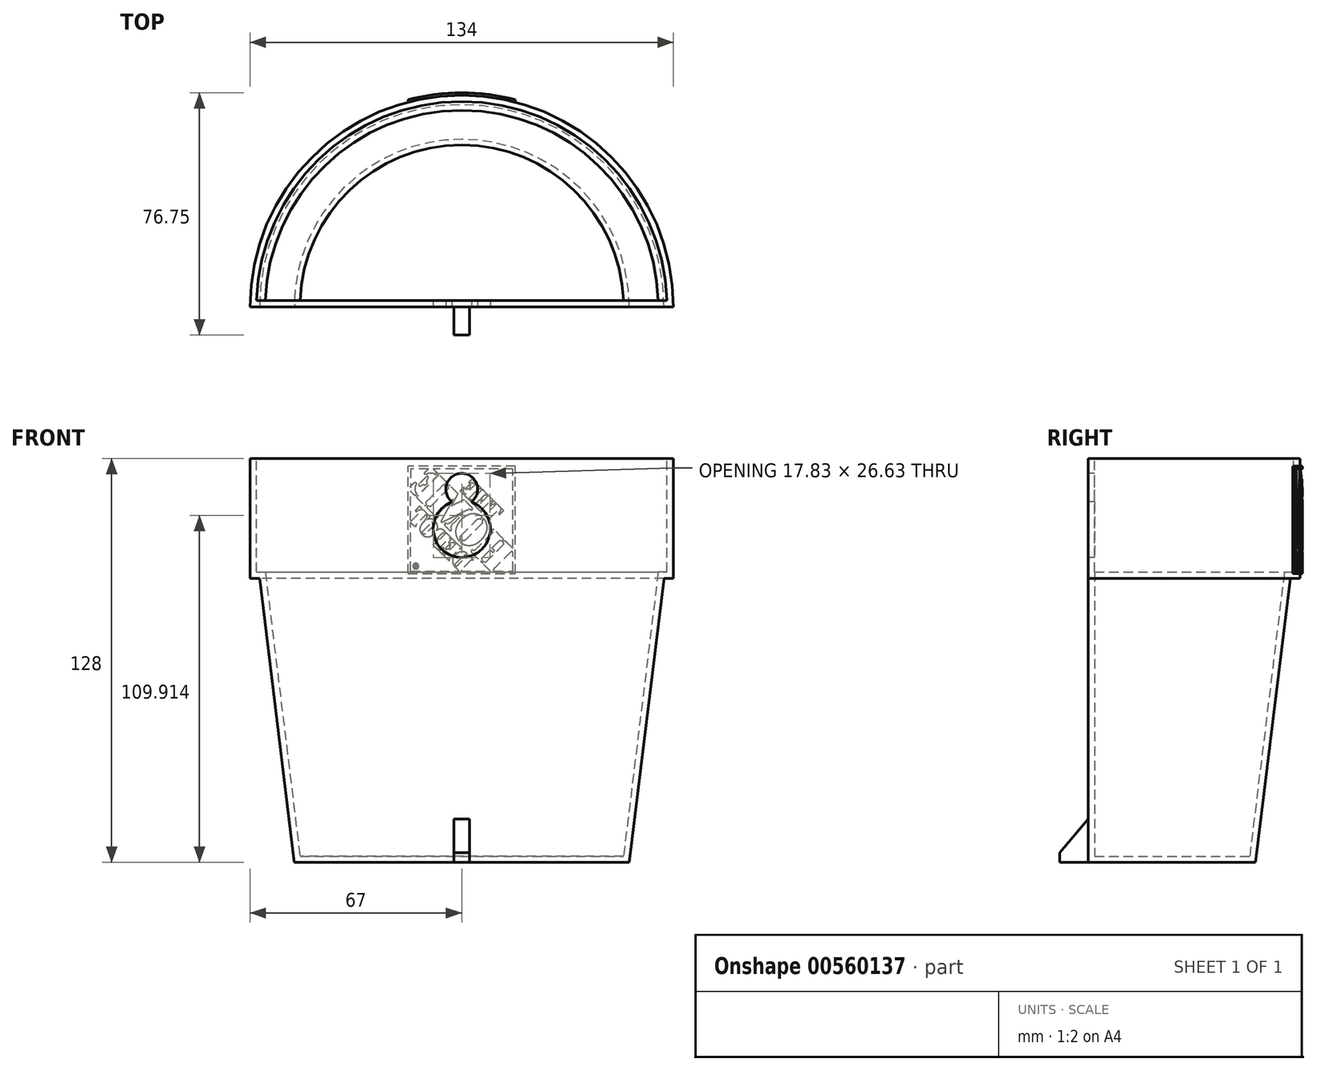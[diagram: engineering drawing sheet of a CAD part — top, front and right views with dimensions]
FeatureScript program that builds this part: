
annotation { "Feature Type Name" : "Feature", "Feature Type Description" : "" }
export const myFeature = defineFeature(function(context is Context, id is Id, definition is map)
    precondition{}
    {
        {
            var Q0;
            Q0=qCreatedBy(makeId("Front.planeOp"),FACE);
            var sketch = newSketch(context, id + "F0", { "sketchPlane" : qUnion([Q0])});
            skLineSegment(sketch, "E0", {"start": v(0, 77.42) * mm, "end": v(-67, 77.42) * mm});
            skLineSegment(sketch, "E1", {"start": v(-67, 77.42) * mm, "end": v(-67, 39.42) * mm});
            skLineSegment(sketch, "E2", {"start": v(0, -50.58) * mm, "end": v(-53, -50.58) * mm});
            skLineSegment(sketch, "E3", {"start": v(-67, 39.42) * mm, "end": v(-64, 39.42) * mm});
            skLineSegment(sketch, "E4", {"start": v(0, 77.42) * mm, "end": v(0, -50.58) * mm});
            skLineSegment(sketch, "E5", {"start": v(-64, 39.42) * mm, "end": v(-53, -50.58) * mm});
            skLineSegment(sketch, "E6.MirrorCS", {"start": v(0, 77.42) * mm, "end": v(67, 77.42) * mm});
            skLineSegment(sketch, "E7.MirrorCS", {"start": v(67, 77.42) * mm, "end": v(67, 39.42) * mm});
            skLineSegment(sketch, "E8.MirrorCS", {"start": v(67, 39.42) * mm, "end": v(64, 39.42) * mm});
            skLineSegment(sketch, "E9.MirrorCS", {"start": v(64, 39.42) * mm, "end": v(53, -50.58) * mm});
            skLineSegment(sketch, "E10.MirrorCS", {"start": v(0, -50.58) * mm, "end": v(53, -50.58) * mm});
            skSolve(sketch);
        }
        {
            var Q0;
            {var subQ0=sQuery(id+"F0.wireOp",EDGE,"E3");Q0=makeQuery(id+"F0.imprint","IMPRINT",FACE,{"disambiguationData":[TD([[makeQuery(id+"F0.imprint","IMPRINT",EDGE,{"derivedFrom":subQ0}),1.0]])]});}
            var Q1;
            {var subQ1=sQuery(id+"F0.wireOp",EDGE,"E0");Q1=makeQuery(id+"F0.imprint","IMPRINT",FACE,{"disambiguationData":[TD([[makeQuery(id+"F0.imprint","IMPRINT",EDGE,{"derivedFrom":subQ1}),1.0]])]});}
            var Q2;
            Q2=makeQuery(id+"F0.imprint","IMPRINT",FACE,{"disambiguationData":[TD([[makeQuery(id+"F0.imprint","IMPRINT",EDGE,{"derivedFrom":sQuery(id+"F0.wireOp",EDGE,"Kfnrekvc-ZjTY-c2iQ-cK4z-hKnBe4uEAVNk")}),1.0]])]});
            var Q3;
            Q3=sQuery(id+"F0.wireOp",EDGE,"E4");
            revolve(context, id + "F1", {"entities" : qUnion([Q0, Q1, Q2]), "axis" : qUnion([Q3]), "revolveType" : RevolveType.ONE_DIRECTION, "angle" : 180 * degree});
        }
        {
            var Q0;
            Q0=makeQuery(id+"FK2OT3XlAi37Aaq_1.splitOp","SPLIT",FACE,{"derivedFrom":makeQuery(id+"F1.opRevolve","SWEPT_FACE",FACE,{"disambiguationData":[OSD([sQuery(id+"F0.wireOp",EDGE,"E0")])]}),"isFromBackBody":true});
            shell(context, id + "F2", {"entities" : qUnion([Q0]), "thickness" : 2 * mm});
        }
        {
            var Q0;
            Q0=qCreatedBy(makeId("Front.planeOp"),FACE);
            var sketch = newSketch(context, id + "F3", { "sketchPlane" : qUnion([Q0])});
            skLineSegment(sketch, "E11.bottom", {"start": v(-2.5, -35.58) * mm, "end": v(2.5, -35.58) * mm});
            skLineSegment(sketch, "E11.top", {"start": v(-2.5, -50.58) * mm, "end": v(2.5, -50.58) * mm});
            skLineSegment(sketch, "E11.left", {"start": v(-2.5, -35.58) * mm, "end": v(-2.5, -50.58) * mm});
            skLineSegment(sketch, "E11.right", {"start": v(2.5, -35.58) * mm, "end": v(2.5, -50.58) * mm});
            skPoint(sketch, "E11.middle", {"position": v(0, -43.08) * mm});
            skSolve(sketch);
        }
        {
            var Q0;
            Q0=qSketchRegion(id+"F3",true);
            extrude(context, id + "F4", {"entities" : qUnion([Q0]), "operationType" : NewBodyOperationType.ADD, "depth" : 9 * mm});
        }
        {
            var Q0;
            Q0=qCreatedBy(makeId("Front.planeOp"),FACE);
            var sketch = newSketch(context, id + "F5", { "sketchPlane" : qUnion([Q0])});
            skCircle(sketch, "E12", {"center": v(0, 67.6) * mm, "radius": 5.05 * mm});
            skCircle(sketch, "E13", {"center": v(0, 55.07) * mm, "radius": 9.05 * mm});
            skSolve(sketch);
        }
        {
            var Q0;
            {var subQ0=sQuery(id+"F5.wireOp",EDGE,"E13");var subQ1=sQuery(id+"F5.wireOp",EDGE,"E12");var subQ2=makeQuery(id+"F5.imprint","INTERSECT",VERTEX,{"disambiguationData":[OD(0.0)],"derivedFrom":[subQ1,subQ0]});Q0=makeQuery(id+"F5.imprint","IMPRINT",FACE,{"disambiguationData":[TD([[makeQuery(id+"F5.imprint","IMPRINT",EDGE,{"disambiguationData":[TD([[subQ2,1.0]])],"derivedFrom":subQ1}),1.0]])]});}
            var Q1;
            {var subQ0=sQuery(id+"F5.wireOp",EDGE,"E13");var subQ1=sQuery(id+"F5.wireOp",EDGE,"E12");var subQ2=makeQuery(id+"F5.imprint","INTERSECT",VERTEX,{"disambiguationData":[OD(0.0)],"derivedFrom":[subQ1,subQ0]});Q1=makeQuery(id+"F5.imprint","IMPRINT",FACE,{"disambiguationData":[TD([[makeQuery(id+"F5.imprint","IMPRINT",EDGE,{"disambiguationData":[TD([[subQ2,-1.0]])],"derivedFrom":subQ1}),-1.0]])]});}
            var Q2;
            {var subQ0=sQuery(id+"F5.wireOp",EDGE,"E13");var subQ1=sQuery(id+"F5.wireOp",EDGE,"E12");var subQ2=makeQuery(id+"F5.imprint","INTERSECT",VERTEX,{"disambiguationData":[OD(0.0)],"derivedFrom":[subQ1,subQ0]});Q2=makeQuery(id+"F5.imprint","IMPRINT",FACE,{"disambiguationData":[TD([[makeQuery(id+"F5.imprint","IMPRINT",EDGE,{"disambiguationData":[TD([[subQ2,-1.0]])],"derivedFrom":subQ1}),1.0]])]});}
            var Q3;
            Q3=sQuery(id+"F5.wireOp",EDGE,"E12");
            var Q4;
            Q4=sQuery(id+"F5.wireOp",EDGE,"E13");
            extrude(context, id + "F6", {"entities" : qUnion([Q0, Q1, Q2]), "operationType" : NewBodyOperationType.REMOVE, "surfaceEntities" : qUnion([Q3, Q4]), "oppositeDirection" : true, "depth" : 10 * mm});
        }
        {
            var Q0;
            Q0=makeQuery(id+"F4.opExtrude","CAP_EDGE",EDGE,{"disambiguationData":[OSD([sQuery(id+"F3.wireOp",EDGE,"E11.bottom")])],"isStart":false});
            chamfer(context, id + "F7", {"entities" : qUnion([Q0]), "chamferType" : ChamferType.OFFSET_ANGLE, "width" : 10 * mm, "oppositeDirection" : false, "angle" : 50 * degree, "tangentPropagation" : true});
        }
        {
            var Q0;
            Q0=makeQuery(id+"F1.opRevolve","SWEPT_BODY",BODY,{"disambiguationData":[OSD([sQuery(id+"F0.wireOp",EDGE,"E0"),sQuery(id+"F0.wireOp",EDGE,"E1"),sQuery(id+"F0.wireOp",EDGE,"E2"),sQuery(id+"F0.wireOp",EDGE,"E3"),sQuery(id+"F0.wireOp",EDGE,"E4"),sQuery(id+"F0.wireOp",EDGE,"E5")])]});
            transform(context, id + "F8", {"entities" : qUnion([Q0]), "transformType" : TransformType.TRANSLATION_3D, "dx" : 0 * mm, "dy" : 0 * mm, "dz" : -7 * mm, "makeCopy" : false});
        }
        {
            var Q0;
            Q0=makeQuery(id+"F2.opShell","OFFSET_FACE",FACE,{"disambiguationData":[OSD([sQuery(id+"F0.wireOp",EDGE,"E0"),sQuery(id+"F0.wireOp",EDGE,"E1"),sQuery(id+"F0.wireOp",EDGE,"E2"),sQuery(id+"F0.wireOp",EDGE,"E3"),sQuery(id+"F0.wireOp",EDGE,"E4"),sQuery(id+"F0.wireOp",EDGE,"E5")])]});
            cPlane(context, id + "F9", {"entities" : qUnion([Q0]), "cplaneType" : CPlaneType.OFFSET, "offset" : 80 * mm, "width" : 150 * mm, "height" : 150 * mm});
        }
        {
            var Q0;
            Q0=qCreatedBy(id+"F9.planeOp",FACE);
            var sketch = newSketch(context, id + "F10", { "sketchPlane" : qUnion([Q0])});
            skLineSegment(sketch, "E14", {"start": v(0.8, 34.74) * mm, "end": v(0.8, 34.75) * mm});
            skLineSegment(sketch, "E15", {"start": v(0.8, 34.75) * mm, "end": v(0.8, 34.74) * mm});
            skLineSegment(sketch, "E16", {"start": v(0.8, 34.74) * mm, "end": v(0.8, 34.74) * mm});
            skLineSegment(sketch, "E17", {"start": v(14.2, 36.81) * mm, "end": v(14.2, 35.76) * mm});
            skLineSegment(sketch, "E18", {"start": v(14.2, 35.76) * mm, "end": v(14.36, 35.76) * mm});
            skLineSegment(sketch, "E19", {"start": v(14.36, 35.76) * mm, "end": v(14.36, 36.22) * mm});
            skLineSegment(sketch, "E20", {"start": v(14.36, 36.22) * mm, "end": v(14.54, 36.22) * mm});
            skLineSegment(sketch, "E21", {"start": v(14.54, 36.22) * mm, "end": v(14.64, 36.06) * mm});
            skLineSegment(sketch, "E22", {"start": v(14.64, 36.06) * mm, "end": v(14.66, 36.02) * mm});
            skLineSegment(sketch, "E23", {"start": v(14.66, 36.02) * mm, "end": v(14.81, 35.77) * mm});
            skLineSegment(sketch, "E24", {"start": v(14.81, 35.77) * mm, "end": v(14.98, 35.76) * mm});
            skLineSegment(sketch, "E25", {"start": v(14.98, 35.76) * mm, "end": v(14.98, 35.77) * mm});
            skLineSegment(sketch, "E26", {"start": v(14.98, 35.77) * mm, "end": v(14.96, 35.8) * mm});
            skLineSegment(sketch, "E27", {"start": v(14.96, 35.8) * mm, "end": v(14.94, 35.84) * mm});
            skLineSegment(sketch, "E28", {"start": v(14.94, 35.84) * mm, "end": v(14.74, 36.15) * mm});
            skLineSegment(sketch, "E29", {"start": v(14.74, 36.15) * mm, "end": v(14.72, 36.18) * mm});
            skLineSegment(sketch, "E30", {"start": v(14.72, 36.18) * mm, "end": v(14.7, 36.22) * mm});
            skLineSegment(sketch, "E31", {"start": v(14.7, 36.22) * mm, "end": v(14.7, 36.22) * mm});
            skLineSegment(sketch, "E32", {"start": v(14.7, 36.22) * mm, "end": v(14.71, 36.23) * mm});
            skLineSegment(sketch, "E33", {"start": v(14.71, 36.23) * mm, "end": v(14.77, 36.24) * mm});
            skLineSegment(sketch, "E34", {"start": v(14.77, 36.24) * mm, "end": v(14.82, 36.26) * mm});
            skLineSegment(sketch, "E35", {"start": v(14.82, 36.26) * mm, "end": v(14.86, 36.28) * mm});
            skLineSegment(sketch, "E36", {"start": v(14.86, 36.28) * mm, "end": v(14.9, 36.31) * mm});
            skLineSegment(sketch, "E37", {"start": v(14.9, 36.31) * mm, "end": v(14.92, 36.35) * mm});
            skLineSegment(sketch, "E38", {"start": v(14.92, 36.35) * mm, "end": v(14.94, 36.4) * mm});
            skLineSegment(sketch, "E39", {"start": v(14.94, 36.4) * mm, "end": v(14.96, 36.45) * mm});
            skLineSegment(sketch, "E40", {"start": v(14.96, 36.45) * mm, "end": v(14.96, 36.52) * mm});
            skLineSegment(sketch, "E41", {"start": v(14.96, 36.52) * mm, "end": v(14.96, 36.58) * mm});
            skLineSegment(sketch, "E42", {"start": v(14.96, 36.58) * mm, "end": v(14.95, 36.62) * mm});
            skLineSegment(sketch, "E43", {"start": v(14.95, 36.62) * mm, "end": v(14.93, 36.66) * mm});
            skLineSegment(sketch, "E44", {"start": v(14.93, 36.66) * mm, "end": v(14.91, 36.7) * mm});
            skLineSegment(sketch, "E45", {"start": v(14.91, 36.7) * mm, "end": v(14.88, 36.73) * mm});
            skLineSegment(sketch, "E46", {"start": v(14.88, 36.73) * mm, "end": v(14.85, 36.75) * mm});
            skLineSegment(sketch, "E47", {"start": v(14.85, 36.75) * mm, "end": v(14.8, 36.77) * mm});
            skLineSegment(sketch, "E48", {"start": v(14.8, 36.77) * mm, "end": v(14.75, 36.8) * mm});
            skLineSegment(sketch, "E49", {"start": v(14.75, 36.8) * mm, "end": v(14.7, 36.8) * mm});
            skLineSegment(sketch, "E50", {"start": v(14.7, 36.8) * mm, "end": v(14.2, 36.81) * mm});
            skLineSegment(sketch, "E51", {"start": v(14.7, 35.54) * mm, "end": v(14.77, 35.56) * mm});
            skLineSegment(sketch, "E52", {"start": v(14.77, 35.56) * mm, "end": v(14.83, 35.58) * mm});
            skLineSegment(sketch, "E53", {"start": v(14.83, 35.58) * mm, "end": v(14.91, 35.62) * mm});
            skLineSegment(sketch, "E54", {"start": v(14.91, 35.62) * mm, "end": v(15, 35.67) * mm});
            skLineSegment(sketch, "E55", {"start": v(15, 35.67) * mm, "end": v(15.02, 35.69) * mm});
            skLineSegment(sketch, "E56", {"start": v(15.02, 35.69) * mm, "end": v(15.02, 35.7) * mm});
            skLineSegment(sketch, "E57", {"start": v(15.02, 35.7) * mm, "end": v(15.07, 35.74) * mm});
            skLineSegment(sketch, "E58", {"start": v(15.07, 35.74) * mm, "end": v(15.14, 35.82) * mm});
            skLineSegment(sketch, "E59", {"start": v(15.14, 35.82) * mm, "end": v(15.16, 35.84) * mm});
            skLineSegment(sketch, "E60", {"start": v(15.16, 35.84) * mm, "end": v(15.16, 35.84) * mm});
            skLineSegment(sketch, "E61", {"start": v(15.16, 35.84) * mm, "end": v(15.16, 35.85) * mm});
            skLineSegment(sketch, "E62", {"start": v(15.16, 35.85) * mm, "end": v(15.23, 36) * mm});
            skLineSegment(sketch, "E63", {"start": v(15.23, 36) * mm, "end": v(15.24, 36) * mm});
            skLineSegment(sketch, "E64", {"start": v(15.24, 36) * mm, "end": v(15.25, 36.04) * mm});
            skLineSegment(sketch, "E65", {"start": v(15.25, 36.04) * mm, "end": v(15.26, 36.1) * mm});
            skLineSegment(sketch, "E66", {"start": v(15.26, 36.1) * mm, "end": v(15.27, 36.15) * mm});
            skLineSegment(sketch, "E67", {"start": v(15.27, 36.15) * mm, "end": v(15.28, 36.26) * mm});
            skLineSegment(sketch, "E68", {"start": v(15.28, 36.26) * mm, "end": v(15.28, 36.38) * mm});
            skLineSegment(sketch, "E69", {"start": v(15.28, 36.38) * mm, "end": v(15.27, 36.44) * mm});
            skLineSegment(sketch, "E70", {"start": v(15.27, 36.44) * mm, "end": v(15.26, 36.5) * mm});
            skLineSegment(sketch, "E71", {"start": v(15.26, 36.5) * mm, "end": v(15.23, 36.58) * mm});
            skLineSegment(sketch, "E72", {"start": v(15.23, 36.58) * mm, "end": v(15.2, 36.67) * mm});
            skLineSegment(sketch, "E73", {"start": v(15.2, 36.67) * mm, "end": v(15.14, 36.74) * mm});
            skLineSegment(sketch, "E74", {"start": v(15.14, 36.74) * mm, "end": v(15.09, 36.81) * mm});
            skLineSegment(sketch, "E75", {"start": v(15.09, 36.81) * mm, "end": v(15.02, 36.87) * mm});
            skLineSegment(sketch, "E76", {"start": v(15.02, 36.87) * mm, "end": v(14.95, 36.93) * mm});
            skLineSegment(sketch, "E77", {"start": v(14.95, 36.93) * mm, "end": v(14.88, 36.97) * mm});
            skLineSegment(sketch, "E78", {"start": v(14.88, 36.97) * mm, "end": v(14.8, 37) * mm});
            skLineSegment(sketch, "E79", {"start": v(14.8, 37) * mm, "end": v(14.72, 37.02) * mm});
            skLineSegment(sketch, "E80", {"start": v(14.72, 37.02) * mm, "end": v(14.65, 37.04) * mm});
            skLineSegment(sketch, "E81", {"start": v(14.65, 37.04) * mm, "end": v(14.58, 37.04) * mm});
            skLineSegment(sketch, "E82", {"start": v(14.58, 37.04) * mm, "end": v(14.5, 37.04) * mm});
            skLineSegment(sketch, "E83", {"start": v(14.5, 37.04) * mm, "end": v(14.44, 37.04) * mm});
            skLineSegment(sketch, "E84", {"start": v(14.44, 37.04) * mm, "end": v(14.37, 37.02) * mm});
            skLineSegment(sketch, "E85", {"start": v(14.37, 37.02) * mm, "end": v(14.3, 37) * mm});
            skLineSegment(sketch, "E86", {"start": v(14.3, 37) * mm, "end": v(14.24, 36.98) * mm});
            skLineSegment(sketch, "E87", {"start": v(14.24, 36.98) * mm, "end": v(14.18, 36.95) * mm});
            skLineSegment(sketch, "E88", {"start": v(14.18, 36.95) * mm, "end": v(14.17, 36.95) * mm});
            skLineSegment(sketch, "E89", {"start": v(14.17, 36.95) * mm, "end": v(14.17, 36.95) * mm});
            skLineSegment(sketch, "E90", {"start": v(14.17, 36.95) * mm, "end": v(14.18, 36.95) * mm});
            skLineSegment(sketch, "E91", {"start": v(14.18, 36.95) * mm, "end": v(14.13, 36.92) * mm});
            skLineSegment(sketch, "E92", {"start": v(14.13, 36.92) * mm, "end": v(14.08, 36.89) * mm});
            skLineSegment(sketch, "E93", {"start": v(14.08, 36.89) * mm, "end": v(14.04, 36.85) * mm});
            skLineSegment(sketch, "E94", {"start": v(14.04, 36.85) * mm, "end": v(14, 36.8) * mm});
            skLineSegment(sketch, "E95", {"start": v(14, 36.8) * mm, "end": v(13.96, 36.76) * mm});
            skLineSegment(sketch, "E96", {"start": v(13.96, 36.76) * mm, "end": v(13.93, 36.71) * mm});
            skLineSegment(sketch, "E97", {"start": v(13.93, 36.71) * mm, "end": v(13.9, 36.66) * mm});
            skLineSegment(sketch, "E98", {"start": v(13.9, 36.66) * mm, "end": v(13.87, 36.61) * mm});
            skLineSegment(sketch, "E99", {"start": v(13.87, 36.61) * mm, "end": v(13.85, 36.56) * mm});
            skLineSegment(sketch, "E100", {"start": v(13.85, 36.56) * mm, "end": v(13.83, 36.5) * mm});
            skLineSegment(sketch, "E101", {"start": v(13.83, 36.5) * mm, "end": v(13.82, 36.44) * mm});
            skLineSegment(sketch, "E102", {"start": v(13.82, 36.44) * mm, "end": v(13.81, 36.39) * mm});
            skLineSegment(sketch, "E103", {"start": v(13.81, 36.39) * mm, "end": v(13.8, 36.33) * mm});
            skLineSegment(sketch, "E104", {"start": v(13.8, 36.33) * mm, "end": v(13.8, 36.27) * mm});
            skLineSegment(sketch, "E105", {"start": v(13.8, 36.27) * mm, "end": v(13.8, 36.2) * mm});
            skLineSegment(sketch, "E106", {"start": v(13.8, 36.2) * mm, "end": v(13.82, 36.14) * mm});
            skLineSegment(sketch, "E107", {"start": v(13.82, 36.14) * mm, "end": v(13.83, 36.08) * mm});
            skLineSegment(sketch, "E108", {"start": v(13.83, 36.08) * mm, "end": v(13.85, 36) * mm});
            skLineSegment(sketch, "E109", {"start": v(13.85, 36) * mm, "end": v(13.88, 35.94) * mm});
            skLineSegment(sketch, "E110", {"start": v(13.88, 35.94) * mm, "end": v(13.92, 35.88) * mm});
            skLineSegment(sketch, "E111", {"start": v(13.92, 35.88) * mm, "end": v(13.96, 35.82) * mm});
            skLineSegment(sketch, "E112", {"start": v(13.96, 35.82) * mm, "end": v(14, 35.76) * mm});
            skLineSegment(sketch, "E113", {"start": v(14, 35.76) * mm, "end": v(14.06, 35.7) * mm});
            skLineSegment(sketch, "E114", {"start": v(14.06, 35.7) * mm, "end": v(14.11, 35.66) * mm});
            skLineSegment(sketch, "E115", {"start": v(14.11, 35.66) * mm, "end": v(14.18, 35.62) * mm});
            skLineSegment(sketch, "E116", {"start": v(14.18, 35.62) * mm, "end": v(14.23, 35.6) * mm});
            skLineSegment(sketch, "E117", {"start": v(14.23, 35.6) * mm, "end": v(14.29, 35.57) * mm});
            skLineSegment(sketch, "E118", {"start": v(14.29, 35.57) * mm, "end": v(14.35, 35.55) * mm});
            skLineSegment(sketch, "E119", {"start": v(14.35, 35.55) * mm, "end": v(14.4, 35.54) * mm});
            skLineSegment(sketch, "E120", {"start": v(14.4, 35.54) * mm, "end": v(14.48, 35.53) * mm});
            skLineSegment(sketch, "E121", {"start": v(14.48, 35.53) * mm, "end": v(14.56, 35.53) * mm});
            skLineSegment(sketch, "E122", {"start": v(14.56, 35.53) * mm, "end": v(14.64, 35.53) * mm});
            skLineSegment(sketch, "E123", {"start": v(14.64, 35.53) * mm, "end": v(14.7, 35.54) * mm});
            skLineSegment(sketch, "E124", {"start": v(14.36, 36.35) * mm, "end": v(14.68, 36.36) * mm});
            skLineSegment(sketch, "E125", {"start": v(14.68, 36.36) * mm, "end": v(14.7, 36.36) * mm});
            skLineSegment(sketch, "E126", {"start": v(14.7, 36.36) * mm, "end": v(14.74, 36.39) * mm});
            skLineSegment(sketch, "E127", {"start": v(14.74, 36.39) * mm, "end": v(14.76, 36.4) * mm});
            skLineSegment(sketch, "E128", {"start": v(14.76, 36.4) * mm, "end": v(14.78, 36.42) * mm});
            skLineSegment(sketch, "E129", {"start": v(14.78, 36.42) * mm, "end": v(14.8, 36.46) * mm});
            skLineSegment(sketch, "E130", {"start": v(14.8, 36.46) * mm, "end": v(14.8, 36.52) * mm});
            skLineSegment(sketch, "E131", {"start": v(14.8, 36.52) * mm, "end": v(14.8, 36.57) * mm});
            skLineSegment(sketch, "E132", {"start": v(14.8, 36.57) * mm, "end": v(14.78, 36.6) * mm});
            skLineSegment(sketch, "E133", {"start": v(14.78, 36.6) * mm, "end": v(14.75, 36.64) * mm});
            skLineSegment(sketch, "E134", {"start": v(14.75, 36.64) * mm, "end": v(14.7, 36.66) * mm});
            skLineSegment(sketch, "E135", {"start": v(14.7, 36.66) * mm, "end": v(14.68, 36.67) * mm});
            skLineSegment(sketch, "E136", {"start": v(14.68, 36.67) * mm, "end": v(14.36, 36.68) * mm});
            skLineSegment(sketch, "E137", {"start": v(14.36, 36.68) * mm, "end": v(14.35, 36.35) * mm});
            skLineSegment(sketch, "E138", {"start": v(14.35, 36.35) * mm, "end": v(14.36, 36.35) * mm});
            skLineSegment(sketch, "E139", {"start": v(1.91, 36.44) * mm, "end": v(2.21, 36.14) * mm});
            skLineSegment(sketch, "E140", {"start": v(2.21, 36.14) * mm, "end": v(2.23, 36.14) * mm});
            skLineSegment(sketch, "E141", {"start": v(2.23, 36.14) * mm, "end": v(2.34, 36.27) * mm});
            skLineSegment(sketch, "E142", {"start": v(2.34, 36.27) * mm, "end": v(2.34, 36.27) * mm});
            skLineSegment(sketch, "E143", {"start": v(2.34, 36.27) * mm, "end": v(2.38, 36.31) * mm});
            skLineSegment(sketch, "E144", {"start": v(2.38, 36.31) * mm, "end": v(2.46, 36.41) * mm});
            skLineSegment(sketch, "E145", {"start": v(2.46, 36.41) * mm, "end": v(2.5, 36.47) * mm});
            skLineSegment(sketch, "E146", {"start": v(2.5, 36.47) * mm, "end": v(2.5, 36.48) * mm});
            skLineSegment(sketch, "E147", {"start": v(2.5, 36.48) * mm, "end": v(2.5, 36.49) * mm});
            skLineSegment(sketch, "E148", {"start": v(2.5, 36.49) * mm, "end": v(2.5, 36.49) * mm});
            skLineSegment(sketch, "E149", {"start": v(2.5, 36.49) * mm, "end": v(2.51, 36.49) * mm});
            skLineSegment(sketch, "E150", {"start": v(2.51, 36.49) * mm, "end": v(2.55, 36.56) * mm});
            skLineSegment(sketch, "E151", {"start": v(2.55, 36.56) * mm, "end": v(2.62, 36.68) * mm});
            skLineSegment(sketch, "E152", {"start": v(2.62, 36.68) * mm, "end": v(2.68, 36.8) * mm});
            skLineSegment(sketch, "E153", {"start": v(2.68, 36.8) * mm, "end": v(2.73, 36.91) * mm});
            skLineSegment(sketch, "E154", {"start": v(2.73, 36.91) * mm, "end": v(2.78, 37.03) * mm});
            skLineSegment(sketch, "E155", {"start": v(2.78, 37.03) * mm, "end": v(2.82, 37.15) * mm});
            skLineSegment(sketch, "E156", {"start": v(2.82, 37.15) * mm, "end": v(2.85, 37.28) * mm});
            skLineSegment(sketch, "E157", {"start": v(2.85, 37.28) * mm, "end": v(2.87, 37.4) * mm});
            skLineSegment(sketch, "E158", {"start": v(2.87, 37.4) * mm, "end": v(2.9, 37.54) * mm});
            skLineSegment(sketch, "E159", {"start": v(2.9, 37.54) * mm, "end": v(2.9, 37.62) * mm});
            skLineSegment(sketch, "E160", {"start": v(2.9, 37.62) * mm, "end": v(2.91, 37.93) * mm});
            skLineSegment(sketch, "E161", {"start": v(2.91, 37.93) * mm, "end": v(2.9, 38.03) * mm});
            skLineSegment(sketch, "E162", {"start": v(2.9, 38.03) * mm, "end": v(2.88, 38.22) * mm});
            skLineSegment(sketch, "E163", {"start": v(2.88, 38.22) * mm, "end": v(2.85, 38.4) * mm});
            skLineSegment(sketch, "E164", {"start": v(2.85, 38.4) * mm, "end": v(2.8, 38.58) * mm});
            skLineSegment(sketch, "E165", {"start": v(2.8, 38.58) * mm, "end": v(2.74, 38.76) * mm});
            skLineSegment(sketch, "E166", {"start": v(2.74, 38.76) * mm, "end": v(2.66, 38.93) * mm});
            skLineSegment(sketch, "E167", {"start": v(2.66, 38.93) * mm, "end": v(2.58, 39.1) * mm});
            skLineSegment(sketch, "E168", {"start": v(2.58, 39.1) * mm, "end": v(2.48, 39.26) * mm});
            skLineSegment(sketch, "E169", {"start": v(2.48, 39.26) * mm, "end": v(2.36, 39.43) * mm});
            skLineSegment(sketch, "E170", {"start": v(2.36, 39.43) * mm, "end": v(2.3, 39.5) * mm});
            skLineSegment(sketch, "E171", {"start": v(2.3, 39.5) * mm, "end": v(2.28, 39.54) * mm});
            skLineSegment(sketch, "E172", {"start": v(2.28, 39.54) * mm, "end": v(2.21, 39.61) * mm});
            skLineSegment(sketch, "E173", {"start": v(2.21, 39.61) * mm, "end": v(2.17, 39.65) * mm});
            skLineSegment(sketch, "E174", {"start": v(2.17, 39.65) * mm, "end": v(2.1, 39.74) * mm});
            skLineSegment(sketch, "E175", {"start": v(2.1, 39.74) * mm, "end": v(1.98, 39.85) * mm});
            skLineSegment(sketch, "E176", {"start": v(1.98, 39.85) * mm, "end": v(1.86, 39.95) * mm});
            skLineSegment(sketch, "E177", {"start": v(1.86, 39.95) * mm, "end": v(1.74, 40.06) * mm});
            skLineSegment(sketch, "E178", {"start": v(1.74, 40.06) * mm, "end": v(1.6, 40.16) * mm});
            skLineSegment(sketch, "E179", {"start": v(1.6, 40.16) * mm, "end": v(1.47, 40.26) * mm});
            skLineSegment(sketch, "E180", {"start": v(1.47, 40.26) * mm, "end": v(1.34, 40.35) * mm});
            skLineSegment(sketch, "E181", {"start": v(1.34, 40.35) * mm, "end": v(1.2, 40.43) * mm});
            skLineSegment(sketch, "E182", {"start": v(1.2, 40.43) * mm, "end": v(1.07, 40.5) * mm});
            skLineSegment(sketch, "E183", {"start": v(1.07, 40.5) * mm, "end": v(1, 40.55) * mm});
            skLineSegment(sketch, "E184", {"start": v(1, 40.55) * mm, "end": v(1, 40.55) * mm});
            skLineSegment(sketch, "E185", {"start": v(1, 40.55) * mm, "end": v(0.94, 40.58) * mm});
            skLineSegment(sketch, "E186", {"start": v(0.94, 40.58) * mm, "end": v(0.82, 40.63) * mm});
            skLineSegment(sketch, "E187", {"start": v(0.82, 40.63) * mm, "end": v(0.7, 40.68) * mm});
            skLineSegment(sketch, "E188", {"start": v(0.7, 40.68) * mm, "end": v(0.6, 40.72) * mm});
            skLineSegment(sketch, "E189", {"start": v(0.6, 40.72) * mm, "end": v(0.48, 40.76) * mm});
            skLineSegment(sketch, "E190", {"start": v(0.48, 40.76) * mm, "end": v(0.36, 40.79) * mm});
            skLineSegment(sketch, "E191", {"start": v(0.36, 40.79) * mm, "end": v(0.24, 40.81) * mm});
            skLineSegment(sketch, "E192", {"start": v(0.24, 40.81) * mm, "end": v(0.13, 40.83) * mm});
            skLineSegment(sketch, "E193", {"start": v(0.13, 40.83) * mm, "end": v(0, 40.85) * mm});
            skLineSegment(sketch, "E194", {"start": v(0, 40.85) * mm, "end": v(-0.08, 40.85) * mm});
            skLineSegment(sketch, "E195", {"start": v(-0.08, 40.85) * mm, "end": v(-0.41, 40.85) * mm});
            skLineSegment(sketch, "E196", {"start": v(-0.41, 40.85) * mm, "end": v(-0.5, 40.83) * mm});
            skLineSegment(sketch, "E197", {"start": v(-0.5, 40.83) * mm, "end": v(-0.63, 40.8) * mm});
            skLineSegment(sketch, "E198", {"start": v(-0.63, 40.8) * mm, "end": v(-0.75, 40.78) * mm});
            skLineSegment(sketch, "E199", {"start": v(-0.75, 40.78) * mm, "end": v(-0.87, 40.74) * mm});
            skLineSegment(sketch, "E200", {"start": v(-0.87, 40.74) * mm, "end": v(-1, 40.7) * mm});
            skLineSegment(sketch, "E201", {"start": v(-1, 40.7) * mm, "end": v(-1.1, 40.65) * mm});
            skLineSegment(sketch, "E202", {"start": v(-1.1, 40.65) * mm, "end": v(-1.22, 40.59) * mm});
            skLineSegment(sketch, "E203", {"start": v(-1.22, 40.59) * mm, "end": v(-1.34, 40.52) * mm});
            skLineSegment(sketch, "E204", {"start": v(-1.34, 40.52) * mm, "end": v(-1.45, 40.45) * mm});
            skLineSegment(sketch, "E205", {"start": v(-1.45, 40.45) * mm, "end": v(-1.5, 40.41) * mm});
            skLineSegment(sketch, "E206", {"start": v(-1.5, 40.41) * mm, "end": v(-1.54, 40.38) * mm});
            skLineSegment(sketch, "E207", {"start": v(-1.54, 40.38) * mm, "end": v(-1.65, 40.29) * mm});
            skLineSegment(sketch, "E208", {"start": v(-1.65, 40.29) * mm, "end": v(-1.76, 40.19) * mm});
            skLineSegment(sketch, "E209", {"start": v(-1.76, 40.19) * mm, "end": v(-1.8, 40.15) * mm});
            skLineSegment(sketch, "E210", {"start": v(-1.8, 40.15) * mm, "end": v(-1.5, 39.84) * mm});
            skLineSegment(sketch, "E211", {"start": v(-1.5, 39.84) * mm, "end": v(-1.45, 39.87) * mm});
            skLineSegment(sketch, "E212", {"start": v(-1.45, 39.87) * mm, "end": v(-1.37, 39.91) * mm});
            skLineSegment(sketch, "E213", {"start": v(-1.37, 39.91) * mm, "end": v(-1.3, 39.94) * mm});
            skLineSegment(sketch, "E214", {"start": v(-1.3, 39.94) * mm, "end": v(-1.23, 39.95) * mm});
            skLineSegment(sketch, "E215", {"start": v(-1.23, 39.95) * mm, "end": v(-1.15, 39.95) * mm});
            skLineSegment(sketch, "E216", {"start": v(-1.15, 39.95) * mm, "end": v(-1.06, 39.94) * mm});
            skLineSegment(sketch, "E217", {"start": v(-1.06, 39.94) * mm, "end": v(-0.97, 39.91) * mm});
            skLineSegment(sketch, "E218", {"start": v(-0.97, 39.91) * mm, "end": v(-0.88, 39.87) * mm});
            skLineSegment(sketch, "E219", {"start": v(-0.88, 39.87) * mm, "end": v(-0.78, 39.8) * mm});
            skLineSegment(sketch, "E220", {"start": v(-0.78, 39.8) * mm, "end": v(-0.72, 39.75) * mm});
            skLineSegment(sketch, "E221", {"start": v(-0.72, 39.75) * mm, "end": v(1.79, 37.25) * mm});
            skLineSegment(sketch, "E222", {"start": v(1.79, 37.25) * mm, "end": v(1.81, 37.22) * mm});
            skLineSegment(sketch, "E223", {"start": v(1.81, 37.22) * mm, "end": v(1.88, 37.13) * mm});
            skLineSegment(sketch, "E224", {"start": v(1.88, 37.13) * mm, "end": v(1.93, 37.07) * mm});
            skLineSegment(sketch, "E225", {"start": v(1.93, 37.07) * mm, "end": v(1.93, 37.07) * mm});
            skLineSegment(sketch, "E226", {"start": v(1.93, 37.07) * mm, "end": v(1.93, 37.06) * mm});
            skLineSegment(sketch, "E227", {"start": v(1.93, 37.06) * mm, "end": v(1.93, 37.06) * mm});
            skLineSegment(sketch, "E228", {"start": v(1.93, 37.06) * mm, "end": v(1.96, 37.02) * mm});
            skLineSegment(sketch, "E229", {"start": v(1.96, 37.02) * mm, "end": v(1.99, 36.95) * mm});
            skLineSegment(sketch, "E230", {"start": v(1.99, 36.95) * mm, "end": v(2.01, 36.88) * mm});
            skLineSegment(sketch, "E231", {"start": v(2.01, 36.88) * mm, "end": v(2.02, 36.81) * mm});
            skLineSegment(sketch, "E232", {"start": v(2.02, 36.81) * mm, "end": v(2.03, 36.74) * mm});
            skLineSegment(sketch, "E233", {"start": v(2.03, 36.74) * mm, "end": v(2.02, 36.67) * mm});
            skLineSegment(sketch, "E234", {"start": v(2.02, 36.67) * mm, "end": v(2, 36.6) * mm});
            skLineSegment(sketch, "E235", {"start": v(2, 36.6) * mm, "end": v(1.97, 36.54) * mm});
            skLineSegment(sketch, "E236", {"start": v(1.97, 36.54) * mm, "end": v(1.93, 36.47) * mm});
            skLineSegment(sketch, "E237", {"start": v(1.93, 36.47) * mm, "end": v(1.91, 36.44) * mm});
            skLineSegment(sketch, "E238", {"start": v(14.38, 35.4) * mm, "end": v(14.46, 35.38) * mm});
            skLineSegment(sketch, "E239", {"start": v(14.46, 35.38) * mm, "end": v(14.57, 35.38) * mm});
            skLineSegment(sketch, "E240", {"start": v(14.57, 35.38) * mm, "end": v(14.69, 35.39) * mm});
            skLineSegment(sketch, "E241", {"start": v(14.69, 35.39) * mm, "end": v(14.74, 35.4) * mm});
            skLineSegment(sketch, "E242", {"start": v(14.74, 35.4) * mm, "end": v(14.8, 35.41) * mm});
            skLineSegment(sketch, "E243", {"start": v(14.8, 35.41) * mm, "end": v(14.87, 35.44) * mm});
            skLineSegment(sketch, "E244", {"start": v(14.87, 35.44) * mm, "end": v(14.94, 35.46) * mm});
            skLineSegment(sketch, "E245", {"start": v(14.94, 35.46) * mm, "end": v(15, 35.5) * mm});
            skLineSegment(sketch, "E246", {"start": v(15, 35.5) * mm, "end": v(15.06, 35.53) * mm});
            skLineSegment(sketch, "E247", {"start": v(15.06, 35.53) * mm, "end": v(15.11, 35.57) * mm});
            skLineSegment(sketch, "E248", {"start": v(15.11, 35.57) * mm, "end": v(15.16, 35.61) * mm});
            skLineSegment(sketch, "E249", {"start": v(15.16, 35.61) * mm, "end": v(15.21, 35.66) * mm});
            skLineSegment(sketch, "E250", {"start": v(15.21, 35.66) * mm, "end": v(15.26, 35.7) * mm});
            skLineSegment(sketch, "E251", {"start": v(15.26, 35.7) * mm, "end": v(15.3, 35.76) * mm});
            skLineSegment(sketch, "E252", {"start": v(15.3, 35.76) * mm, "end": v(15.33, 35.81) * mm});
            skLineSegment(sketch, "E253", {"start": v(15.33, 35.81) * mm, "end": v(15.37, 35.87) * mm});
            skLineSegment(sketch, "E254", {"start": v(15.37, 35.87) * mm, "end": v(15.4, 35.93) * mm});
            skLineSegment(sketch, "E255", {"start": v(15.4, 35.93) * mm, "end": v(15.42, 36) * mm});
            skLineSegment(sketch, "E256", {"start": v(15.42, 36) * mm, "end": v(15.44, 36.06) * mm});
            skLineSegment(sketch, "E257", {"start": v(15.44, 36.06) * mm, "end": v(15.45, 36.13) * mm});
            skLineSegment(sketch, "E258", {"start": v(15.45, 36.13) * mm, "end": v(15.46, 36.2) * mm});
            skLineSegment(sketch, "E259", {"start": v(15.46, 36.2) * mm, "end": v(15.46, 36.29) * mm});
            skLineSegment(sketch, "E260", {"start": v(15.46, 36.29) * mm, "end": v(15.46, 36.37) * mm});
            skLineSegment(sketch, "E261", {"start": v(15.46, 36.37) * mm, "end": v(15.45, 36.45) * mm});
            skLineSegment(sketch, "E262", {"start": v(15.45, 36.45) * mm, "end": v(15.44, 36.52) * mm});
            skLineSegment(sketch, "E263", {"start": v(15.44, 36.52) * mm, "end": v(15.42, 36.59) * mm});
            skLineSegment(sketch, "E264", {"start": v(15.42, 36.59) * mm, "end": v(15.39, 36.65) * mm});
            skLineSegment(sketch, "E265", {"start": v(15.39, 36.65) * mm, "end": v(15.36, 36.72) * mm});
            skLineSegment(sketch, "E266", {"start": v(15.36, 36.72) * mm, "end": v(15.32, 36.78) * mm});
            skLineSegment(sketch, "E267", {"start": v(15.32, 36.78) * mm, "end": v(15.28, 36.83) * mm});
            skLineSegment(sketch, "E268", {"start": v(15.28, 36.83) * mm, "end": v(15.24, 36.89) * mm});
            skLineSegment(sketch, "E269", {"start": v(15.24, 36.89) * mm, "end": v(15.18, 36.94) * mm});
            skLineSegment(sketch, "E270", {"start": v(15.18, 36.94) * mm, "end": v(15.14, 36.98) * mm});
            skLineSegment(sketch, "E271", {"start": v(15.14, 36.98) * mm, "end": v(15.08, 37.02) * mm});
            skLineSegment(sketch, "E272", {"start": v(15.08, 37.02) * mm, "end": v(15.03, 37.06) * mm});
            skLineSegment(sketch, "E273", {"start": v(15.03, 37.06) * mm, "end": v(14.98, 37.09) * mm});
            skLineSegment(sketch, "E274", {"start": v(14.98, 37.09) * mm, "end": v(14.92, 37.12) * mm});
            skLineSegment(sketch, "E275", {"start": v(14.92, 37.12) * mm, "end": v(14.86, 37.14) * mm});
            skLineSegment(sketch, "E276", {"start": v(14.86, 37.14) * mm, "end": v(14.8, 37.16) * mm});
            skLineSegment(sketch, "E277", {"start": v(14.8, 37.16) * mm, "end": v(14.73, 37.17) * mm});
            skLineSegment(sketch, "E278", {"start": v(14.73, 37.17) * mm, "end": v(14.66, 37.19) * mm});
            skLineSegment(sketch, "E279", {"start": v(14.66, 37.19) * mm, "end": v(14.58, 37.2) * mm});
            skLineSegment(sketch, "E280", {"start": v(14.58, 37.2) * mm, "end": v(14.5, 37.2) * mm});
            skLineSegment(sketch, "E281", {"start": v(14.5, 37.2) * mm, "end": v(14.42, 37.19) * mm});
            skLineSegment(sketch, "E282", {"start": v(14.42, 37.19) * mm, "end": v(14.35, 37.17) * mm});
            skLineSegment(sketch, "E283", {"start": v(14.35, 37.17) * mm, "end": v(14.27, 37.15) * mm});
            skLineSegment(sketch, "E284", {"start": v(14.27, 37.15) * mm, "end": v(14.2, 37.13) * mm});
            skLineSegment(sketch, "E285", {"start": v(14.2, 37.13) * mm, "end": v(14.12, 37.1) * mm});
            skLineSegment(sketch, "E286", {"start": v(14.12, 37.1) * mm, "end": v(14.03, 37.04) * mm});
            skLineSegment(sketch, "E287", {"start": v(14.03, 37.04) * mm, "end": v(13.95, 36.98) * mm});
            skLineSegment(sketch, "E288", {"start": v(13.95, 36.98) * mm, "end": v(13.88, 36.91) * mm});
            skLineSegment(sketch, "E289", {"start": v(13.88, 36.91) * mm, "end": v(13.81, 36.84) * mm});
            skLineSegment(sketch, "E290", {"start": v(13.81, 36.84) * mm, "end": v(13.75, 36.76) * mm});
            skLineSegment(sketch, "E291", {"start": v(13.75, 36.76) * mm, "end": v(13.7, 36.67) * mm});
            skLineSegment(sketch, "E292", {"start": v(13.7, 36.67) * mm, "end": v(13.67, 36.57) * mm});
            skLineSegment(sketch, "E293", {"start": v(13.67, 36.57) * mm, "end": v(13.64, 36.47) * mm});
            skLineSegment(sketch, "E294", {"start": v(13.64, 36.47) * mm, "end": v(13.63, 36.42) * mm});
            skLineSegment(sketch, "E295", {"start": v(13.63, 36.42) * mm, "end": v(13.63, 36.16) * mm});
            skLineSegment(sketch, "E296", {"start": v(13.63, 36.16) * mm, "end": v(13.64, 36.1) * mm});
            skLineSegment(sketch, "E297", {"start": v(13.64, 36.1) * mm, "end": v(13.66, 36.04) * mm});
            skLineSegment(sketch, "E298", {"start": v(13.66, 36.04) * mm, "end": v(13.68, 35.97) * mm});
            skLineSegment(sketch, "E299", {"start": v(13.68, 35.97) * mm, "end": v(13.7, 35.91) * mm});
            skLineSegment(sketch, "E300", {"start": v(13.7, 35.91) * mm, "end": v(13.73, 35.86) * mm});
            skLineSegment(sketch, "E301", {"start": v(13.73, 35.86) * mm, "end": v(13.76, 35.8) * mm});
            skLineSegment(sketch, "E302", {"start": v(13.76, 35.8) * mm, "end": v(13.8, 35.75) * mm});
            skLineSegment(sketch, "E303", {"start": v(13.8, 35.75) * mm, "end": v(13.84, 35.7) * mm});
            skLineSegment(sketch, "E304", {"start": v(13.84, 35.7) * mm, "end": v(13.89, 35.65) * mm});
            skLineSegment(sketch, "E305", {"start": v(13.89, 35.65) * mm, "end": v(13.94, 35.6) * mm});
            skLineSegment(sketch, "E306", {"start": v(13.94, 35.6) * mm, "end": v(14, 35.56) * mm});
            skLineSegment(sketch, "E307", {"start": v(14, 35.56) * mm, "end": v(14.05, 35.52) * mm});
            skLineSegment(sketch, "E308", {"start": v(14.05, 35.52) * mm, "end": v(14.11, 35.48) * mm});
            skLineSegment(sketch, "E309", {"start": v(14.11, 35.48) * mm, "end": v(14.17, 35.45) * mm});
            skLineSegment(sketch, "E310", {"start": v(14.17, 35.45) * mm, "end": v(14.24, 35.43) * mm});
            skLineSegment(sketch, "E311", {"start": v(14.24, 35.43) * mm, "end": v(14.3, 35.4) * mm});
            skLineSegment(sketch, "E312", {"start": v(14.3, 35.4) * mm, "end": v(14.38, 35.4) * mm});
            skLineSegment(sketch, "E313", {"start": v(5.58, 40.1) * mm, "end": v(5.88, 39.8) * mm});
            skLineSegment(sketch, "E314", {"start": v(5.88, 39.8) * mm, "end": v(5.88, 39.8) * mm});
            skLineSegment(sketch, "E315", {"start": v(5.88, 39.8) * mm, "end": v(7.12, 41.03) * mm});
            skLineSegment(sketch, "E316", {"start": v(7.12, 41.03) * mm, "end": v(5.98, 42.17) * mm});
            skLineSegment(sketch, "E317", {"start": v(5.98, 42.17) * mm, "end": v(5.94, 42.18) * mm});
            skLineSegment(sketch, "E318", {"start": v(5.94, 42.18) * mm, "end": v(5.9, 42.2) * mm});
            skLineSegment(sketch, "E319", {"start": v(5.9, 42.2) * mm, "end": v(5.84, 42.2) * mm});
            skLineSegment(sketch, "E320", {"start": v(5.84, 42.2) * mm, "end": v(5.78, 42.18) * mm});
            skLineSegment(sketch, "E321", {"start": v(5.78, 42.18) * mm, "end": v(5.73, 42.15) * mm});
            skLineSegment(sketch, "E322", {"start": v(5.73, 42.15) * mm, "end": v(5.7, 42.13) * mm});
            skLineSegment(sketch, "E323", {"start": v(5.7, 42.13) * mm, "end": v(5.68, 42.1) * mm});
            skLineSegment(sketch, "E324", {"start": v(5.68, 42.1) * mm, "end": v(5.67, 42.07) * mm});
            skLineSegment(sketch, "E325", {"start": v(5.67, 42.07) * mm, "end": v(5.66, 42.04) * mm});
            skLineSegment(sketch, "E326", {"start": v(5.66, 42.04) * mm, "end": v(5.65, 42) * mm});
            skLineSegment(sketch, "E327", {"start": v(5.65, 42) * mm, "end": v(5.66, 41.97) * mm});
            skLineSegment(sketch, "E328", {"start": v(5.66, 41.97) * mm, "end": v(5.66, 41.93) * mm});
            skLineSegment(sketch, "E329", {"start": v(5.66, 41.93) * mm, "end": v(5.67, 41.9) * mm});
            skLineSegment(sketch, "E330", {"start": v(5.67, 41.9) * mm, "end": v(5.73, 41.75) * mm});
            skLineSegment(sketch, "E331", {"start": v(5.73, 41.75) * mm, "end": v(5.78, 41.62) * mm});
            skLineSegment(sketch, "E332", {"start": v(5.78, 41.62) * mm, "end": v(5.82, 41.5) * mm});
            skLineSegment(sketch, "E333", {"start": v(5.82, 41.5) * mm, "end": v(5.85, 41.38) * mm});
            skLineSegment(sketch, "E334", {"start": v(5.85, 41.38) * mm, "end": v(5.88, 41.26) * mm});
            skLineSegment(sketch, "E335", {"start": v(5.88, 41.26) * mm, "end": v(5.9, 41.18) * mm});
            skLineSegment(sketch, "E336", {"start": v(5.9, 41.18) * mm, "end": v(5.9, 40.88) * mm});
            skLineSegment(sketch, "E337", {"start": v(5.9, 40.88) * mm, "end": v(5.88, 40.8) * mm});
            skLineSegment(sketch, "E338", {"start": v(5.88, 40.8) * mm, "end": v(5.85, 40.67) * mm});
            skLineSegment(sketch, "E339", {"start": v(5.85, 40.67) * mm, "end": v(5.81, 40.54) * mm});
            skLineSegment(sketch, "E340", {"start": v(5.81, 40.54) * mm, "end": v(5.76, 40.42) * mm});
            skLineSegment(sketch, "E341", {"start": v(5.76, 40.42) * mm, "end": v(5.7, 40.3) * mm});
            skLineSegment(sketch, "E342", {"start": v(5.7, 40.3) * mm, "end": v(5.68, 40.26) * mm});
            skLineSegment(sketch, "E343", {"start": v(5.68, 40.26) * mm, "end": v(5.68, 40.26) * mm});
            skLineSegment(sketch, "E344", {"start": v(5.68, 40.26) * mm, "end": v(5.68, 40.25) * mm});
            skLineSegment(sketch, "E345", {"start": v(5.68, 40.25) * mm, "end": v(5.67, 40.24) * mm});
            skLineSegment(sketch, "E346", {"start": v(5.67, 40.24) * mm, "end": v(5.58, 40.1) * mm});
            skLineSegment(sketch, "E347", {"start": v(5.58, 40.1) * mm, "end": v(5.58, 40.1) * mm});
            skLineSegment(sketch, "E348", {"start": v(-1.49, 39.87) * mm, "end": v(-1.5, 39.87) * mm});
            skLineSegment(sketch, "E349", {"start": v(-1.5, 39.87) * mm, "end": v(-1.5, 39.87) * mm});
            skLineSegment(sketch, "E350", {"start": v(-1.5, 39.87) * mm, "end": v(-1.49, 39.87) * mm});
            skLineSegment(sketch, "E351", {"start": v(-4.08, 41.2) * mm, "end": v(-4.08, 41.2) * mm});
            skLineSegment(sketch, "E352", {"start": v(-4.08, 41.2) * mm, "end": v(-4.09, 41.2) * mm});
            skLineSegment(sketch, "E353", {"start": v(-4.09, 41.2) * mm, "end": v(-4.08, 41.2) * mm});
            skLineSegment(sketch, "E354", {"start": v(3.94, 38.05) * mm, "end": v(3.97, 38.04) * mm});
            skLineSegment(sketch, "E355", {"start": v(3.97, 38.04) * mm, "end": v(4, 38.04) * mm});
            skLineSegment(sketch, "E356", {"start": v(4, 38.04) * mm, "end": v(4.05, 38.04) * mm});
            skLineSegment(sketch, "E357", {"start": v(4.05, 38.04) * mm, "end": v(4.08, 38.05) * mm});
            skLineSegment(sketch, "E358", {"start": v(4.08, 38.05) * mm, "end": v(4.12, 38.07) * mm});
            skLineSegment(sketch, "E359", {"start": v(4.12, 38.07) * mm, "end": v(4.16, 38.09) * mm});
            skLineSegment(sketch, "E360", {"start": v(4.16, 38.09) * mm, "end": v(4.2, 38.11) * mm});
            skLineSegment(sketch, "E361", {"start": v(4.2, 38.11) * mm, "end": v(5.64, 39.55) * mm});
            skLineSegment(sketch, "E362", {"start": v(5.64, 39.55) * mm, "end": v(1.62, 43.57) * mm});
            skLineSegment(sketch, "E363", {"start": v(1.62, 43.57) * mm, "end": v(0.17, 42.12) * mm});
            skLineSegment(sketch, "E364", {"start": v(0.17, 42.12) * mm, "end": v(0.18, 42.1) * mm});
            skLineSegment(sketch, "E365", {"start": v(0.18, 42.1) * mm, "end": v(0.18, 42.1) * mm});
            skLineSegment(sketch, "E366", {"start": v(0.18, 42.1) * mm, "end": v(0.17, 42.1) * mm});
            skLineSegment(sketch, "E367", {"start": v(0.17, 42.1) * mm, "end": v(0.16, 42.1) * mm});
            skLineSegment(sketch, "E368", {"start": v(0.16, 42.1) * mm, "end": v(0.15, 42.09) * mm});
            skLineSegment(sketch, "E369", {"start": v(0.15, 42.09) * mm, "end": v(0.13, 42.04) * mm});
            skLineSegment(sketch, "E370", {"start": v(0.13, 42.04) * mm, "end": v(0.11, 41.99) * mm});
            skLineSegment(sketch, "E371", {"start": v(0.11, 41.99) * mm, "end": v(0.1, 41.94) * mm});
            skLineSegment(sketch, "E372", {"start": v(0.1, 41.94) * mm, "end": v(0.12, 41.88) * mm});
            skLineSegment(sketch, "E373", {"start": v(0.12, 41.88) * mm, "end": v(0.12, 41.86) * mm});
            skLineSegment(sketch, "E374", {"start": v(0.12, 41.86) * mm, "end": v(0.13, 41.85) * mm});
            skLineSegment(sketch, "E375", {"start": v(0.13, 41.85) * mm, "end": v(0.14, 41.85) * mm});
            skLineSegment(sketch, "E376", {"start": v(0.14, 41.85) * mm, "end": v(0.13, 41.84) * mm});
            skLineSegment(sketch, "E377", {"start": v(0.13, 41.84) * mm, "end": v(0.14, 41.82) * mm});
            skLineSegment(sketch, "E378", {"start": v(0.14, 41.82) * mm, "end": v(0.17, 41.79) * mm});
            skLineSegment(sketch, "E379", {"start": v(0.17, 41.79) * mm, "end": v(0.2, 41.76) * mm});
            skLineSegment(sketch, "E380", {"start": v(0.2, 41.76) * mm, "end": v(0.25, 41.74) * mm});
            skLineSegment(sketch, "E381", {"start": v(0.25, 41.74) * mm, "end": v(0.3, 41.73) * mm});
            skLineSegment(sketch, "E382", {"start": v(0.3, 41.73) * mm, "end": v(0.34, 41.73) * mm});
            skLineSegment(sketch, "E383", {"start": v(0.34, 41.73) * mm, "end": v(0.4, 41.75) * mm});
            skLineSegment(sketch, "E384", {"start": v(0.4, 41.75) * mm, "end": v(0.46, 41.78) * mm});
            skLineSegment(sketch, "E385", {"start": v(0.46, 41.78) * mm, "end": v(0.55, 41.82) * mm});
            skLineSegment(sketch, "E386", {"start": v(0.55, 41.82) * mm, "end": v(0.58, 41.83) * mm});
            skLineSegment(sketch, "E387", {"start": v(0.58, 41.83) * mm, "end": v(0.63, 41.84) * mm});
            skLineSegment(sketch, "E388", {"start": v(0.63, 41.84) * mm, "end": v(0.67, 41.84) * mm});
            skLineSegment(sketch, "E389", {"start": v(0.67, 41.84) * mm, "end": v(0.7, 41.82) * mm});
            skLineSegment(sketch, "E390", {"start": v(0.7, 41.82) * mm, "end": v(0.75, 41.8) * mm});
            skLineSegment(sketch, "E391", {"start": v(0.75, 41.8) * mm, "end": v(0.78, 41.78) * mm});
            skLineSegment(sketch, "E392", {"start": v(0.78, 41.78) * mm, "end": v(3.87, 38.69) * mm});
            skLineSegment(sketch, "E393", {"start": v(3.87, 38.69) * mm, "end": v(3.89, 38.65) * mm});
            skLineSegment(sketch, "E394", {"start": v(3.89, 38.65) * mm, "end": v(3.9, 38.63) * mm});
            skLineSegment(sketch, "E395", {"start": v(3.9, 38.63) * mm, "end": v(3.9, 38.6) * mm});
            skLineSegment(sketch, "E396", {"start": v(3.9, 38.6) * mm, "end": v(3.9, 38.57) * mm});
            skLineSegment(sketch, "E397", {"start": v(3.9, 38.57) * mm, "end": v(3.9, 38.54) * mm});
            skLineSegment(sketch, "E398", {"start": v(3.9, 38.54) * mm, "end": v(3.88, 38.47) * mm});
            skLineSegment(sketch, "E399", {"start": v(3.88, 38.47) * mm, "end": v(3.84, 38.37) * mm});
            skLineSegment(sketch, "E400", {"start": v(3.84, 38.37) * mm, "end": v(3.82, 38.32) * mm});
            skLineSegment(sketch, "E401", {"start": v(3.82, 38.32) * mm, "end": v(3.8, 38.28) * mm});
            skLineSegment(sketch, "E402", {"start": v(3.8, 38.28) * mm, "end": v(3.8, 38.24) * mm});
            skLineSegment(sketch, "E403", {"start": v(3.8, 38.24) * mm, "end": v(3.8, 38.2) * mm});
            skLineSegment(sketch, "E404", {"start": v(3.8, 38.2) * mm, "end": v(3.81, 38.17) * mm});
            skLineSegment(sketch, "E405", {"start": v(3.81, 38.17) * mm, "end": v(3.83, 38.14) * mm});
            skLineSegment(sketch, "E406", {"start": v(3.83, 38.14) * mm, "end": v(3.85, 38.11) * mm});
            skLineSegment(sketch, "E407", {"start": v(3.85, 38.11) * mm, "end": v(3.87, 38.09) * mm});
            skLineSegment(sketch, "E408", {"start": v(3.87, 38.09) * mm, "end": v(3.9, 38.06) * mm});
            skLineSegment(sketch, "E409", {"start": v(3.9, 38.06) * mm, "end": v(3.94, 38.05) * mm});
            skLineSegment(sketch, "E410", {"start": v(-6.27, 37.75) * mm, "end": v(-6.2, 37.75) * mm});
            skLineSegment(sketch, "E411", {"start": v(-6.2, 37.75) * mm, "end": v(-6.11, 37.76) * mm});
            skLineSegment(sketch, "E412", {"start": v(-6.11, 37.76) * mm, "end": v(-6.06, 37.78) * mm});
            skLineSegment(sketch, "E413", {"start": v(-6.06, 37.78) * mm, "end": v(-6, 37.8) * mm});
            skLineSegment(sketch, "E414", {"start": v(-6, 37.8) * mm, "end": v(-5.95, 37.83) * mm});
            skLineSegment(sketch, "E415", {"start": v(-5.95, 37.83) * mm, "end": v(-5.9, 37.86) * mm});
            skLineSegment(sketch, "E416", {"start": v(-5.9, 37.86) * mm, "end": v(-5.86, 37.9) * mm});
            skLineSegment(sketch, "E417", {"start": v(-5.86, 37.9) * mm, "end": v(-3.12, 40.63) * mm});
            skLineSegment(sketch, "E418", {"start": v(-3.12, 40.63) * mm, "end": v(-3.08, 40.68) * mm});
            skLineSegment(sketch, "E419", {"start": v(-3.08, 40.68) * mm, "end": v(-3.03, 40.77) * mm});
            skLineSegment(sketch, "E420", {"start": v(-3.03, 40.77) * mm, "end": v(-3, 40.82) * mm});
            skLineSegment(sketch, "E421", {"start": v(-3, 40.82) * mm, "end": v(-2.98, 40.87) * mm});
            skLineSegment(sketch, "E422", {"start": v(-2.98, 40.87) * mm, "end": v(-2.97, 40.93) * mm});
            skLineSegment(sketch, "E423", {"start": v(-2.97, 40.93) * mm, "end": v(-2.96, 41) * mm});
            skLineSegment(sketch, "E424", {"start": v(-2.96, 41) * mm, "end": v(-2.97, 41.06) * mm});
            skLineSegment(sketch, "E425", {"start": v(-2.97, 41.06) * mm, "end": v(-2.98, 41.11) * mm});
            skLineSegment(sketch, "E426", {"start": v(-2.98, 41.11) * mm, "end": v(-3, 41.17) * mm});
            skLineSegment(sketch, "E427", {"start": v(-3, 41.17) * mm, "end": v(-3.05, 41.23) * mm});
            skLineSegment(sketch, "E428", {"start": v(-3.05, 41.23) * mm, "end": v(-3.1, 41.28) * mm});
            skLineSegment(sketch, "E429", {"start": v(-3.1, 41.28) * mm, "end": v(-3.15, 41.32) * mm});
            skLineSegment(sketch, "E430", {"start": v(-3.15, 41.32) * mm, "end": v(-3.18, 41.34) * mm});
            skLineSegment(sketch, "E431", {"start": v(-3.18, 41.34) * mm, "end": v(-3.21, 41.35) * mm});
            skLineSegment(sketch, "E432", {"start": v(-3.21, 41.35) * mm, "end": v(-3.29, 41.37) * mm});
            skLineSegment(sketch, "E433", {"start": v(-3.29, 41.37) * mm, "end": v(-3.37, 41.37) * mm});
            skLineSegment(sketch, "E434", {"start": v(-3.37, 41.37) * mm, "end": v(-3.4, 41.36) * mm});
            skLineSegment(sketch, "E435", {"start": v(-3.4, 41.36) * mm, "end": v(-3.44, 41.35) * mm});
            skLineSegment(sketch, "E436", {"start": v(-3.44, 41.35) * mm, "end": v(-3.5, 41.34) * mm});
            skLineSegment(sketch, "E437", {"start": v(-3.5, 41.34) * mm, "end": v(-3.59, 41.3) * mm});
            skLineSegment(sketch, "E438", {"start": v(-3.59, 41.3) * mm, "end": v(-3.68, 41.24) * mm});
            skLineSegment(sketch, "E439", {"start": v(-3.68, 41.24) * mm, "end": v(-3.77, 41.21) * mm});
            skLineSegment(sketch, "E440", {"start": v(-3.77, 41.21) * mm, "end": v(-3.84, 41.19) * mm});
            skLineSegment(sketch, "E441", {"start": v(-3.84, 41.19) * mm, "end": v(-3.9, 41.18) * mm});
            skLineSegment(sketch, "E442", {"start": v(-3.9, 41.18) * mm, "end": v(-3.96, 41.18) * mm});
            skLineSegment(sketch, "E443", {"start": v(-3.96, 41.18) * mm, "end": v(-4.01, 41.2) * mm});
            skLineSegment(sketch, "E444", {"start": v(-4.01, 41.2) * mm, "end": v(-4.06, 41.22) * mm});
            skLineSegment(sketch, "E445", {"start": v(-4.06, 41.22) * mm, "end": v(-4.12, 41.25) * mm});
            skLineSegment(sketch, "E446", {"start": v(-4.12, 41.25) * mm, "end": v(-4.18, 41.3) * mm});
            skLineSegment(sketch, "E447", {"start": v(-4.18, 41.3) * mm, "end": v(-9.58, 46.7) * mm});
            skLineSegment(sketch, "E448", {"start": v(-9.58, 46.7) * mm, "end": v(-9.62, 46.75) * mm});
            skLineSegment(sketch, "E449", {"start": v(-9.62, 46.75) * mm, "end": v(-9.66, 46.8) * mm});
            skLineSegment(sketch, "E450", {"start": v(-9.66, 46.8) * mm, "end": v(-9.7, 46.86) * mm});
            skLineSegment(sketch, "E451", {"start": v(-9.7, 46.86) * mm, "end": v(-9.7, 46.89) * mm});
            skLineSegment(sketch, "E452", {"start": v(-9.7, 46.89) * mm, "end": v(-9.71, 46.91) * mm});
            skLineSegment(sketch, "E453", {"start": v(-9.71, 46.91) * mm, "end": v(-9.72, 46.98) * mm});
            skLineSegment(sketch, "E454", {"start": v(-9.72, 46.98) * mm, "end": v(-9.71, 47.06) * mm});
            skLineSegment(sketch, "E455", {"start": v(-9.71, 47.06) * mm, "end": v(-9.7, 47.12) * mm});
            skLineSegment(sketch, "E456", {"start": v(-9.7, 47.12) * mm, "end": v(-9.67, 47.2) * mm});
            skLineSegment(sketch, "E457", {"start": v(-9.67, 47.2) * mm, "end": v(-9.56, 47.42) * mm});
            skLineSegment(sketch, "E458", {"start": v(-9.56, 47.42) * mm, "end": v(-9.54, 47.47) * mm});
            skLineSegment(sketch, "E459", {"start": v(-9.54, 47.47) * mm, "end": v(-9.53, 47.54) * mm});
            skLineSegment(sketch, "E460", {"start": v(-9.53, 47.54) * mm, "end": v(-9.53, 47.61) * mm});
            skLineSegment(sketch, "E461", {"start": v(-9.53, 47.61) * mm, "end": v(-9.55, 47.68) * mm});
            skLineSegment(sketch, "E462", {"start": v(-9.55, 47.68) * mm, "end": v(-9.57, 47.74) * mm});
            skLineSegment(sketch, "E463", {"start": v(-9.57, 47.74) * mm, "end": v(-9.6, 47.78) * mm});
            skLineSegment(sketch, "E464", {"start": v(-9.6, 47.78) * mm, "end": v(-9.64, 47.82) * mm});
            skLineSegment(sketch, "E465", {"start": v(-9.64, 47.82) * mm, "end": v(-9.67, 47.86) * mm});
            skLineSegment(sketch, "E466", {"start": v(-9.67, 47.86) * mm, "end": v(-9.72, 47.88) * mm});
            skLineSegment(sketch, "E467", {"start": v(-9.72, 47.88) * mm, "end": v(-9.76, 47.9) * mm});
            skLineSegment(sketch, "E468", {"start": v(-9.76, 47.9) * mm, "end": v(-9.8, 47.92) * mm});
            skLineSegment(sketch, "E469", {"start": v(-9.8, 47.92) * mm, "end": v(-9.85, 47.93) * mm});
            skLineSegment(sketch, "E470", {"start": v(-9.85, 47.93) * mm, "end": v(-9.9, 47.94) * mm});
            skLineSegment(sketch, "E471", {"start": v(-9.9, 47.94) * mm, "end": v(-9.97, 47.93) * mm});
            skLineSegment(sketch, "E472", {"start": v(-9.97, 47.93) * mm, "end": v(-10.04, 47.91) * mm});
            skLineSegment(sketch, "E473", {"start": v(-10.04, 47.91) * mm, "end": v(-10.12, 47.88) * mm});
            skLineSegment(sketch, "E474", {"start": v(-10.12, 47.88) * mm, "end": v(-10.2, 47.84) * mm});
            skLineSegment(sketch, "E475", {"start": v(-10.2, 47.84) * mm, "end": v(-10.24, 47.8) * mm});
            skLineSegment(sketch, "E476", {"start": v(-10.24, 47.8) * mm, "end": v(-13, 45.05) * mm});
            skLineSegment(sketch, "E477", {"start": v(-13, 45.05) * mm, "end": v(-13.03, 45) * mm});
            skLineSegment(sketch, "E478", {"start": v(-13.03, 45) * mm, "end": v(-13.07, 44.95) * mm});
            skLineSegment(sketch, "E479", {"start": v(-13.07, 44.95) * mm, "end": v(-13.1, 44.9) * mm});
            skLineSegment(sketch, "E480", {"start": v(-13.1, 44.9) * mm, "end": v(-13.12, 44.85) * mm});
            skLineSegment(sketch, "E481", {"start": v(-13.12, 44.85) * mm, "end": v(-13.14, 44.8) * mm});
            skLineSegment(sketch, "E482", {"start": v(-13.14, 44.8) * mm, "end": v(-13.15, 44.74) * mm});
            skLineSegment(sketch, "E483", {"start": v(-13.15, 44.74) * mm, "end": v(-13.15, 44.7) * mm});
            skLineSegment(sketch, "E484", {"start": v(-13.15, 44.7) * mm, "end": v(-13.15, 44.64) * mm});
            skLineSegment(sketch, "E485", {"start": v(-13.15, 44.64) * mm, "end": v(-13.14, 44.6) * mm});
            skLineSegment(sketch, "E486", {"start": v(-13.14, 44.6) * mm, "end": v(-13.12, 44.52) * mm});
            skLineSegment(sketch, "E487", {"start": v(-13.12, 44.52) * mm, "end": v(-13.1, 44.5) * mm});
            skLineSegment(sketch, "E488", {"start": v(-13.1, 44.5) * mm, "end": v(-13.1, 44.5) * mm});
            skLineSegment(sketch, "E489", {"start": v(-13.1, 44.5) * mm, "end": v(-13.09, 44.5) * mm});
            skLineSegment(sketch, "E490", {"start": v(-13.09, 44.5) * mm, "end": v(-13.1, 44.49) * mm});
            skLineSegment(sketch, "E491", {"start": v(-13.1, 44.49) * mm, "end": v(-13.1, 44.48) * mm});
            skLineSegment(sketch, "E492", {"start": v(-13.1, 44.48) * mm, "end": v(-13.05, 44.43) * mm});
            skLineSegment(sketch, "E493", {"start": v(-13.05, 44.43) * mm, "end": v(-13.01, 44.4) * mm});
            skLineSegment(sketch, "E494", {"start": v(-13.01, 44.4) * mm, "end": v(-12.97, 44.37) * mm});
            skLineSegment(sketch, "E495", {"start": v(-12.97, 44.37) * mm, "end": v(-12.94, 44.35) * mm});
            skLineSegment(sketch, "E496", {"start": v(-12.94, 44.35) * mm, "end": v(-12.9, 44.33) * mm});
            skLineSegment(sketch, "E497", {"start": v(-12.9, 44.33) * mm, "end": v(-12.85, 44.32) * mm});
            skLineSegment(sketch, "E498", {"start": v(-12.85, 44.32) * mm, "end": v(-12.8, 44.31) * mm});
            skLineSegment(sketch, "E499", {"start": v(-12.8, 44.31) * mm, "end": v(-12.75, 44.32) * mm});
            skLineSegment(sketch, "E500", {"start": v(-12.75, 44.32) * mm, "end": v(-12.7, 44.32) * mm});
            skLineSegment(sketch, "E501", {"start": v(-12.7, 44.32) * mm, "end": v(-12.65, 44.33) * mm});
            skLineSegment(sketch, "E502", {"start": v(-12.65, 44.33) * mm, "end": v(-12.39, 44.46) * mm});
            skLineSegment(sketch, "E503", {"start": v(-12.39, 44.46) * mm, "end": v(-12.33, 44.48) * mm});
            skLineSegment(sketch, "E504", {"start": v(-12.33, 44.48) * mm, "end": v(-12.27, 44.5) * mm});
            skLineSegment(sketch, "E505", {"start": v(-12.27, 44.5) * mm, "end": v(-12.22, 44.5) * mm});
            skLineSegment(sketch, "E506", {"start": v(-12.22, 44.5) * mm, "end": v(-12.16, 44.5) * mm});
            skLineSegment(sketch, "E507", {"start": v(-12.16, 44.5) * mm, "end": v(-12.12, 44.5) * mm});
            skLineSegment(sketch, "E508", {"start": v(-12.12, 44.5) * mm, "end": v(-12.07, 44.47) * mm});
            skLineSegment(sketch, "E509", {"start": v(-12.07, 44.47) * mm, "end": v(-12.02, 44.44) * mm});
            skLineSegment(sketch, "E510", {"start": v(-12.02, 44.44) * mm, "end": v(-11.96, 44.4) * mm});
            skLineSegment(sketch, "E511", {"start": v(-11.96, 44.4) * mm, "end": v(-11.9, 44.34) * mm});
            skLineSegment(sketch, "E512", {"start": v(-11.9, 44.34) * mm, "end": v(-11.81, 44.26) * mm});
            skLineSegment(sketch, "E513", {"start": v(-11.81, 44.26) * mm, "end": v(-9.56, 42.01) * mm});
            skLineSegment(sketch, "E514", {"start": v(-9.56, 42.01) * mm, "end": v(-9.57, 42) * mm});
            skLineSegment(sketch, "E515", {"start": v(-9.57, 42) * mm, "end": v(-10.4, 41.17) * mm});
            skLineSegment(sketch, "E516", {"start": v(-10.4, 41.17) * mm, "end": v(-9.94, 40.7) * mm});
            skLineSegment(sketch, "E517", {"start": v(-9.94, 40.7) * mm, "end": v(-9.85, 40.61) * mm});
            skLineSegment(sketch, "E518", {"start": v(-9.85, 40.61) * mm, "end": v(-9.01, 41.45) * mm});
            skLineSegment(sketch, "E519", {"start": v(-9.01, 41.45) * mm, "end": v(-9, 41.45) * mm});
            skLineSegment(sketch, "E520", {"start": v(-9, 41.45) * mm, "end": v(-6.54, 38.99) * mm});
            skLineSegment(sketch, "E521", {"start": v(-6.54, 38.99) * mm, "end": v(-6.5, 38.94) * mm});
            skLineSegment(sketch, "E522", {"start": v(-6.5, 38.94) * mm, "end": v(-6.43, 38.85) * mm});
            skLineSegment(sketch, "E523", {"start": v(-6.43, 38.85) * mm, "end": v(-6.4, 38.8) * mm});
            skLineSegment(sketch, "E524", {"start": v(-6.4, 38.8) * mm, "end": v(-6.4, 38.8) * mm});
            skLineSegment(sketch, "E525", {"start": v(-6.4, 38.8) * mm, "end": v(-6.4, 38.75) * mm});
            skLineSegment(sketch, "E526", {"start": v(-6.4, 38.75) * mm, "end": v(-6.4, 38.71) * mm});
            skLineSegment(sketch, "E527", {"start": v(-6.4, 38.71) * mm, "end": v(-6.4, 38.68) * mm});
            skLineSegment(sketch, "E528", {"start": v(-6.4, 38.68) * mm, "end": v(-6.41, 38.6) * mm});
            skLineSegment(sketch, "E529", {"start": v(-6.41, 38.6) * mm, "end": v(-6.45, 38.5) * mm});
            skLineSegment(sketch, "E530", {"start": v(-6.45, 38.5) * mm, "end": v(-6.5, 38.37) * mm});
            skLineSegment(sketch, "E531", {"start": v(-6.5, 38.37) * mm, "end": v(-6.55, 38.28) * mm});
            skLineSegment(sketch, "E532", {"start": v(-6.55, 38.28) * mm, "end": v(-6.57, 38.23) * mm});
            skLineSegment(sketch, "E533", {"start": v(-6.57, 38.23) * mm, "end": v(-6.58, 38.18) * mm});
            skLineSegment(sketch, "E534", {"start": v(-6.58, 38.18) * mm, "end": v(-6.59, 38.13) * mm});
            skLineSegment(sketch, "E535", {"start": v(-6.59, 38.13) * mm, "end": v(-6.59, 38.08) * mm});
            skLineSegment(sketch, "E536", {"start": v(-6.59, 38.08) * mm, "end": v(-6.58, 38.04) * mm});
            skLineSegment(sketch, "E537", {"start": v(-6.58, 38.04) * mm, "end": v(-6.57, 38) * mm});
            skLineSegment(sketch, "E538", {"start": v(-6.57, 38) * mm, "end": v(-6.55, 37.95) * mm});
            skLineSegment(sketch, "E539", {"start": v(-6.55, 37.95) * mm, "end": v(-6.53, 37.92) * mm});
            skLineSegment(sketch, "E540", {"start": v(-6.53, 37.92) * mm, "end": v(-6.52, 37.92) * mm});
            skLineSegment(sketch, "E541", {"start": v(-6.52, 37.92) * mm, "end": v(-6.52, 37.91) * mm});
            skLineSegment(sketch, "E542", {"start": v(-6.52, 37.91) * mm, "end": v(-6.52, 37.92) * mm});
            skLineSegment(sketch, "E543", {"start": v(-6.52, 37.91) * mm, "end": v(-6.52, 37.9) * mm});
            skLineSegment(sketch, "E544", {"start": v(-6.52, 37.9) * mm, "end": v(-6.51, 37.9) * mm});
            skLineSegment(sketch, "E545", {"start": v(-6.51, 37.9) * mm, "end": v(-6.5, 37.9) * mm});
            skLineSegment(sketch, "E546", {"start": v(-6.5, 37.9) * mm, "end": v(-6.5, 37.89) * mm});
            skLineSegment(sketch, "E547", {"start": v(-6.5, 37.89) * mm, "end": v(-6.5, 37.88) * mm});
            skLineSegment(sketch, "E548", {"start": v(-6.5, 37.88) * mm, "end": v(-6.47, 37.85) * mm});
            skLineSegment(sketch, "E549", {"start": v(-6.47, 37.85) * mm, "end": v(-6.42, 37.8) * mm});
            skLineSegment(sketch, "E550", {"start": v(-6.42, 37.8) * mm, "end": v(-6.37, 37.78) * mm});
            skLineSegment(sketch, "E551", {"start": v(-6.37, 37.78) * mm, "end": v(-6.32, 37.76) * mm});
            skLineSegment(sketch, "E552", {"start": v(-6.32, 37.76) * mm, "end": v(-6.27, 37.75) * mm});
            skLineSegment(sketch, "E553", {"start": v(7.27, 41.35) * mm, "end": v(7.3, 41.34) * mm});
            skLineSegment(sketch, "E554", {"start": v(7.3, 41.34) * mm, "end": v(7.35, 41.34) * mm});
            skLineSegment(sketch, "E555", {"start": v(7.35, 41.34) * mm, "end": v(7.4, 41.35) * mm});
            skLineSegment(sketch, "E556", {"start": v(7.4, 41.35) * mm, "end": v(7.43, 41.36) * mm});
            skLineSegment(sketch, "E557", {"start": v(7.43, 41.36) * mm, "end": v(7.46, 41.38) * mm});
            skLineSegment(sketch, "E558", {"start": v(7.46, 41.38) * mm, "end": v(9.04, 42.96) * mm});
            skLineSegment(sketch, "E559", {"start": v(9.04, 42.96) * mm, "end": v(9.07, 43) * mm});
            skLineSegment(sketch, "E560", {"start": v(9.07, 43) * mm, "end": v(9.09, 43.04) * mm});
            skLineSegment(sketch, "E561", {"start": v(9.09, 43.04) * mm, "end": v(9.1, 43.08) * mm});
            skLineSegment(sketch, "E562", {"start": v(9.1, 43.08) * mm, "end": v(9.1, 43.11) * mm});
            skLineSegment(sketch, "E563", {"start": v(9.1, 43.11) * mm, "end": v(9.11, 43.15) * mm});
            skLineSegment(sketch, "E564", {"start": v(9.11, 43.15) * mm, "end": v(9.1, 43.19) * mm});
            skLineSegment(sketch, "E565", {"start": v(9.1, 43.19) * mm, "end": v(9.1, 43.22) * mm});
            skLineSegment(sketch, "E566", {"start": v(9.1, 43.22) * mm, "end": v(9.08, 43.25) * mm});
            skLineSegment(sketch, "E567", {"start": v(9.08, 43.25) * mm, "end": v(9.05, 43.28) * mm});
            skLineSegment(sketch, "E568", {"start": v(9.05, 43.28) * mm, "end": v(9, 43.32) * mm});
            skLineSegment(sketch, "E569", {"start": v(9, 43.32) * mm, "end": v(8.96, 43.34) * mm});
            skLineSegment(sketch, "E570", {"start": v(8.96, 43.34) * mm, "end": v(8.91, 43.35) * mm});
            skLineSegment(sketch, "E571", {"start": v(8.91, 43.35) * mm, "end": v(8.86, 43.34) * mm});
            skLineSegment(sketch, "E572", {"start": v(8.86, 43.34) * mm, "end": v(8.83, 43.33) * mm});
            skLineSegment(sketch, "E573", {"start": v(8.83, 43.33) * mm, "end": v(8.75, 43.3) * mm});
            skLineSegment(sketch, "E574", {"start": v(8.75, 43.3) * mm, "end": v(8.68, 43.26) * mm});
            skLineSegment(sketch, "E575", {"start": v(8.68, 43.26) * mm, "end": v(8.62, 43.25) * mm});
            skLineSegment(sketch, "E576", {"start": v(8.62, 43.25) * mm, "end": v(8.57, 43.24) * mm});
            skLineSegment(sketch, "E577", {"start": v(8.57, 43.24) * mm, "end": v(8.52, 43.25) * mm});
            skLineSegment(sketch, "E578", {"start": v(8.52, 43.25) * mm, "end": v(8.5, 43.25) * mm});
            skLineSegment(sketch, "E579", {"start": v(8.5, 43.25) * mm, "end": v(8.46, 43.28) * mm});
            skLineSegment(sketch, "E580", {"start": v(8.46, 43.28) * mm, "end": v(8.43, 43.3) * mm});
            skLineSegment(sketch, "E581", {"start": v(8.43, 43.3) * mm, "end": v(4.9, 46.84) * mm});
            skLineSegment(sketch, "E582", {"start": v(4.9, 46.84) * mm, "end": v(3.9, 45.84) * mm});
            skLineSegment(sketch, "E583", {"start": v(3.9, 45.84) * mm, "end": v(3.46, 45.4) * mm});
            skLineSegment(sketch, "E584", {"start": v(3.46, 45.4) * mm, "end": v(3.43, 45.37) * mm});
            skLineSegment(sketch, "E585", {"start": v(3.43, 45.37) * mm, "end": v(3.4, 45.33) * mm});
            skLineSegment(sketch, "E586", {"start": v(3.4, 45.33) * mm, "end": v(3.4, 45.29) * mm});
            skLineSegment(sketch, "E587", {"start": v(3.4, 45.29) * mm, "end": v(3.38, 45.25) * mm});
            skLineSegment(sketch, "E588", {"start": v(3.38, 45.25) * mm, "end": v(3.38, 45.2) * mm});
            skLineSegment(sketch, "E589", {"start": v(3.38, 45.2) * mm, "end": v(3.38, 45.16) * mm});
            skLineSegment(sketch, "E590", {"start": v(3.38, 45.16) * mm, "end": v(3.4, 45.12) * mm});
            skLineSegment(sketch, "E591", {"start": v(3.4, 45.12) * mm, "end": v(3.42, 45.09) * mm});
            skLineSegment(sketch, "E592", {"start": v(3.42, 45.09) * mm, "end": v(3.45, 45.06) * mm});
            skLineSegment(sketch, "E593", {"start": v(3.45, 45.06) * mm, "end": v(3.48, 45.03) * mm});
            skLineSegment(sketch, "E594", {"start": v(3.48, 45.03) * mm, "end": v(3.51, 45.01) * mm});
            skLineSegment(sketch, "E595", {"start": v(3.51, 45.01) * mm, "end": v(3.54, 45) * mm});
            skLineSegment(sketch, "E596", {"start": v(3.54, 45) * mm, "end": v(3.59, 45) * mm});
            skLineSegment(sketch, "E597", {"start": v(3.59, 45) * mm, "end": v(3.62, 45) * mm});
            skLineSegment(sketch, "E598", {"start": v(3.62, 45) * mm, "end": v(3.65, 45.01) * mm});
            skLineSegment(sketch, "E599", {"start": v(3.65, 45.01) * mm, "end": v(3.73, 45.05) * mm});
            skLineSegment(sketch, "E600", {"start": v(3.73, 45.05) * mm, "end": v(3.82, 45.09) * mm});
            skLineSegment(sketch, "E601", {"start": v(3.82, 45.09) * mm, "end": v(3.86, 45.1) * mm});
            skLineSegment(sketch, "E602", {"start": v(3.86, 45.1) * mm, "end": v(3.9, 45.1) * mm});
            skLineSegment(sketch, "E603", {"start": v(3.9, 45.1) * mm, "end": v(3.93, 45.1) * mm});
            skLineSegment(sketch, "E604", {"start": v(3.93, 45.1) * mm, "end": v(3.97, 45.1) * mm});
            skLineSegment(sketch, "E605", {"start": v(3.97, 45.1) * mm, "end": v(4, 45.09) * mm});
            skLineSegment(sketch, "E606", {"start": v(4, 45.09) * mm, "end": v(4.02, 45.08) * mm});
            skLineSegment(sketch, "E607", {"start": v(4.02, 45.08) * mm, "end": v(4.03, 45.07) * mm});
            skLineSegment(sketch, "E608", {"start": v(4.03, 45.07) * mm, "end": v(4.04, 45.07) * mm});
            skLineSegment(sketch, "E609", {"start": v(4.04, 45.07) * mm, "end": v(4.04, 45.07) * mm});
            skLineSegment(sketch, "E610", {"start": v(4.04, 45.07) * mm, "end": v(4.04, 45.05) * mm});
            skLineSegment(sketch, "E611", {"start": v(4.04, 45.05) * mm, "end": v(4.06, 45.04) * mm});
            skLineSegment(sketch, "E612", {"start": v(4.06, 45.04) * mm, "end": v(4.06, 45.04) * mm});
            skLineSegment(sketch, "E613", {"start": v(4.06, 45.04) * mm, "end": v(7.15, 41.96) * mm});
            skLineSegment(sketch, "E614", {"start": v(7.15, 41.96) * mm, "end": v(7.17, 41.93) * mm});
            skLineSegment(sketch, "E615", {"start": v(7.17, 41.93) * mm, "end": v(7.19, 41.9) * mm});
            skLineSegment(sketch, "E616", {"start": v(7.19, 41.9) * mm, "end": v(7.2, 41.88) * mm});
            skLineSegment(sketch, "E617", {"start": v(7.2, 41.88) * mm, "end": v(7.2, 41.85) * mm});
            skLineSegment(sketch, "E618", {"start": v(7.2, 41.85) * mm, "end": v(7.2, 41.82) * mm});
            skLineSegment(sketch, "E619", {"start": v(7.2, 41.82) * mm, "end": v(7.19, 41.78) * mm});
            skLineSegment(sketch, "E620", {"start": v(7.19, 41.78) * mm, "end": v(7.12, 41.62) * mm});
            skLineSegment(sketch, "E621", {"start": v(7.12, 41.62) * mm, "end": v(7.1, 41.6) * mm});
            skLineSegment(sketch, "E622", {"start": v(7.1, 41.6) * mm, "end": v(7.1, 41.56) * mm});
            skLineSegment(sketch, "E623", {"start": v(7.1, 41.56) * mm, "end": v(7.11, 41.52) * mm});
            skLineSegment(sketch, "E624", {"start": v(7.11, 41.52) * mm, "end": v(7.12, 41.48) * mm});
            skLineSegment(sketch, "E625", {"start": v(7.12, 41.48) * mm, "end": v(7.14, 41.45) * mm});
            skLineSegment(sketch, "E626", {"start": v(7.14, 41.45) * mm, "end": v(7.17, 41.42) * mm});
            skLineSegment(sketch, "E627", {"start": v(7.17, 41.42) * mm, "end": v(7.2, 41.4) * mm});
            skLineSegment(sketch, "E628", {"start": v(7.2, 41.4) * mm, "end": v(7.23, 41.37) * mm});
            skLineSegment(sketch, "E629", {"start": v(7.23, 41.37) * mm, "end": v(7.27, 41.35) * mm});
            skLineSegment(sketch, "E630", {"start": v(4.95, 41.54) * mm, "end": v(5, 41.52) * mm});
            skLineSegment(sketch, "E631", {"start": v(5, 41.52) * mm, "end": v(5.04, 41.52) * mm});
            skLineSegment(sketch, "E632", {"start": v(5.04, 41.52) * mm, "end": v(5.08, 41.52) * mm});
            skLineSegment(sketch, "E633", {"start": v(5.08, 41.52) * mm, "end": v(5.12, 41.54) * mm});
            skLineSegment(sketch, "E634", {"start": v(5.12, 41.54) * mm, "end": v(5.16, 41.56) * mm});
            skLineSegment(sketch, "E635", {"start": v(5.16, 41.56) * mm, "end": v(5.2, 41.6) * mm});
            skLineSegment(sketch, "E636", {"start": v(5.2, 41.6) * mm, "end": v(5.22, 41.63) * mm});
            skLineSegment(sketch, "E637", {"start": v(5.22, 41.63) * mm, "end": v(5.24, 41.66) * mm});
            skLineSegment(sketch, "E638", {"start": v(5.24, 41.66) * mm, "end": v(5.25, 41.7) * mm});
            skLineSegment(sketch, "E639", {"start": v(5.25, 41.7) * mm, "end": v(5.24, 41.73) * mm});
            skLineSegment(sketch, "E640", {"start": v(5.24, 41.73) * mm, "end": v(5.24, 41.77) * mm});
            skLineSegment(sketch, "E641", {"start": v(5.24, 41.77) * mm, "end": v(5.22, 41.8) * mm});
            skLineSegment(sketch, "E642", {"start": v(5.22, 41.8) * mm, "end": v(5.2, 41.84) * mm});
            skLineSegment(sketch, "E643", {"start": v(5.2, 41.84) * mm, "end": v(3.84, 43.2) * mm});
            skLineSegment(sketch, "E644", {"start": v(3.84, 43.2) * mm, "end": v(3.82, 43.22) * mm});
            skLineSegment(sketch, "E645", {"start": v(3.82, 43.22) * mm, "end": v(3.77, 43.25) * mm});
            skLineSegment(sketch, "E646", {"start": v(3.77, 43.25) * mm, "end": v(3.72, 43.27) * mm});
            skLineSegment(sketch, "E647", {"start": v(3.72, 43.27) * mm, "end": v(3.67, 43.27) * mm});
            skLineSegment(sketch, "E648", {"start": v(3.67, 43.27) * mm, "end": v(3.63, 43.26) * mm});
            skLineSegment(sketch, "E649", {"start": v(3.63, 43.26) * mm, "end": v(3.58, 43.23) * mm});
            skLineSegment(sketch, "E650", {"start": v(3.58, 43.23) * mm, "end": v(3.54, 43.19) * mm});
            skLineSegment(sketch, "E651", {"start": v(3.54, 43.19) * mm, "end": v(3.5, 43.14) * mm});
            skLineSegment(sketch, "E652", {"start": v(3.5, 43.14) * mm, "end": v(3.5, 43.08) * mm});
            skLineSegment(sketch, "E653", {"start": v(3.5, 43.08) * mm, "end": v(3.5, 43.04) * mm});
            skLineSegment(sketch, "E654", {"start": v(3.5, 43.04) * mm, "end": v(3.5, 42.99) * mm});
            skLineSegment(sketch, "E655", {"start": v(3.5, 42.99) * mm, "end": v(3.53, 42.93) * mm});
            skLineSegment(sketch, "E656", {"start": v(3.53, 42.93) * mm, "end": v(3.56, 42.87) * mm});
            skLineSegment(sketch, "E657", {"start": v(3.56, 42.87) * mm, "end": v(3.64, 42.72) * mm});
            skLineSegment(sketch, "E658", {"start": v(3.64, 42.72) * mm, "end": v(3.68, 42.64) * mm});
            skLineSegment(sketch, "E659", {"start": v(3.68, 42.64) * mm, "end": v(3.69, 42.62) * mm});
            skLineSegment(sketch, "E660", {"start": v(3.69, 42.62) * mm, "end": v(3.7, 42.57) * mm});
            skLineSegment(sketch, "E661", {"start": v(3.7, 42.57) * mm, "end": v(3.72, 42.5) * mm});
            skLineSegment(sketch, "E662", {"start": v(3.72, 42.5) * mm, "end": v(3.73, 42.44) * mm});
            skLineSegment(sketch, "E663", {"start": v(3.73, 42.44) * mm, "end": v(3.74, 42.37) * mm});
            skLineSegment(sketch, "E664", {"start": v(3.74, 42.37) * mm, "end": v(3.74, 42.3) * mm});
            skLineSegment(sketch, "E665", {"start": v(3.74, 42.3) * mm, "end": v(3.73, 42.24) * mm});
            skLineSegment(sketch, "E666", {"start": v(3.73, 42.24) * mm, "end": v(3.72, 42.18) * mm});
            skLineSegment(sketch, "E667", {"start": v(3.72, 42.18) * mm, "end": v(3.7, 42.12) * mm});
            skLineSegment(sketch, "E668", {"start": v(3.7, 42.12) * mm, "end": v(3.68, 42.07) * mm});
            skLineSegment(sketch, "E669", {"start": v(3.68, 42.07) * mm, "end": v(3.66, 42.02) * mm});
            skLineSegment(sketch, "E670", {"start": v(3.66, 42.02) * mm, "end": v(3.99, 41.69) * mm});
            skLineSegment(sketch, "E671", {"start": v(3.99, 41.69) * mm, "end": v(4, 41.7) * mm});
            skLineSegment(sketch, "E672", {"start": v(4, 41.7) * mm, "end": v(4, 41.7) * mm});
            skLineSegment(sketch, "E673", {"start": v(4, 41.7) * mm, "end": v(4.01, 41.7) * mm});
            skLineSegment(sketch, "E674", {"start": v(4.01, 41.7) * mm, "end": v(4.03, 41.7) * mm});
            skLineSegment(sketch, "E675", {"start": v(4.03, 41.7) * mm, "end": v(4.05, 41.72) * mm});
            skLineSegment(sketch, "E676", {"start": v(4.05, 41.72) * mm, "end": v(4.11, 41.74) * mm});
            skLineSegment(sketch, "E677", {"start": v(4.11, 41.74) * mm, "end": v(4.17, 41.76) * mm});
            skLineSegment(sketch, "E678", {"start": v(4.17, 41.76) * mm, "end": v(4.23, 41.76) * mm});
            skLineSegment(sketch, "E679", {"start": v(4.23, 41.76) * mm, "end": v(4.3, 41.77) * mm});
            skLineSegment(sketch, "E680", {"start": v(4.3, 41.77) * mm, "end": v(4.36, 41.76) * mm});
            skLineSegment(sketch, "E681", {"start": v(4.36, 41.76) * mm, "end": v(4.42, 41.76) * mm});
            skLineSegment(sketch, "E682", {"start": v(4.42, 41.76) * mm, "end": v(4.48, 41.75) * mm});
            skLineSegment(sketch, "E683", {"start": v(4.48, 41.75) * mm, "end": v(4.54, 41.73) * mm});
            skLineSegment(sketch, "E684", {"start": v(4.54, 41.73) * mm, "end": v(4.6, 41.7) * mm});
            skLineSegment(sketch, "E685", {"start": v(4.6, 41.7) * mm, "end": v(4.67, 41.68) * mm});
            skLineSegment(sketch, "E686", {"start": v(4.67, 41.68) * mm, "end": v(4.83, 41.6) * mm});
            skLineSegment(sketch, "E687", {"start": v(4.83, 41.6) * mm, "end": v(4.9, 41.56) * mm});
            skLineSegment(sketch, "E688", {"start": v(4.9, 41.56) * mm, "end": v(4.95, 41.54) * mm});
            skLineSegment(sketch, "E689", {"start": v(1.87, 43.81) * mm, "end": v(2.17, 43.5) * mm});
            skLineSegment(sketch, "E690", {"start": v(2.17, 43.5) * mm, "end": v(2.18, 43.5) * mm});
            skLineSegment(sketch, "E691", {"start": v(2.18, 43.5) * mm, "end": v(2.26, 43.56) * mm});
            skLineSegment(sketch, "E692", {"start": v(2.26, 43.56) * mm, "end": v(2.34, 43.61) * mm});
            skLineSegment(sketch, "E693", {"start": v(2.34, 43.61) * mm, "end": v(2.42, 43.66) * mm});
            skLineSegment(sketch, "E694", {"start": v(2.42, 43.66) * mm, "end": v(2.5, 43.7) * mm});
            skLineSegment(sketch, "E695", {"start": v(2.5, 43.7) * mm, "end": v(2.59, 43.73) * mm});
            skLineSegment(sketch, "E696", {"start": v(2.59, 43.73) * mm, "end": v(2.67, 43.76) * mm});
            skLineSegment(sketch, "E697", {"start": v(2.67, 43.76) * mm, "end": v(2.75, 43.78) * mm});
            skLineSegment(sketch, "E698", {"start": v(2.75, 43.78) * mm, "end": v(2.83, 43.8) * mm});
            skLineSegment(sketch, "E699", {"start": v(2.83, 43.8) * mm, "end": v(2.92, 43.81) * mm});
            skLineSegment(sketch, "E700", {"start": v(2.92, 43.81) * mm, "end": v(3, 43.82) * mm});
            skLineSegment(sketch, "E701", {"start": v(3, 43.82) * mm, "end": v(3.09, 43.82) * mm});
            skLineSegment(sketch, "E702", {"start": v(3.09, 43.82) * mm, "end": v(3.18, 43.82) * mm});
            skLineSegment(sketch, "E703", {"start": v(3.18, 43.82) * mm, "end": v(3.26, 43.8) * mm});
            skLineSegment(sketch, "E704", {"start": v(3.26, 43.8) * mm, "end": v(3.35, 43.8) * mm});
            skLineSegment(sketch, "E705", {"start": v(3.35, 43.8) * mm, "end": v(3.44, 43.77) * mm});
            skLineSegment(sketch, "E706", {"start": v(3.44, 43.77) * mm, "end": v(3.53, 43.74) * mm});
            skLineSegment(sketch, "E707", {"start": v(3.53, 43.74) * mm, "end": v(3.62, 43.71) * mm});
            skLineSegment(sketch, "E708", {"start": v(3.62, 43.71) * mm, "end": v(3.69, 43.69) * mm});
            skLineSegment(sketch, "E709", {"start": v(3.69, 43.69) * mm, "end": v(3.7, 43.68) * mm});
            skLineSegment(sketch, "E710", {"start": v(3.7, 43.68) * mm, "end": v(3.73, 43.67) * mm});
            skLineSegment(sketch, "E711", {"start": v(3.73, 43.67) * mm, "end": v(3.73, 43.67) * mm});
            skLineSegment(sketch, "E712", {"start": v(3.73, 43.67) * mm, "end": v(3.92, 43.58) * mm});
            skLineSegment(sketch, "E713", {"start": v(3.92, 43.58) * mm, "end": v(3.96, 43.57) * mm});
            skLineSegment(sketch, "E714", {"start": v(3.96, 43.57) * mm, "end": v(4, 43.57) * mm});
            skLineSegment(sketch, "E715", {"start": v(4, 43.57) * mm, "end": v(4.03, 43.57) * mm});
            skLineSegment(sketch, "E716", {"start": v(4.03, 43.57) * mm, "end": v(4.06, 43.59) * mm});
            skLineSegment(sketch, "E717", {"start": v(4.06, 43.59) * mm, "end": v(4.1, 43.61) * mm});
            skLineSegment(sketch, "E718", {"start": v(4.1, 43.61) * mm, "end": v(4.13, 43.64) * mm});
            skLineSegment(sketch, "E719", {"start": v(4.13, 43.64) * mm, "end": v(4.15, 43.67) * mm});
            skLineSegment(sketch, "E720", {"start": v(4.15, 43.67) * mm, "end": v(4.18, 43.7) * mm});
            skLineSegment(sketch, "E721", {"start": v(4.18, 43.7) * mm, "end": v(4.2, 43.74) * mm});
            skLineSegment(sketch, "E722", {"start": v(4.2, 43.74) * mm, "end": v(4.2, 43.77) * mm});
            skLineSegment(sketch, "E723", {"start": v(4.2, 43.77) * mm, "end": v(4.2, 43.8) * mm});
            skLineSegment(sketch, "E724", {"start": v(4.2, 43.8) * mm, "end": v(4.2, 43.84) * mm});
            skLineSegment(sketch, "E725", {"start": v(4.2, 43.84) * mm, "end": v(4.19, 43.87) * mm});
            skLineSegment(sketch, "E726", {"start": v(4.19, 43.87) * mm, "end": v(4.17, 43.9) * mm});
            skLineSegment(sketch, "E727", {"start": v(4.17, 43.9) * mm, "end": v(3.06, 45) * mm});
            skLineSegment(sketch, "E728", {"start": v(3.06, 45) * mm, "end": v(1.87, 43.81) * mm});
            skLineSegment(sketch, "E729", {"start": v(7.3, 44.91) * mm, "end": v(7.62, 44.6) * mm});
            skLineSegment(sketch, "E730", {"start": v(7.62, 44.6) * mm, "end": v(7.68, 44.67) * mm});
            skLineSegment(sketch, "E731", {"start": v(7.68, 44.67) * mm, "end": v(7.86, 44.86) * mm});
            skLineSegment(sketch, "E732", {"start": v(7.86, 44.86) * mm, "end": v(7.99, 45) * mm});
            skLineSegment(sketch, "E733", {"start": v(7.99, 45) * mm, "end": v(8.07, 45.1) * mm});
            skLineSegment(sketch, "E734", {"start": v(8.07, 45.1) * mm, "end": v(8.1, 45.13) * mm});
            skLineSegment(sketch, "E735", {"start": v(8.1, 45.13) * mm, "end": v(8.21, 45.3) * mm});
            skLineSegment(sketch, "E736", {"start": v(8.21, 45.3) * mm, "end": v(8.25, 45.35) * mm});
            skLineSegment(sketch, "E737", {"start": v(8.25, 45.35) * mm, "end": v(8.24, 45.35) * mm});
            skLineSegment(sketch, "E738", {"start": v(8.24, 45.35) * mm, "end": v(8.24, 45.36) * mm});
            skLineSegment(sketch, "E739", {"start": v(8.24, 45.36) * mm, "end": v(8.25, 45.36) * mm});
            skLineSegment(sketch, "E740", {"start": v(8.25, 45.36) * mm, "end": v(8.25, 45.35) * mm});
            skLineSegment(sketch, "E741", {"start": v(8.25, 45.35) * mm, "end": v(8.3, 45.42) * mm});
            skLineSegment(sketch, "E742", {"start": v(8.3, 45.42) * mm, "end": v(8.38, 45.59) * mm});
            skLineSegment(sketch, "E743", {"start": v(8.38, 45.59) * mm, "end": v(8.41, 45.67) * mm});
            skLineSegment(sketch, "E744", {"start": v(8.41, 45.67) * mm, "end": v(8.44, 45.75) * mm});
            skLineSegment(sketch, "E745", {"start": v(8.44, 45.75) * mm, "end": v(8.47, 45.83) * mm});
            skLineSegment(sketch, "E746", {"start": v(8.47, 45.83) * mm, "end": v(8.5, 45.91) * mm});
            skLineSegment(sketch, "E747", {"start": v(8.5, 45.91) * mm, "end": v(8.53, 46.1) * mm});
            skLineSegment(sketch, "E748", {"start": v(8.53, 46.1) * mm, "end": v(8.53, 46.15) * mm});
            skLineSegment(sketch, "E749", {"start": v(8.53, 46.15) * mm, "end": v(8.54, 46.42) * mm});
            skLineSegment(sketch, "E750", {"start": v(8.54, 46.42) * mm, "end": v(8.53, 46.48) * mm});
            skLineSegment(sketch, "E751", {"start": v(8.53, 46.48) * mm, "end": v(8.5, 46.61) * mm});
            skLineSegment(sketch, "E752", {"start": v(8.5, 46.61) * mm, "end": v(8.47, 46.73) * mm});
            skLineSegment(sketch, "E753", {"start": v(8.47, 46.73) * mm, "end": v(8.45, 46.78) * mm});
            skLineSegment(sketch, "E754", {"start": v(8.45, 46.78) * mm, "end": v(8.46, 46.8) * mm});
            skLineSegment(sketch, "E755", {"start": v(8.46, 46.8) * mm, "end": v(8.54, 46.7) * mm});
            skLineSegment(sketch, "E756", {"start": v(8.54, 46.7) * mm, "end": v(8.55, 46.7) * mm});
            skLineSegment(sketch, "E757", {"start": v(8.55, 46.7) * mm, "end": v(8.55, 46.7) * mm});
            skLineSegment(sketch, "E758", {"start": v(8.55, 46.7) * mm, "end": v(8.54, 46.69) * mm});
            skLineSegment(sketch, "E759", {"start": v(8.54, 46.69) * mm, "end": v(8.79, 46.45) * mm});
            skLineSegment(sketch, "E760", {"start": v(8.79, 46.45) * mm, "end": v(8.91, 46.34) * mm});
            skLineSegment(sketch, "E761", {"start": v(8.91, 46.34) * mm, "end": v(8.92, 46.34) * mm});
            skLineSegment(sketch, "E762", {"start": v(8.92, 46.34) * mm, "end": v(8.92, 46.34) * mm});
            skLineSegment(sketch, "E763", {"start": v(8.92, 46.34) * mm, "end": v(8.92, 46.33) * mm});
            skLineSegment(sketch, "E764", {"start": v(8.92, 46.33) * mm, "end": v(8.98, 46.29) * mm});
            skLineSegment(sketch, "E765", {"start": v(8.98, 46.29) * mm, "end": v(9.12, 46.18) * mm});
            skLineSegment(sketch, "E766", {"start": v(9.12, 46.18) * mm, "end": v(9.2, 46.12) * mm});
            skLineSegment(sketch, "E767", {"start": v(9.2, 46.12) * mm, "end": v(9.23, 46.1) * mm});
            skLineSegment(sketch, "E768", {"start": v(9.23, 46.1) * mm, "end": v(9.27, 46.07) * mm});
            skLineSegment(sketch, "E769", {"start": v(9.27, 46.07) * mm, "end": v(9.28, 46.07) * mm});
            skLineSegment(sketch, "E770", {"start": v(9.28, 46.07) * mm, "end": v(9.3, 46.05) * mm});
            skLineSegment(sketch, "E771", {"start": v(9.3, 46.05) * mm, "end": v(9.33, 46.03) * mm});
            skLineSegment(sketch, "E772", {"start": v(9.33, 46.03) * mm, "end": v(9.43, 45.97) * mm});
            skLineSegment(sketch, "E773", {"start": v(9.43, 45.97) * mm, "end": v(9.56, 45.9) * mm});
            skLineSegment(sketch, "E774", {"start": v(9.56, 45.9) * mm, "end": v(9.7, 45.82) * mm});
            skLineSegment(sketch, "E775", {"start": v(9.7, 45.82) * mm, "end": v(9.84, 45.76) * mm});
            skLineSegment(sketch, "E776", {"start": v(9.84, 45.76) * mm, "end": v(9.98, 45.7) * mm});
            skLineSegment(sketch, "E777", {"start": v(9.98, 45.7) * mm, "end": v(10.12, 45.66) * mm});
            skLineSegment(sketch, "E778", {"start": v(10.12, 45.66) * mm, "end": v(10.26, 45.62) * mm});
            skLineSegment(sketch, "E779", {"start": v(10.26, 45.62) * mm, "end": v(10.4, 45.6) * mm});
            skLineSegment(sketch, "E780", {"start": v(10.4, 45.6) * mm, "end": v(10.56, 45.57) * mm});
            skLineSegment(sketch, "E781", {"start": v(10.56, 45.57) * mm, "end": v(10.62, 45.56) * mm});
            skLineSegment(sketch, "E782", {"start": v(10.62, 45.56) * mm, "end": v(11.04, 45.56) * mm});
            skLineSegment(sketch, "E783", {"start": v(11.04, 45.56) * mm, "end": v(11.12, 45.57) * mm});
            skLineSegment(sketch, "E784", {"start": v(11.12, 45.57) * mm, "end": v(11.28, 45.6) * mm});
            skLineSegment(sketch, "E785", {"start": v(11.28, 45.6) * mm, "end": v(11.43, 45.63) * mm});
            skLineSegment(sketch, "E786", {"start": v(11.43, 45.63) * mm, "end": v(11.58, 45.68) * mm});
            skLineSegment(sketch, "E787", {"start": v(11.58, 45.68) * mm, "end": v(11.74, 45.74) * mm});
            skLineSegment(sketch, "E788", {"start": v(11.74, 45.74) * mm, "end": v(11.78, 45.76) * mm});
            skLineSegment(sketch, "E789", {"start": v(11.78, 45.76) * mm, "end": v(11.87, 45.8) * mm});
            skLineSegment(sketch, "E790", {"start": v(11.87, 45.8) * mm, "end": v(12.04, 45.9) * mm});
            skLineSegment(sketch, "E791", {"start": v(12.04, 45.9) * mm, "end": v(12.13, 45.95) * mm});
            skLineSegment(sketch, "E792", {"start": v(12.13, 45.95) * mm, "end": v(12.15, 45.96) * mm});
            skLineSegment(sketch, "E793", {"start": v(12.15, 45.96) * mm, "end": v(12.2, 46) * mm});
            skLineSegment(sketch, "E794", {"start": v(12.2, 46) * mm, "end": v(12.21, 46.01) * mm});
            skLineSegment(sketch, "E795", {"start": v(12.21, 46.01) * mm, "end": v(12.22, 46.02) * mm});
            skLineSegment(sketch, "E796", {"start": v(12.22, 46.02) * mm, "end": v(12.25, 46.04) * mm});
            skLineSegment(sketch, "E797", {"start": v(12.25, 46.04) * mm, "end": v(12.28, 46.06) * mm});
            skLineSegment(sketch, "E798", {"start": v(12.28, 46.06) * mm, "end": v(12.41, 46.16) * mm});
            skLineSegment(sketch, "E799", {"start": v(12.41, 46.16) * mm, "end": v(12.1, 46.47) * mm});
            skLineSegment(sketch, "E800", {"start": v(12.1, 46.47) * mm, "end": v(12.08, 46.46) * mm});
            skLineSegment(sketch, "E801", {"start": v(12.08, 46.46) * mm, "end": v(11.97, 46.42) * mm});
            skLineSegment(sketch, "E802", {"start": v(11.97, 46.42) * mm, "end": v(11.88, 46.4) * mm});
            skLineSegment(sketch, "E803", {"start": v(11.88, 46.4) * mm, "end": v(11.8, 46.4) * mm});
            skLineSegment(sketch, "E804", {"start": v(11.8, 46.4) * mm, "end": v(11.7, 46.41) * mm});
            skLineSegment(sketch, "E805", {"start": v(11.7, 46.41) * mm, "end": v(11.66, 46.43) * mm});
            skLineSegment(sketch, "E806", {"start": v(11.66, 46.43) * mm, "end": v(11.62, 46.44) * mm});
            skLineSegment(sketch, "E807", {"start": v(11.62, 46.44) * mm, "end": v(11.58, 46.47) * mm});
            skLineSegment(sketch, "E808", {"start": v(11.58, 46.47) * mm, "end": v(11.54, 46.5) * mm});
            skLineSegment(sketch, "E809", {"start": v(11.54, 46.5) * mm, "end": v(11.5, 46.53) * mm});
            skLineSegment(sketch, "E810", {"start": v(11.5, 46.53) * mm, "end": v(8.6, 49.42) * mm});
            skLineSegment(sketch, "E811", {"start": v(8.6, 49.42) * mm, "end": v(8.57, 49.46) * mm});
            skLineSegment(sketch, "E812", {"start": v(8.57, 49.46) * mm, "end": v(8.52, 49.53) * mm});
            skLineSegment(sketch, "E813", {"start": v(8.52, 49.53) * mm, "end": v(8.5, 49.6) * mm});
            skLineSegment(sketch, "E814", {"start": v(8.5, 49.6) * mm, "end": v(8.48, 49.67) * mm});
            skLineSegment(sketch, "E815", {"start": v(8.48, 49.67) * mm, "end": v(8.47, 49.75) * mm});
            skLineSegment(sketch, "E816", {"start": v(8.47, 49.75) * mm, "end": v(8.47, 49.8) * mm});
            skLineSegment(sketch, "E817", {"start": v(8.47, 49.8) * mm, "end": v(8.48, 49.86) * mm});
            skLineSegment(sketch, "E818", {"start": v(8.48, 49.86) * mm, "end": v(8.5, 49.92) * mm});
            skLineSegment(sketch, "E819", {"start": v(8.5, 49.92) * mm, "end": v(8.52, 49.98) * mm});
            skLineSegment(sketch, "E820", {"start": v(8.52, 49.98) * mm, "end": v(8.54, 50.03) * mm});
            skLineSegment(sketch, "E821", {"start": v(8.54, 50.03) * mm, "end": v(8.23, 50.34) * mm});
            skLineSegment(sketch, "E822", {"start": v(8.23, 50.34) * mm, "end": v(8.21, 50.32) * mm});
            skLineSegment(sketch, "E823", {"start": v(8.21, 50.32) * mm, "end": v(8.2, 50.3) * mm});
            skLineSegment(sketch, "E824", {"start": v(8.2, 50.3) * mm, "end": v(8.2, 50.3) * mm});
            skLineSegment(sketch, "E825", {"start": v(8.2, 50.3) * mm, "end": v(8.2, 50.29) * mm});
            skLineSegment(sketch, "E826", {"start": v(8.2, 50.29) * mm, "end": v(8.2, 50.29) * mm});
            skLineSegment(sketch, "E827", {"start": v(8.2, 50.29) * mm, "end": v(8.19, 50.29) * mm});
            skLineSegment(sketch, "E828", {"start": v(8.19, 50.29) * mm, "end": v(8.13, 50.21) * mm});
            skLineSegment(sketch, "E829", {"start": v(8.13, 50.21) * mm, "end": v(8.03, 50.07) * mm});
            skLineSegment(sketch, "E830", {"start": v(8.03, 50.07) * mm, "end": v(7.94, 49.92) * mm});
            skLineSegment(sketch, "E831", {"start": v(7.94, 49.92) * mm, "end": v(7.86, 49.78) * mm});
            skLineSegment(sketch, "E832", {"start": v(7.86, 49.78) * mm, "end": v(7.8, 49.63) * mm});
            skLineSegment(sketch, "E833", {"start": v(7.8, 49.63) * mm, "end": v(7.74, 49.47) * mm});
            skLineSegment(sketch, "E834", {"start": v(7.74, 49.47) * mm, "end": v(7.7, 49.31) * mm});
            skLineSegment(sketch, "E835", {"start": v(7.7, 49.31) * mm, "end": v(7.66, 49.15) * mm});
            skLineSegment(sketch, "E836", {"start": v(7.66, 49.15) * mm, "end": v(7.63, 48.98) * mm});
            skLineSegment(sketch, "E837", {"start": v(7.63, 48.98) * mm, "end": v(7.63, 48.91) * mm});
            skLineSegment(sketch, "E838", {"start": v(7.63, 48.91) * mm, "end": v(7.63, 48.6) * mm});
            skLineSegment(sketch, "E839", {"start": v(7.63, 48.6) * mm, "end": v(7.63, 48.53) * mm});
            skLineSegment(sketch, "E840", {"start": v(7.63, 48.53) * mm, "end": v(7.65, 48.4) * mm});
            skLineSegment(sketch, "E841", {"start": v(7.65, 48.4) * mm, "end": v(7.67, 48.29) * mm});
            skLineSegment(sketch, "E842", {"start": v(7.67, 48.29) * mm, "end": v(7.7, 48.17) * mm});
            skLineSegment(sketch, "E843", {"start": v(7.7, 48.17) * mm, "end": v(7.73, 48.05) * mm});
            skLineSegment(sketch, "E844", {"start": v(7.73, 48.05) * mm, "end": v(7.77, 47.93) * mm});
            skLineSegment(sketch, "E845", {"start": v(7.77, 47.93) * mm, "end": v(7.81, 47.82) * mm});
            skLineSegment(sketch, "E846", {"start": v(7.81, 47.82) * mm, "end": v(7.86, 47.7) * mm});
            skLineSegment(sketch, "E847", {"start": v(7.86, 47.7) * mm, "end": v(7.91, 47.6) * mm});
            skLineSegment(sketch, "E848", {"start": v(7.91, 47.6) * mm, "end": v(7.95, 47.51) * mm});
            skLineSegment(sketch, "E849", {"start": v(7.95, 47.51) * mm, "end": v(7.94, 47.51) * mm});
            skLineSegment(sketch, "E850", {"start": v(7.94, 47.51) * mm, "end": v(7.9, 47.56) * mm});
            skLineSegment(sketch, "E851", {"start": v(7.9, 47.56) * mm, "end": v(7.81, 47.63) * mm});
            skLineSegment(sketch, "E852", {"start": v(7.81, 47.63) * mm, "end": v(7.78, 47.64) * mm});
            skLineSegment(sketch, "E853", {"start": v(7.78, 47.64) * mm, "end": v(7.78, 47.64) * mm});
            skLineSegment(sketch, "E854", {"start": v(7.78, 47.64) * mm, "end": v(7.78, 47.65) * mm});
            skLineSegment(sketch, "E855", {"start": v(7.78, 47.65) * mm, "end": v(7.78, 47.65) * mm});
            skLineSegment(sketch, "E856", {"start": v(7.78, 47.65) * mm, "end": v(7.72, 47.7) * mm});
            skLineSegment(sketch, "E857", {"start": v(7.72, 47.7) * mm, "end": v(7.63, 47.76) * mm});
            skLineSegment(sketch, "E858", {"start": v(7.63, 47.76) * mm, "end": v(7.54, 47.81) * mm});
            skLineSegment(sketch, "E859", {"start": v(7.54, 47.81) * mm, "end": v(7.46, 47.85) * mm});
            skLineSegment(sketch, "E860", {"start": v(7.46, 47.85) * mm, "end": v(7.38, 47.9) * mm});
            skLineSegment(sketch, "E861", {"start": v(7.38, 47.9) * mm, "end": v(7.3, 47.92) * mm});
            skLineSegment(sketch, "E862", {"start": v(7.3, 47.92) * mm, "end": v(7.23, 47.95) * mm});
            skLineSegment(sketch, "E863", {"start": v(7.23, 47.95) * mm, "end": v(7.15, 47.97) * mm});
            skLineSegment(sketch, "E864", {"start": v(7.15, 47.97) * mm, "end": v(7.07, 47.98) * mm});
            skLineSegment(sketch, "E865", {"start": v(7.07, 47.98) * mm, "end": v(7, 48) * mm});
            skLineSegment(sketch, "E866", {"start": v(7, 48) * mm, "end": v(6.91, 48) * mm});
            skLineSegment(sketch, "E867", {"start": v(6.91, 48) * mm, "end": v(6.83, 48) * mm});
            skLineSegment(sketch, "E868", {"start": v(6.83, 48) * mm, "end": v(6.75, 48) * mm});
            skLineSegment(sketch, "E869", {"start": v(6.75, 48) * mm, "end": v(6.59, 47.99) * mm});
            skLineSegment(sketch, "E870", {"start": v(6.59, 47.99) * mm, "end": v(6.42, 47.95) * mm});
            skLineSegment(sketch, "E871", {"start": v(6.42, 47.95) * mm, "end": v(6.26, 47.9) * mm});
            skLineSegment(sketch, "E872", {"start": v(6.26, 47.9) * mm, "end": v(6.1, 47.84) * mm});
            skLineSegment(sketch, "E873", {"start": v(6.1, 47.84) * mm, "end": v(5.98, 47.77) * mm});
            skLineSegment(sketch, "E874", {"start": v(5.98, 47.77) * mm, "end": v(5.84, 47.69) * mm});
            skLineSegment(sketch, "E875", {"start": v(5.84, 47.69) * mm, "end": v(5.7, 47.6) * mm});
            skLineSegment(sketch, "E876", {"start": v(5.7, 47.6) * mm, "end": v(5.58, 47.5) * mm});
            skLineSegment(sketch, "E877", {"start": v(5.58, 47.5) * mm, "end": v(5.52, 47.44) * mm});
            skLineSegment(sketch, "E878", {"start": v(5.52, 47.44) * mm, "end": v(5.38, 47.32) * mm});
            skLineSegment(sketch, "E879", {"start": v(5.38, 47.32) * mm, "end": v(5.34, 47.28) * mm});
            skLineSegment(sketch, "E880", {"start": v(5.34, 47.28) * mm, "end": v(5.14, 47.08) * mm});
            skLineSegment(sketch, "E881", {"start": v(5.14, 47.08) * mm, "end": v(5.45, 46.78) * mm});
            skLineSegment(sketch, "E882", {"start": v(5.45, 46.78) * mm, "end": v(5.49, 46.8) * mm});
            skLineSegment(sketch, "E883", {"start": v(5.49, 46.8) * mm, "end": v(5.56, 46.85) * mm});
            skLineSegment(sketch, "E884", {"start": v(5.56, 46.85) * mm, "end": v(5.64, 46.87) * mm});
            skLineSegment(sketch, "E885", {"start": v(5.64, 46.87) * mm, "end": v(5.71, 46.89) * mm});
            skLineSegment(sketch, "E886", {"start": v(5.71, 46.89) * mm, "end": v(5.8, 46.89) * mm});
            skLineSegment(sketch, "E887", {"start": v(5.8, 46.89) * mm, "end": v(5.87, 46.88) * mm});
            skLineSegment(sketch, "E888", {"start": v(5.87, 46.88) * mm, "end": v(5.95, 46.85) * mm});
            skLineSegment(sketch, "E889", {"start": v(5.95, 46.85) * mm, "end": v(6.03, 46.8) * mm});
            skLineSegment(sketch, "E890", {"start": v(6.03, 46.8) * mm, "end": v(6.11, 46.76) * mm});
            skLineSegment(sketch, "E891", {"start": v(6.11, 46.76) * mm, "end": v(6.18, 46.7) * mm});
            skLineSegment(sketch, "E892", {"start": v(6.18, 46.7) * mm, "end": v(7.18, 45.71) * mm});
            skLineSegment(sketch, "E893", {"start": v(7.18, 45.71) * mm, "end": v(7.24, 45.65) * mm});
            skLineSegment(sketch, "E894", {"start": v(7.24, 45.65) * mm, "end": v(7.32, 45.54) * mm});
            skLineSegment(sketch, "E895", {"start": v(7.32, 45.54) * mm, "end": v(7.35, 45.5) * mm});
            skLineSegment(sketch, "E896", {"start": v(7.35, 45.5) * mm, "end": v(7.38, 45.45) * mm});
            skLineSegment(sketch, "E897", {"start": v(7.38, 45.45) * mm, "end": v(7.4, 45.4) * mm});
            skLineSegment(sketch, "E898", {"start": v(7.4, 45.4) * mm, "end": v(7.41, 45.36) * mm});
            skLineSegment(sketch, "E899", {"start": v(7.41, 45.36) * mm, "end": v(7.42, 45.31) * mm});
            skLineSegment(sketch, "E900", {"start": v(7.42, 45.31) * mm, "end": v(7.42, 45.26) * mm});
            skLineSegment(sketch, "E901", {"start": v(7.42, 45.26) * mm, "end": v(7.42, 45.2) * mm});
            skLineSegment(sketch, "E902", {"start": v(7.42, 45.2) * mm, "end": v(7.41, 45.13) * mm});
            skLineSegment(sketch, "E903", {"start": v(7.41, 45.13) * mm, "end": v(7.38, 45.04) * mm});
            skLineSegment(sketch, "E904", {"start": v(7.38, 45.04) * mm, "end": v(7.34, 44.96) * mm});
            skLineSegment(sketch, "E905", {"start": v(7.34, 44.96) * mm, "end": v(7.31, 44.92) * mm});
            skLineSegment(sketch, "E906", {"start": v(7.31, 44.92) * mm, "end": v(7.3, 44.91) * mm});
            skLineSegment(sketch, "E907", {"start": v(-6.26, 44.72) * mm, "end": v(-6.27, 44.73) * mm});
            skLineSegment(sketch, "E908", {"start": v(-6.27, 44.73) * mm, "end": v(-6.27, 44.72) * mm});
            skLineSegment(sketch, "E909", {"start": v(-6.27, 44.72) * mm, "end": v(-6.27, 44.72) * mm});
            skLineSegment(sketch, "E910", {"start": v(-6.27, 44.72) * mm, "end": v(-6.26, 44.72) * mm});
            skLineSegment(sketch, "E911", {"start": v(-2.6, 42.84) * mm, "end": v(-2.5, 42.83) * mm});
            skLineSegment(sketch, "E912", {"start": v(-2.5, 42.83) * mm, "end": v(-2.11, 42.84) * mm});
            skLineSegment(sketch, "E913", {"start": v(-2.11, 42.84) * mm, "end": v(-2.03, 42.84) * mm});
            skLineSegment(sketch, "E914", {"start": v(-2.03, 42.84) * mm, "end": v(-1.8, 42.87) * mm});
            skLineSegment(sketch, "E915", {"start": v(-1.8, 42.87) * mm, "end": v(-1.59, 42.9) * mm});
            skLineSegment(sketch, "E916", {"start": v(-1.59, 42.9) * mm, "end": v(-1.37, 42.95) * mm});
            skLineSegment(sketch, "E917", {"start": v(-1.37, 42.95) * mm, "end": v(-1.16, 43.01) * mm});
            skLineSegment(sketch, "E918", {"start": v(-1.16, 43.01) * mm, "end": v(-0.95, 43.09) * mm});
            skLineSegment(sketch, "E919", {"start": v(-0.95, 43.09) * mm, "end": v(-0.74, 43.17) * mm});
            skLineSegment(sketch, "E920", {"start": v(-0.74, 43.17) * mm, "end": v(-0.53, 43.27) * mm});
            skLineSegment(sketch, "E921", {"start": v(-0.53, 43.27) * mm, "end": v(-0.33, 43.37) * mm});
            skLineSegment(sketch, "E922", {"start": v(-0.33, 43.37) * mm, "end": v(-0.24, 43.43) * mm});
            skLineSegment(sketch, "E923", {"start": v(-0.24, 43.43) * mm, "end": v(-0.14, 43.48) * mm});
            skLineSegment(sketch, "E924", {"start": v(-0.14, 43.48) * mm, "end": v(-0.15, 43.48) * mm});
            skLineSegment(sketch, "E925", {"start": v(-0.15, 43.48) * mm, "end": v(-0.14, 43.49) * mm});
            skLineSegment(sketch, "E926", {"start": v(-0.14, 43.49) * mm, "end": v(-0.13, 43.49) * mm});
            skLineSegment(sketch, "E927", {"start": v(-0.13, 43.49) * mm, "end": v(0, 43.57) * mm});
            skLineSegment(sketch, "E928", {"start": v(0, 43.57) * mm, "end": v(0.22, 43.73) * mm});
            skLineSegment(sketch, "E929", {"start": v(0.22, 43.73) * mm, "end": v(0.32, 43.8) * mm});
            skLineSegment(sketch, "E930", {"start": v(0.32, 43.8) * mm, "end": v(0.44, 43.9) * mm});
            skLineSegment(sketch, "E931", {"start": v(0.44, 43.9) * mm, "end": v(-0.11, 44.46) * mm});
            skLineSegment(sketch, "E932", {"start": v(-0.11, 44.46) * mm, "end": v(-0.19, 44.43) * mm});
            skLineSegment(sketch, "E933", {"start": v(-0.19, 44.43) * mm, "end": v(-0.3, 44.38) * mm});
            skLineSegment(sketch, "E934", {"start": v(-0.3, 44.38) * mm, "end": v(-0.41, 44.35) * mm});
            skLineSegment(sketch, "E935", {"start": v(-0.41, 44.35) * mm, "end": v(-0.49, 44.34) * mm});
            skLineSegment(sketch, "E936", {"start": v(-0.49, 44.34) * mm, "end": v(-0.58, 44.34) * mm});
            skLineSegment(sketch, "E937", {"start": v(-0.58, 44.34) * mm, "end": v(-0.66, 44.34) * mm});
            skLineSegment(sketch, "E938", {"start": v(-0.66, 44.34) * mm, "end": v(-0.73, 44.34) * mm});
            skLineSegment(sketch, "E939", {"start": v(-0.73, 44.34) * mm, "end": v(-0.82, 44.36) * mm});
            skLineSegment(sketch, "E940", {"start": v(-0.82, 44.36) * mm, "end": v(-0.92, 44.4) * mm});
            skLineSegment(sketch, "E941", {"start": v(-0.92, 44.4) * mm, "end": v(-1, 44.44) * mm});
            skLineSegment(sketch, "E942", {"start": v(-1, 44.44) * mm, "end": v(-1.09, 44.5) * mm});
            skLineSegment(sketch, "E943", {"start": v(-1.09, 44.5) * mm, "end": v(-1.15, 44.53) * mm});
            skLineSegment(sketch, "E944", {"start": v(-1.15, 44.53) * mm, "end": v(-1.15, 44.53) * mm});
            skLineSegment(sketch, "E945", {"start": v(-1.15, 44.53) * mm, "end": v(-1.15, 44.54) * mm});
            skLineSegment(sketch, "E946", {"start": v(-1.15, 44.54) * mm, "end": v(-1.18, 44.56) * mm});
            skLineSegment(sketch, "E947", {"start": v(-1.18, 44.56) * mm, "end": v(-1.21, 44.59) * mm});
            skLineSegment(sketch, "E948", {"start": v(-1.21, 44.59) * mm, "end": v(-6.32, 49.7) * mm});
            skLineSegment(sketch, "E949", {"start": v(-6.32, 49.7) * mm, "end": v(-6.35, 49.74) * mm});
            skLineSegment(sketch, "E950", {"start": v(-6.35, 49.74) * mm, "end": v(-6.43, 49.84) * mm});
            skLineSegment(sketch, "E951", {"start": v(-6.43, 49.84) * mm, "end": v(-6.46, 49.9) * mm});
            skLineSegment(sketch, "E952", {"start": v(-6.46, 49.9) * mm, "end": v(-6.5, 49.95) * mm});
            skLineSegment(sketch, "E953", {"start": v(-6.5, 49.95) * mm, "end": v(-6.52, 50) * mm});
            skLineSegment(sketch, "E954", {"start": v(-6.52, 50) * mm, "end": v(-6.54, 50.07) * mm});
            skLineSegment(sketch, "E955", {"start": v(-6.54, 50.07) * mm, "end": v(-6.55, 50.12) * mm});
            skLineSegment(sketch, "E956", {"start": v(-6.55, 50.12) * mm, "end": v(-6.56, 50.18) * mm});
            skLineSegment(sketch, "E957", {"start": v(-6.56, 50.18) * mm, "end": v(-6.57, 50.24) * mm});
            skLineSegment(sketch, "E958", {"start": v(-6.57, 50.24) * mm, "end": v(-6.57, 50.3) * mm});
            skLineSegment(sketch, "E959", {"start": v(-6.57, 50.3) * mm, "end": v(-6.56, 50.37) * mm});
            skLineSegment(sketch, "E960", {"start": v(-6.56, 50.37) * mm, "end": v(-6.56, 50.43) * mm});
            skLineSegment(sketch, "E961", {"start": v(-6.56, 50.43) * mm, "end": v(-6.53, 50.56) * mm});
            skLineSegment(sketch, "E962", {"start": v(-6.53, 50.56) * mm, "end": v(-6.48, 50.7) * mm});
            skLineSegment(sketch, "E963", {"start": v(-6.48, 50.7) * mm, "end": v(-6.44, 50.79) * mm});
            skLineSegment(sketch, "E964", {"start": v(-6.44, 50.79) * mm, "end": v(-7, 51.34) * mm});
            skLineSegment(sketch, "E965", {"start": v(-7, 51.34) * mm, "end": v(-7, 51.33) * mm});
            skLineSegment(sketch, "E966", {"start": v(-7, 51.33) * mm, "end": v(-7.04, 51.29) * mm});
            skLineSegment(sketch, "E967", {"start": v(-7.04, 51.29) * mm, "end": v(-7.06, 51.26) * mm});
            skLineSegment(sketch, "E968", {"start": v(-7.06, 51.26) * mm, "end": v(-7.1, 51.2) * mm});
            skLineSegment(sketch, "E969", {"start": v(-7.1, 51.2) * mm, "end": v(-7.2, 51.09) * mm});
            skLineSegment(sketch, "E970", {"start": v(-7.2, 51.09) * mm, "end": v(-7.29, 50.95) * mm});
            skLineSegment(sketch, "E971", {"start": v(-7.29, 50.95) * mm, "end": v(-7.32, 50.9) * mm});
            skLineSegment(sketch, "E972", {"start": v(-7.32, 50.9) * mm, "end": v(-7.32, 50.9) * mm});
            skLineSegment(sketch, "E973", {"start": v(-7.32, 50.9) * mm, "end": v(-7.33, 50.88) * mm});
            skLineSegment(sketch, "E974", {"start": v(-7.33, 50.88) * mm, "end": v(-7.36, 50.84) * mm});
            skLineSegment(sketch, "E975", {"start": v(-7.36, 50.84) * mm, "end": v(-7.38, 50.81) * mm});
            skLineSegment(sketch, "E976", {"start": v(-7.38, 50.81) * mm, "end": v(-7.38, 50.8) * mm});
            skLineSegment(sketch, "E977", {"start": v(-7.38, 50.8) * mm, "end": v(-7.38, 50.8) * mm});
            skLineSegment(sketch, "E978", {"start": v(-7.38, 50.8) * mm, "end": v(-7.4, 50.8) * mm});
            skLineSegment(sketch, "E979", {"start": v(-7.4, 50.8) * mm, "end": v(-7.4, 50.78) * mm});
            skLineSegment(sketch, "E980", {"start": v(-7.4, 50.78) * mm, "end": v(-7.41, 50.76) * mm});
            skLineSegment(sketch, "E981", {"start": v(-7.41, 50.76) * mm, "end": v(-7.41, 50.74) * mm});
            skLineSegment(sketch, "E982", {"start": v(-7.41, 50.74) * mm, "end": v(-7.4, 50.74) * mm});
            skLineSegment(sketch, "E983", {"start": v(-7.4, 50.74) * mm, "end": v(-7.41, 50.74) * mm});
            skLineSegment(sketch, "E984", {"start": v(-7.41, 50.74) * mm, "end": v(-7.42, 50.75) * mm});
            skLineSegment(sketch, "E985", {"start": v(-7.42, 50.75) * mm, "end": v(-7.48, 50.65) * mm});
            skLineSegment(sketch, "E986", {"start": v(-7.48, 50.65) * mm, "end": v(-7.56, 50.51) * mm});
            skLineSegment(sketch, "E987", {"start": v(-7.56, 50.51) * mm, "end": v(-7.64, 50.36) * mm});
            skLineSegment(sketch, "E988", {"start": v(-7.64, 50.36) * mm, "end": v(-7.71, 50.2) * mm});
            skLineSegment(sketch, "E989", {"start": v(-7.71, 50.2) * mm, "end": v(-7.78, 50.05) * mm});
            skLineSegment(sketch, "E990", {"start": v(-7.78, 50.05) * mm, "end": v(-7.83, 49.91) * mm});
            skLineSegment(sketch, "E991", {"start": v(-7.83, 49.91) * mm, "end": v(-7.87, 49.78) * mm});
            skLineSegment(sketch, "E992", {"start": v(-7.87, 49.78) * mm, "end": v(-7.91, 49.65) * mm});
            skLineSegment(sketch, "E993", {"start": v(-7.91, 49.65) * mm, "end": v(-7.95, 49.51) * mm});
            skLineSegment(sketch, "E994", {"start": v(-7.95, 49.51) * mm, "end": v(-7.98, 49.37) * mm});
            skLineSegment(sketch, "E995", {"start": v(-7.98, 49.37) * mm, "end": v(-8, 49.23) * mm});
            skLineSegment(sketch, "E996", {"start": v(-8, 49.23) * mm, "end": v(-8.03, 49.09) * mm});
            skLineSegment(sketch, "E997", {"start": v(-8.03, 49.09) * mm, "end": v(-8.05, 48.94) * mm});
            skLineSegment(sketch, "E998", {"start": v(-8.05, 48.94) * mm, "end": v(-8.06, 48.83) * mm});
            skLineSegment(sketch, "E999", {"start": v(-8.06, 48.83) * mm, "end": v(-8.06, 48.26) * mm});
            skLineSegment(sketch, "E1000", {"start": v(-8.06, 48.26) * mm, "end": v(-8.05, 48.18) * mm});
            skLineSegment(sketch, "E1001", {"start": v(-8.05, 48.18) * mm, "end": v(-8.03, 48) * mm});
            skLineSegment(sketch, "E1002", {"start": v(-8.03, 48) * mm, "end": v(-8, 47.83) * mm});
            skLineSegment(sketch, "E1003", {"start": v(-8, 47.83) * mm, "end": v(-7.98, 47.66) * mm});
            skLineSegment(sketch, "E1004", {"start": v(-7.98, 47.66) * mm, "end": v(-7.94, 47.5) * mm});
            skLineSegment(sketch, "E1005", {"start": v(-7.94, 47.5) * mm, "end": v(-7.9, 47.33) * mm});
            skLineSegment(sketch, "E1006", {"start": v(-7.9, 47.33) * mm, "end": v(-7.85, 47.17) * mm});
            skLineSegment(sketch, "E1007", {"start": v(-7.85, 47.17) * mm, "end": v(-7.79, 47) * mm});
            skLineSegment(sketch, "E1008", {"start": v(-7.79, 47) * mm, "end": v(-7.73, 46.84) * mm});
            skLineSegment(sketch, "E1009", {"start": v(-7.73, 46.84) * mm, "end": v(-7.68, 46.73) * mm});
            skLineSegment(sketch, "E1010", {"start": v(-7.68, 46.73) * mm, "end": v(-7.63, 46.61) * mm});
            skLineSegment(sketch, "E1011", {"start": v(-7.63, 46.61) * mm, "end": v(-7.63, 46.6) * mm});
            skLineSegment(sketch, "E1012", {"start": v(-7.63, 46.6) * mm, "end": v(-7.58, 46.5) * mm});
            skLineSegment(sketch, "E1013", {"start": v(-7.58, 46.5) * mm, "end": v(-7.47, 46.29) * mm});
            skLineSegment(sketch, "E1014", {"start": v(-7.47, 46.29) * mm, "end": v(-7.34, 46.06) * mm});
            skLineSegment(sketch, "E1015", {"start": v(-7.34, 46.06) * mm, "end": v(-7.2, 45.84) * mm});
            skLineSegment(sketch, "E1016", {"start": v(-7.2, 45.84) * mm, "end": v(-7.07, 45.64) * mm});
            skLineSegment(sketch, "E1017", {"start": v(-7.07, 45.64) * mm, "end": v(-7.01, 45.56) * mm});
            skLineSegment(sketch, "E1018", {"start": v(-7.01, 45.56) * mm, "end": v(-7, 45.55) * mm});
            skLineSegment(sketch, "E1019", {"start": v(-7, 45.55) * mm, "end": v(-6.96, 45.5) * mm});
            skLineSegment(sketch, "E1020", {"start": v(-6.96, 45.5) * mm, "end": v(-6.93, 45.45) * mm});
            skLineSegment(sketch, "E1021", {"start": v(-6.93, 45.45) * mm, "end": v(-6.85, 45.34) * mm});
            skLineSegment(sketch, "E1022", {"start": v(-6.85, 45.34) * mm, "end": v(-6.69, 45.14) * mm});
            skLineSegment(sketch, "E1023", {"start": v(-6.69, 45.14) * mm, "end": v(-6.6, 45.05) * mm});
            skLineSegment(sketch, "E1024", {"start": v(-6.6, 45.05) * mm, "end": v(-6.56, 45) * mm});
            skLineSegment(sketch, "E1025", {"start": v(-6.56, 45) * mm, "end": v(-6.35, 44.77) * mm});
            skLineSegment(sketch, "E1026", {"start": v(-6.35, 44.77) * mm, "end": v(-6.1, 44.53) * mm});
            skLineSegment(sketch, "E1027", {"start": v(-6.1, 44.53) * mm, "end": v(-5.87, 44.31) * mm});
            skLineSegment(sketch, "E1028", {"start": v(-5.87, 44.31) * mm, "end": v(-5.63, 44.11) * mm});
            skLineSegment(sketch, "E1029", {"start": v(-5.63, 44.11) * mm, "end": v(-5.55, 44.05) * mm});
            skLineSegment(sketch, "E1030", {"start": v(-5.55, 44.05) * mm, "end": v(-5.54, 44.04) * mm});
            skLineSegment(sketch, "E1031", {"start": v(-5.54, 44.04) * mm, "end": v(-5.37, 43.91) * mm});
            skLineSegment(sketch, "E1032", {"start": v(-5.37, 43.91) * mm, "end": v(-5.3, 43.86) * mm});
            skLineSegment(sketch, "E1033", {"start": v(-5.3, 43.86) * mm, "end": v(-5.24, 43.82) * mm});
            skLineSegment(sketch, "E1034", {"start": v(-5.24, 43.82) * mm, "end": v(-5.14, 43.75) * mm});
            skLineSegment(sketch, "E1035", {"start": v(-5.14, 43.75) * mm, "end": v(-4.96, 43.63) * mm});
            skLineSegment(sketch, "E1036", {"start": v(-4.96, 43.63) * mm, "end": v(-4.76, 43.52) * mm});
            skLineSegment(sketch, "E1037", {"start": v(-4.76, 43.52) * mm, "end": v(-4.68, 43.47) * mm});
            skLineSegment(sketch, "E1038", {"start": v(-4.68, 43.47) * mm, "end": v(-4.64, 43.45) * mm});
            skLineSegment(sketch, "E1039", {"start": v(-4.64, 43.45) * mm, "end": v(-4.61, 43.44) * mm});
            skLineSegment(sketch, "E1040", {"start": v(-4.61, 43.44) * mm, "end": v(-4.6, 43.43) * mm});
            skLineSegment(sketch, "E1041", {"start": v(-4.6, 43.43) * mm, "end": v(-4.6, 43.44) * mm});
            skLineSegment(sketch, "E1042", {"start": v(-4.6, 43.44) * mm, "end": v(-4.6, 43.43) * mm});
            skLineSegment(sketch, "E1043", {"start": v(-4.6, 43.43) * mm, "end": v(-4.6, 43.42) * mm});
            skLineSegment(sketch, "E1044", {"start": v(-4.6, 43.42) * mm, "end": v(-4.47, 43.36) * mm});
            skLineSegment(sketch, "E1045", {"start": v(-4.47, 43.36) * mm, "end": v(-4.24, 43.25) * mm});
            skLineSegment(sketch, "E1046", {"start": v(-4.24, 43.25) * mm, "end": v(-4, 43.15) * mm});
            skLineSegment(sketch, "E1047", {"start": v(-4, 43.15) * mm, "end": v(-3.77, 43.07) * mm});
            skLineSegment(sketch, "E1048", {"start": v(-3.77, 43.07) * mm, "end": v(-3.54, 43) * mm});
            skLineSegment(sketch, "E1049", {"start": v(-3.54, 43) * mm, "end": v(-3.3, 42.94) * mm});
            skLineSegment(sketch, "E1050", {"start": v(-3.3, 42.94) * mm, "end": v(-3.07, 42.9) * mm});
            skLineSegment(sketch, "E1051", {"start": v(-3.07, 42.9) * mm, "end": v(-2.84, 42.86) * mm});
            skLineSegment(sketch, "E1052", {"start": v(-2.84, 42.86) * mm, "end": v(-2.6, 42.84) * mm});
            skLineSegment(sketch, "E1053", {"start": v(0.32, 44.9) * mm, "end": v(0.87, 44.34) * mm});
            skLineSegment(sketch, "E1054", {"start": v(0.87, 44.34) * mm, "end": v(0.87, 44.34) * mm});
            skLineSegment(sketch, "E1055", {"start": v(0.87, 44.34) * mm, "end": v(0.96, 44.45) * mm});
            skLineSegment(sketch, "E1056", {"start": v(0.96, 44.45) * mm, "end": v(1.01, 44.51) * mm});
            skLineSegment(sketch, "E1057", {"start": v(1.01, 44.51) * mm, "end": v(1.04, 44.55) * mm});
            skLineSegment(sketch, "E1058", {"start": v(1.04, 44.55) * mm, "end": v(1.1, 44.63) * mm});
            skLineSegment(sketch, "E1059", {"start": v(1.1, 44.63) * mm, "end": v(1.22, 44.8) * mm});
            skLineSegment(sketch, "E1060", {"start": v(1.22, 44.8) * mm, "end": v(1.28, 44.9) * mm});
            skLineSegment(sketch, "E1061", {"start": v(1.28, 44.9) * mm, "end": v(1.3, 44.92) * mm});
            skLineSegment(sketch, "E1062", {"start": v(1.3, 44.92) * mm, "end": v(1.35, 45) * mm});
            skLineSegment(sketch, "E1063", {"start": v(1.35, 45) * mm, "end": v(1.43, 45.14) * mm});
            skLineSegment(sketch, "E1064", {"start": v(1.43, 45.14) * mm, "end": v(1.45, 45.2) * mm});
            skLineSegment(sketch, "E1065", {"start": v(1.45, 45.2) * mm, "end": v(1.5, 45.3) * mm});
            skLineSegment(sketch, "E1066", {"start": v(1.5, 45.3) * mm, "end": v(1.59, 45.47) * mm});
            skLineSegment(sketch, "E1067", {"start": v(1.59, 45.47) * mm, "end": v(1.66, 45.64) * mm});
            skLineSegment(sketch, "E1068", {"start": v(1.66, 45.64) * mm, "end": v(1.73, 45.82) * mm});
            skLineSegment(sketch, "E1069", {"start": v(1.73, 45.82) * mm, "end": v(1.78, 46) * mm});
            skLineSegment(sketch, "E1070", {"start": v(1.78, 46) * mm, "end": v(1.83, 46.18) * mm});
            skLineSegment(sketch, "E1071", {"start": v(1.83, 46.18) * mm, "end": v(1.87, 46.36) * mm});
            skLineSegment(sketch, "E1072", {"start": v(1.87, 46.36) * mm, "end": v(1.9, 46.54) * mm});
            skLineSegment(sketch, "E1073", {"start": v(1.9, 46.54) * mm, "end": v(1.93, 46.73) * mm});
            skLineSegment(sketch, "E1074", {"start": v(1.93, 46.73) * mm, "end": v(1.94, 46.83) * mm});
            skLineSegment(sketch, "E1075", {"start": v(1.94, 46.83) * mm, "end": v(1.95, 46.98) * mm});
            skLineSegment(sketch, "E1076", {"start": v(1.95, 46.98) * mm, "end": v(1.95, 47.14) * mm});
            skLineSegment(sketch, "E1077", {"start": v(1.95, 47.14) * mm, "end": v(1.95, 47.3) * mm});
            skLineSegment(sketch, "E1078", {"start": v(1.95, 47.3) * mm, "end": v(1.94, 47.45) * mm});
            skLineSegment(sketch, "E1079", {"start": v(1.94, 47.45) * mm, "end": v(1.93, 47.55) * mm});
            skLineSegment(sketch, "E1080", {"start": v(1.93, 47.55) * mm, "end": v(1.91, 47.7) * mm});
            skLineSegment(sketch, "E1081", {"start": v(1.91, 47.7) * mm, "end": v(1.89, 47.85) * mm});
            skLineSegment(sketch, "E1082", {"start": v(1.89, 47.85) * mm, "end": v(1.86, 48) * mm});
            skLineSegment(sketch, "E1083", {"start": v(1.86, 48) * mm, "end": v(1.83, 48.16) * mm});
            skLineSegment(sketch, "E1084", {"start": v(1.83, 48.16) * mm, "end": v(1.79, 48.3) * mm});
            skLineSegment(sketch, "E1085", {"start": v(1.79, 48.3) * mm, "end": v(1.74, 48.46) * mm});
            skLineSegment(sketch, "E1086", {"start": v(1.74, 48.46) * mm, "end": v(1.7, 48.6) * mm});
            skLineSegment(sketch, "E1087", {"start": v(1.7, 48.6) * mm, "end": v(1.64, 48.76) * mm});
            skLineSegment(sketch, "E1088", {"start": v(1.64, 48.76) * mm, "end": v(1.56, 48.95) * mm});
            skLineSegment(sketch, "E1089", {"start": v(1.56, 48.95) * mm, "end": v(1.47, 49.15) * mm});
            skLineSegment(sketch, "E1090", {"start": v(1.47, 49.15) * mm, "end": v(1.37, 49.35) * mm});
            skLineSegment(sketch, "E1091", {"start": v(1.37, 49.35) * mm, "end": v(1.27, 49.53) * mm});
            skLineSegment(sketch, "E1092", {"start": v(1.27, 49.53) * mm, "end": v(1.2, 49.65) * mm});
            skLineSegment(sketch, "E1093", {"start": v(1.2, 49.65) * mm, "end": v(1.13, 49.78) * mm});
            skLineSegment(sketch, "E1094", {"start": v(1.13, 49.78) * mm, "end": v(1.06, 49.88) * mm});
            skLineSegment(sketch, "E1095", {"start": v(1.06, 49.88) * mm, "end": v(0.94, 50.05) * mm});
            skLineSegment(sketch, "E1096", {"start": v(0.94, 50.05) * mm, "end": v(0.9, 50.12) * mm});
            skLineSegment(sketch, "E1097", {"start": v(0.9, 50.12) * mm, "end": v(0.72, 50.35) * mm});
            skLineSegment(sketch, "E1098", {"start": v(0.72, 50.35) * mm, "end": v(0.7, 50.37) * mm});
            skLineSegment(sketch, "E1099", {"start": v(0.7, 50.37) * mm, "end": v(0.68, 50.4) * mm});
            skLineSegment(sketch, "E1100", {"start": v(0.68, 50.4) * mm, "end": v(0.68, 50.4) * mm});
            skLineSegment(sketch, "E1101", {"start": v(0.68, 50.4) * mm, "end": v(0.55, 50.55) * mm});
            skLineSegment(sketch, "E1102", {"start": v(0.55, 50.55) * mm, "end": v(0.54, 50.57) * mm});
            skLineSegment(sketch, "E1103", {"start": v(0.54, 50.57) * mm, "end": v(0.52, 50.59) * mm});
            skLineSegment(sketch, "E1104", {"start": v(0.52, 50.59) * mm, "end": v(0.51, 50.6) * mm});
            skLineSegment(sketch, "E1105", {"start": v(0.51, 50.6) * mm, "end": v(0.47, 50.65) * mm});
            skLineSegment(sketch, "E1106", {"start": v(0.47, 50.65) * mm, "end": v(0.3, 50.84) * mm});
            skLineSegment(sketch, "E1107", {"start": v(0.3, 50.84) * mm, "end": v(0.24, 50.9) * mm});
            skLineSegment(sketch, "E1108", {"start": v(0.24, 50.9) * mm, "end": v(0.12, 51.01) * mm});
            skLineSegment(sketch, "E1109", {"start": v(0.12, 51.01) * mm, "end": v(-0.1, 51.23) * mm});
            skLineSegment(sketch, "E1110", {"start": v(-0.1, 51.23) * mm, "end": v(-0.21, 51.34) * mm});
            skLineSegment(sketch, "E1111", {"start": v(-0.21, 51.34) * mm, "end": v(-0.3, 51.4) * mm});
            skLineSegment(sketch, "E1112", {"start": v(-0.3, 51.4) * mm, "end": v(-0.6, 51.66) * mm});
            skLineSegment(sketch, "E1113", {"start": v(-0.6, 51.66) * mm, "end": v(-0.75, 51.77) * mm});
            skLineSegment(sketch, "E1114", {"start": v(-0.75, 51.77) * mm, "end": v(-0.85, 51.84) * mm});
            skLineSegment(sketch, "E1115", {"start": v(-0.85, 51.84) * mm, "end": v(-0.88, 51.86) * mm});
            skLineSegment(sketch, "E1116", {"start": v(-0.88, 51.86) * mm, "end": v(-0.98, 51.93) * mm});
            skLineSegment(sketch, "E1117", {"start": v(-0.98, 51.93) * mm, "end": v(-1.16, 52.05) * mm});
            skLineSegment(sketch, "E1118", {"start": v(-1.16, 52.05) * mm, "end": v(-1.24, 52.1) * mm});
            skLineSegment(sketch, "E1119", {"start": v(-1.24, 52.1) * mm, "end": v(-1.24, 52.1) * mm});
            skLineSegment(sketch, "E1120", {"start": v(-1.24, 52.1) * mm, "end": v(-1.25, 52.1) * mm});
            skLineSegment(sketch, "E1121", {"start": v(-1.25, 52.1) * mm, "end": v(-1.26, 52.1) * mm});
            skLineSegment(sketch, "E1122", {"start": v(-1.26, 52.1) * mm, "end": v(-1.34, 52.15) * mm});
            skLineSegment(sketch, "E1123", {"start": v(-1.34, 52.15) * mm, "end": v(-1.53, 52.26) * mm});
            skLineSegment(sketch, "E1124", {"start": v(-1.53, 52.26) * mm, "end": v(-1.65, 52.32) * mm});
            skLineSegment(sketch, "E1125", {"start": v(-1.65, 52.32) * mm, "end": v(-1.71, 52.35) * mm});
            skLineSegment(sketch, "E1126", {"start": v(-1.71, 52.35) * mm, "end": v(-1.96, 52.46) * mm});
            skLineSegment(sketch, "E1127", {"start": v(-1.96, 52.46) * mm, "end": v(-2.18, 52.55) * mm});
            skLineSegment(sketch, "E1128", {"start": v(-2.18, 52.55) * mm, "end": v(-2.33, 52.6) * mm});
            skLineSegment(sketch, "E1129", {"start": v(-2.33, 52.6) * mm, "end": v(-2.48, 52.66) * mm});
            skLineSegment(sketch, "E1130", {"start": v(-2.48, 52.66) * mm, "end": v(-2.63, 52.7) * mm});
            skLineSegment(sketch, "E1131", {"start": v(-2.63, 52.7) * mm, "end": v(-2.78, 52.73) * mm});
            skLineSegment(sketch, "E1132", {"start": v(-2.78, 52.73) * mm, "end": v(-2.93, 52.77) * mm});
            skLineSegment(sketch, "E1133", {"start": v(-2.93, 52.77) * mm, "end": v(-3.08, 52.8) * mm});
            skLineSegment(sketch, "E1134", {"start": v(-3.08, 52.8) * mm, "end": v(-3.23, 52.82) * mm});
            skLineSegment(sketch, "E1135", {"start": v(-3.23, 52.82) * mm, "end": v(-3.38, 52.83) * mm});
            skLineSegment(sketch, "E1136", {"start": v(-3.38, 52.83) * mm, "end": v(-3.5, 52.84) * mm});
            skLineSegment(sketch, "E1137", {"start": v(-3.5, 52.84) * mm, "end": v(-3.86, 52.85) * mm});
            skLineSegment(sketch, "E1138", {"start": v(-3.86, 52.85) * mm, "end": v(-3.98, 52.84) * mm});
            skLineSegment(sketch, "E1139", {"start": v(-3.98, 52.84) * mm, "end": v(-4.16, 52.83) * mm});
            skLineSegment(sketch, "E1140", {"start": v(-4.16, 52.83) * mm, "end": v(-4.33, 52.8) * mm});
            skLineSegment(sketch, "E1141", {"start": v(-4.33, 52.8) * mm, "end": v(-4.5, 52.78) * mm});
            skLineSegment(sketch, "E1142", {"start": v(-4.5, 52.78) * mm, "end": v(-4.66, 52.75) * mm});
            skLineSegment(sketch, "E1143", {"start": v(-4.66, 52.75) * mm, "end": v(-4.82, 52.7) * mm});
            skLineSegment(sketch, "E1144", {"start": v(-4.82, 52.7) * mm, "end": v(-4.98, 52.66) * mm});
            skLineSegment(sketch, "E1145", {"start": v(-4.98, 52.66) * mm, "end": v(-5.13, 52.6) * mm});
            skLineSegment(sketch, "E1146", {"start": v(-5.13, 52.6) * mm, "end": v(-5.29, 52.55) * mm});
            skLineSegment(sketch, "E1147", {"start": v(-5.29, 52.55) * mm, "end": v(-5.36, 52.52) * mm});
            skLineSegment(sketch, "E1148", {"start": v(-5.36, 52.52) * mm, "end": v(-5.38, 52.5) * mm});
            skLineSegment(sketch, "E1149", {"start": v(-5.38, 52.5) * mm, "end": v(-5.4, 52.5) * mm});
            skLineSegment(sketch, "E1150", {"start": v(-5.4, 52.5) * mm, "end": v(-5.4, 52.5) * mm});
            skLineSegment(sketch, "E1151", {"start": v(-5.4, 52.5) * mm, "end": v(-5.49, 52.46) * mm});
            skLineSegment(sketch, "E1152", {"start": v(-5.49, 52.46) * mm, "end": v(-5.6, 52.4) * mm});
            skLineSegment(sketch, "E1153", {"start": v(-5.6, 52.4) * mm, "end": v(-5.74, 52.33) * mm});
            skLineSegment(sketch, "E1154", {"start": v(-5.74, 52.33) * mm, "end": v(-5.81, 52.3) * mm});
            skLineSegment(sketch, "E1155", {"start": v(-5.81, 52.3) * mm, "end": v(-5.84, 52.28) * mm});
            skLineSegment(sketch, "E1156", {"start": v(-5.84, 52.28) * mm, "end": v(-5.87, 52.26) * mm});
            skLineSegment(sketch, "E1157", {"start": v(-5.87, 52.26) * mm, "end": v(-5.96, 52.2) * mm});
            skLineSegment(sketch, "E1158", {"start": v(-5.96, 52.2) * mm, "end": v(-6.08, 52.13) * mm});
            skLineSegment(sketch, "E1159", {"start": v(-6.08, 52.13) * mm, "end": v(-6.22, 52.03) * mm});
            skLineSegment(sketch, "E1160", {"start": v(-6.22, 52.03) * mm, "end": v(-6.34, 51.94) * mm});
            skLineSegment(sketch, "E1161", {"start": v(-6.34, 51.94) * mm, "end": v(-6.43, 51.87) * mm});
            skLineSegment(sketch, "E1162", {"start": v(-6.43, 51.87) * mm, "end": v(-6.46, 51.85) * mm});
            skLineSegment(sketch, "E1163", {"start": v(-6.46, 51.85) * mm, "end": v(-6.53, 51.8) * mm});
            skLineSegment(sketch, "E1164", {"start": v(-6.53, 51.8) * mm, "end": v(-6.56, 51.77) * mm});
            skLineSegment(sketch, "E1165", {"start": v(-6.56, 51.77) * mm, "end": v(-6.01, 51.22) * mm});
            skLineSegment(sketch, "E1166", {"start": v(-6.01, 51.22) * mm, "end": v(-5.94, 51.25) * mm});
            skLineSegment(sketch, "E1167", {"start": v(-5.94, 51.25) * mm, "end": v(-5.84, 51.29) * mm});
            skLineSegment(sketch, "E1168", {"start": v(-5.84, 51.29) * mm, "end": v(-5.75, 51.31) * mm});
            skLineSegment(sketch, "E1169", {"start": v(-5.75, 51.31) * mm, "end": v(-5.67, 51.33) * mm});
            skLineSegment(sketch, "E1170", {"start": v(-5.67, 51.33) * mm, "end": v(-5.58, 51.34) * mm});
            skLineSegment(sketch, "E1171", {"start": v(-5.58, 51.34) * mm, "end": v(-5.5, 51.35) * mm});
            skLineSegment(sketch, "E1172", {"start": v(-5.5, 51.35) * mm, "end": v(-5.4, 51.34) * mm});
            skLineSegment(sketch, "E1173", {"start": v(-5.4, 51.34) * mm, "end": v(-5.32, 51.33) * mm});
            skLineSegment(sketch, "E1174", {"start": v(-5.32, 51.33) * mm, "end": v(-5.24, 51.3) * mm});
            skLineSegment(sketch, "E1175", {"start": v(-5.24, 51.3) * mm, "end": v(-5.17, 51.27) * mm});
            skLineSegment(sketch, "E1176", {"start": v(-5.17, 51.27) * mm, "end": v(-5.09, 51.23) * mm});
            skLineSegment(sketch, "E1177", {"start": v(-5.09, 51.23) * mm, "end": v(-5.01, 51.18) * mm});
            skLineSegment(sketch, "E1178", {"start": v(-5.01, 51.18) * mm, "end": v(-4.94, 51.12) * mm});
            skLineSegment(sketch, "E1179", {"start": v(-4.94, 51.12) * mm, "end": v(-4.88, 51.06) * mm});
            skLineSegment(sketch, "E1180", {"start": v(-4.88, 51.06) * mm, "end": v(0.2, 45.98) * mm});
            skLineSegment(sketch, "E1181", {"start": v(0.2, 45.98) * mm, "end": v(0.28, 45.89) * mm});
            skLineSegment(sketch, "E1182", {"start": v(0.28, 45.89) * mm, "end": v(0.28, 45.88) * mm});
            skLineSegment(sketch, "E1183", {"start": v(0.28, 45.88) * mm, "end": v(0.32, 45.83) * mm});
            skLineSegment(sketch, "E1184", {"start": v(0.32, 45.83) * mm, "end": v(0.37, 45.73) * mm});
            skLineSegment(sketch, "E1185", {"start": v(0.37, 45.73) * mm, "end": v(0.41, 45.63) * mm});
            skLineSegment(sketch, "E1186", {"start": v(0.41, 45.63) * mm, "end": v(0.44, 45.53) * mm});
            skLineSegment(sketch, "E1187", {"start": v(0.44, 45.53) * mm, "end": v(0.45, 45.43) * mm});
            skLineSegment(sketch, "E1188", {"start": v(0.45, 45.43) * mm, "end": v(0.45, 45.32) * mm});
            skLineSegment(sketch, "E1189", {"start": v(0.45, 45.32) * mm, "end": v(0.43, 45.21) * mm});
            skLineSegment(sketch, "E1190", {"start": v(0.43, 45.21) * mm, "end": v(0.4, 45.1) * mm});
            skLineSegment(sketch, "E1191", {"start": v(0.4, 45.1) * mm, "end": v(0.36, 44.98) * mm});
            skLineSegment(sketch, "E1192", {"start": v(0.36, 44.98) * mm, "end": v(0.32, 44.9) * mm});
            skLineSegment(sketch, "E1193", {"start": v(-6.43, 49.82) * mm, "end": v(-6.43, 49.83) * mm});
            skLineSegment(sketch, "E1194", {"start": v(-6.43, 49.83) * mm, "end": v(-6.43, 49.82) * mm});
            skLineSegment(sketch, "E1195", {"start": v(-6.43, 49.82) * mm, "end": v(-6.43, 49.82) * mm});
            skLineSegment(sketch, "E1196", {"start": v(12.64, 46.41) * mm, "end": v(12.65, 46.4) * mm});
            skLineSegment(sketch, "E1197", {"start": v(12.65, 46.4) * mm, "end": v(12.66, 46.42) * mm});
            skLineSegment(sketch, "E1198", {"start": v(12.66, 46.42) * mm, "end": v(12.68, 46.43) * mm});
            skLineSegment(sketch, "E1199", {"start": v(12.68, 46.43) * mm, "end": v(12.74, 46.52) * mm});
            skLineSegment(sketch, "E1200", {"start": v(12.74, 46.52) * mm, "end": v(12.84, 46.66) * mm});
            skLineSegment(sketch, "E1201", {"start": v(12.84, 46.66) * mm, "end": v(12.88, 46.7) * mm});
            skLineSegment(sketch, "E1202", {"start": v(12.88, 46.7) * mm, "end": v(12.87, 46.72) * mm});
            skLineSegment(sketch, "E1203", {"start": v(12.87, 46.72) * mm, "end": v(12.87, 46.72) * mm});
            skLineSegment(sketch, "E1204", {"start": v(12.87, 46.72) * mm, "end": v(12.88, 46.72) * mm});
            skLineSegment(sketch, "E1205", {"start": v(12.88, 46.72) * mm, "end": v(12.88, 46.72) * mm});
            skLineSegment(sketch, "E1206", {"start": v(12.88, 46.72) * mm, "end": v(12.92, 46.78) * mm});
            skLineSegment(sketch, "E1207", {"start": v(12.92, 46.78) * mm, "end": v(12.98, 46.9) * mm});
            skLineSegment(sketch, "E1208", {"start": v(12.98, 46.9) * mm, "end": v(13.04, 47) * mm});
            skLineSegment(sketch, "E1209", {"start": v(13.04, 47) * mm, "end": v(13.1, 47.12) * mm});
            skLineSegment(sketch, "E1210", {"start": v(13.1, 47.12) * mm, "end": v(13.14, 47.24) * mm});
            skLineSegment(sketch, "E1211", {"start": v(13.14, 47.24) * mm, "end": v(13.17, 47.36) * mm});
            skLineSegment(sketch, "E1212", {"start": v(13.17, 47.36) * mm, "end": v(13.2, 47.5) * mm});
            skLineSegment(sketch, "E1213", {"start": v(13.2, 47.5) * mm, "end": v(13.23, 47.62) * mm});
            skLineSegment(sketch, "E1214", {"start": v(13.23, 47.62) * mm, "end": v(13.25, 47.75) * mm});
            skLineSegment(sketch, "E1215", {"start": v(13.25, 47.75) * mm, "end": v(13.26, 47.82) * mm});
            skLineSegment(sketch, "E1216", {"start": v(13.26, 47.82) * mm, "end": v(13.26, 48.15) * mm});
            skLineSegment(sketch, "E1217", {"start": v(13.26, 48.15) * mm, "end": v(13.25, 48.25) * mm});
            skLineSegment(sketch, "E1218", {"start": v(13.25, 48.25) * mm, "end": v(13.22, 48.41) * mm});
            skLineSegment(sketch, "E1219", {"start": v(13.22, 48.41) * mm, "end": v(13.19, 48.57) * mm});
            skLineSegment(sketch, "E1220", {"start": v(13.19, 48.57) * mm, "end": v(13.14, 48.74) * mm});
            skLineSegment(sketch, "E1221", {"start": v(13.14, 48.74) * mm, "end": v(13.08, 48.9) * mm});
            skLineSegment(sketch, "E1222", {"start": v(13.08, 48.9) * mm, "end": v(13.02, 49.06) * mm});
            skLineSegment(sketch, "E1223", {"start": v(13.02, 49.06) * mm, "end": v(12.94, 49.21) * mm});
            skLineSegment(sketch, "E1224", {"start": v(12.94, 49.21) * mm, "end": v(12.85, 49.37) * mm});
            skLineSegment(sketch, "E1225", {"start": v(12.85, 49.37) * mm, "end": v(12.75, 49.53) * mm});
            skLineSegment(sketch, "E1226", {"start": v(12.75, 49.53) * mm, "end": v(12.64, 49.69) * mm});
            skLineSegment(sketch, "E1227", {"start": v(12.64, 49.69) * mm, "end": v(12.53, 49.83) * mm});
            skLineSegment(sketch, "E1228", {"start": v(12.53, 49.83) * mm, "end": v(12.5, 49.87) * mm});
            skLineSegment(sketch, "E1229", {"start": v(12.5, 49.87) * mm, "end": v(12.35, 50.04) * mm});
            skLineSegment(sketch, "E1230", {"start": v(12.35, 50.04) * mm, "end": v(12.12, 50.28) * mm});
            skLineSegment(sketch, "E1231", {"start": v(12.12, 50.28) * mm, "end": v(12.06, 50.33) * mm});
            skLineSegment(sketch, "E1232", {"start": v(12.06, 50.33) * mm, "end": v(11.97, 50.4) * mm});
            skLineSegment(sketch, "E1233", {"start": v(11.97, 50.4) * mm, "end": v(11.9, 50.47) * mm});
            skLineSegment(sketch, "E1234", {"start": v(11.9, 50.47) * mm, "end": v(11.8, 50.55) * mm});
            skLineSegment(sketch, "E1235", {"start": v(11.8, 50.55) * mm, "end": v(11.66, 50.64) * mm});
            skLineSegment(sketch, "E1236", {"start": v(11.66, 50.64) * mm, "end": v(11.58, 50.7) * mm});
            skLineSegment(sketch, "E1237", {"start": v(11.58, 50.7) * mm, "end": v(11.58, 50.7) * mm});
            skLineSegment(sketch, "E1238", {"start": v(11.58, 50.7) * mm, "end": v(11.57, 50.7) * mm});
            skLineSegment(sketch, "E1239", {"start": v(11.57, 50.7) * mm, "end": v(11.57, 50.7) * mm});
            skLineSegment(sketch, "E1240", {"start": v(11.57, 50.7) * mm, "end": v(11.59, 50.73) * mm});
            skLineSegment(sketch, "E1241", {"start": v(11.59, 50.73) * mm, "end": v(11.6, 50.77) * mm});
            skLineSegment(sketch, "E1242", {"start": v(11.6, 50.77) * mm, "end": v(11.62, 50.8) * mm});
            skLineSegment(sketch, "E1243", {"start": v(11.62, 50.8) * mm, "end": v(11.62, 50.84) * mm});
            skLineSegment(sketch, "E1244", {"start": v(11.62, 50.84) * mm, "end": v(11.62, 50.88) * mm});
            skLineSegment(sketch, "E1245", {"start": v(11.62, 50.88) * mm, "end": v(11.61, 50.92) * mm});
            skLineSegment(sketch, "E1246", {"start": v(11.61, 50.92) * mm, "end": v(11.6, 50.96) * mm});
            skLineSegment(sketch, "E1247", {"start": v(11.6, 50.96) * mm, "end": v(11.57, 51) * mm});
            skLineSegment(sketch, "E1248", {"start": v(11.57, 51) * mm, "end": v(11.54, 51.06) * mm});
            skLineSegment(sketch, "E1249", {"start": v(11.54, 51.06) * mm, "end": v(11.49, 51.13) * mm});
            skLineSegment(sketch, "E1250", {"start": v(11.49, 51.13) * mm, "end": v(11.47, 51.16) * mm});
            skLineSegment(sketch, "E1251", {"start": v(11.47, 51.16) * mm, "end": v(11.45, 51.18) * mm});
            skLineSegment(sketch, "E1252", {"start": v(11.45, 51.18) * mm, "end": v(11.44, 51.2) * mm});
            skLineSegment(sketch, "E1253", {"start": v(11.44, 51.2) * mm, "end": v(11.43, 51.2) * mm});
            skLineSegment(sketch, "E1254", {"start": v(11.43, 51.2) * mm, "end": v(11.43, 51.21) * mm});
            skLineSegment(sketch, "E1255", {"start": v(11.43, 51.21) * mm, "end": v(11.38, 51.29) * mm});
            skLineSegment(sketch, "E1256", {"start": v(11.38, 51.29) * mm, "end": v(11.31, 51.4) * mm});
            skLineSegment(sketch, "E1257", {"start": v(11.31, 51.4) * mm, "end": v(11.25, 51.5) * mm});
            skLineSegment(sketch, "E1258", {"start": v(11.25, 51.5) * mm, "end": v(11.21, 51.58) * mm});
            skLineSegment(sketch, "E1259", {"start": v(11.21, 51.58) * mm, "end": v(11.21, 51.57) * mm});
            skLineSegment(sketch, "E1260", {"start": v(11.21, 51.57) * mm, "end": v(11.2, 51.58) * mm});
            skLineSegment(sketch, "E1261", {"start": v(11.2, 51.58) * mm, "end": v(11.2, 51.6) * mm});
            skLineSegment(sketch, "E1262", {"start": v(11.2, 51.6) * mm, "end": v(11.18, 51.62) * mm});
            skLineSegment(sketch, "E1263", {"start": v(11.18, 51.62) * mm, "end": v(11.15, 51.7) * mm});
            skLineSegment(sketch, "E1264", {"start": v(11.15, 51.7) * mm, "end": v(11.1, 51.86) * mm});
            skLineSegment(sketch, "E1265", {"start": v(11.1, 51.86) * mm, "end": v(11.06, 52) * mm});
            skLineSegment(sketch, "E1266", {"start": v(11.06, 52) * mm, "end": v(11.05, 52.08) * mm});
            skLineSegment(sketch, "E1267", {"start": v(11.05, 52.08) * mm, "end": v(11.04, 52.15) * mm});
            skLineSegment(sketch, "E1268", {"start": v(11.04, 52.15) * mm, "end": v(11.04, 52.22) * mm});
            skLineSegment(sketch, "E1269", {"start": v(11.04, 52.22) * mm, "end": v(11.04, 52.28) * mm});
            skLineSegment(sketch, "E1270", {"start": v(11.04, 52.28) * mm, "end": v(11.05, 52.36) * mm});
            skLineSegment(sketch, "E1271", {"start": v(11.05, 52.36) * mm, "end": v(11.05, 52.39) * mm});
            skLineSegment(sketch, "E1272", {"start": v(11.05, 52.39) * mm, "end": v(10.74, 52.69) * mm});
            skLineSegment(sketch, "E1273", {"start": v(10.74, 52.69) * mm, "end": v(9.97, 51.92) * mm});
            skLineSegment(sketch, "E1274", {"start": v(9.97, 51.92) * mm, "end": v(10.82, 51.07) * mm});
            skLineSegment(sketch, "E1275", {"start": v(10.82, 51.07) * mm, "end": v(10.8, 51.07) * mm});
            skLineSegment(sketch, "E1276", {"start": v(10.8, 51.07) * mm, "end": v(10.76, 51.08) * mm});
            skLineSegment(sketch, "E1277", {"start": v(10.76, 51.08) * mm, "end": v(10.66, 51.11) * mm});
            skLineSegment(sketch, "E1278", {"start": v(10.66, 51.11) * mm, "end": v(10.56, 51.14) * mm});
            skLineSegment(sketch, "E1279", {"start": v(10.56, 51.14) * mm, "end": v(10.45, 51.16) * mm});
            skLineSegment(sketch, "E1280", {"start": v(10.45, 51.16) * mm, "end": v(10.34, 51.17) * mm});
            skLineSegment(sketch, "E1281", {"start": v(10.34, 51.17) * mm, "end": v(10.26, 51.18) * mm});
            skLineSegment(sketch, "E1282", {"start": v(10.26, 51.18) * mm, "end": v(10.12, 51.19) * mm});
            skLineSegment(sketch, "E1283", {"start": v(10.12, 51.19) * mm, "end": v(10, 51.19) * mm});
            skLineSegment(sketch, "E1284", {"start": v(10, 51.19) * mm, "end": v(9.89, 51.18) * mm});
            skLineSegment(sketch, "E1285", {"start": v(9.89, 51.18) * mm, "end": v(9.78, 51.17) * mm});
            skLineSegment(sketch, "E1286", {"start": v(9.78, 51.17) * mm, "end": v(9.66, 51.16) * mm});
            skLineSegment(sketch, "E1287", {"start": v(9.66, 51.16) * mm, "end": v(9.56, 51.13) * mm});
            skLineSegment(sketch, "E1288", {"start": v(9.56, 51.13) * mm, "end": v(9.45, 51.1) * mm});
            skLineSegment(sketch, "E1289", {"start": v(9.45, 51.1) * mm, "end": v(9.34, 51.07) * mm});
            skLineSegment(sketch, "E1290", {"start": v(9.34, 51.07) * mm, "end": v(9.23, 51.04) * mm});
            skLineSegment(sketch, "E1291", {"start": v(9.23, 51.04) * mm, "end": v(9.16, 51) * mm});
            skLineSegment(sketch, "E1292", {"start": v(9.16, 51) * mm, "end": v(9.14, 51) * mm});
            skLineSegment(sketch, "E1293", {"start": v(9.14, 51) * mm, "end": v(9.13, 50.99) * mm});
            skLineSegment(sketch, "E1294", {"start": v(9.13, 50.99) * mm, "end": v(9.13, 51) * mm});
            skLineSegment(sketch, "E1295", {"start": v(9.13, 51) * mm, "end": v(9.06, 50.96) * mm});
            skLineSegment(sketch, "E1296", {"start": v(9.06, 50.96) * mm, "end": v(8.91, 50.89) * mm});
            skLineSegment(sketch, "E1297", {"start": v(8.91, 50.89) * mm, "end": v(8.76, 50.8) * mm});
            skLineSegment(sketch, "E1298", {"start": v(8.76, 50.8) * mm, "end": v(8.7, 50.75) * mm});
            skLineSegment(sketch, "E1299", {"start": v(8.7, 50.75) * mm, "end": v(8.49, 50.6) * mm});
            skLineSegment(sketch, "E1300", {"start": v(8.49, 50.6) * mm, "end": v(8.48, 50.58) * mm});
            skLineSegment(sketch, "E1301", {"start": v(8.48, 50.58) * mm, "end": v(8.78, 50.27) * mm});
            skLineSegment(sketch, "E1302", {"start": v(8.78, 50.27) * mm, "end": v(8.82, 50.29) * mm});
            skLineSegment(sketch, "E1303", {"start": v(8.82, 50.29) * mm, "end": v(8.87, 50.3) * mm});
            skLineSegment(sketch, "E1304", {"start": v(8.87, 50.3) * mm, "end": v(8.93, 50.33) * mm});
            skLineSegment(sketch, "E1305", {"start": v(8.93, 50.33) * mm, "end": v(8.98, 50.34) * mm});
            skLineSegment(sketch, "E1306", {"start": v(8.98, 50.34) * mm, "end": v(9.04, 50.34) * mm});
            skLineSegment(sketch, "E1307", {"start": v(9.04, 50.34) * mm, "end": v(9.11, 50.34) * mm});
            skLineSegment(sketch, "E1308", {"start": v(9.11, 50.34) * mm, "end": v(9.19, 50.33) * mm});
            skLineSegment(sketch, "E1309", {"start": v(9.19, 50.33) * mm, "end": v(9.26, 50.3) * mm});
            skLineSegment(sketch, "E1310", {"start": v(9.26, 50.3) * mm, "end": v(9.33, 50.26) * mm});
            skLineSegment(sketch, "E1311", {"start": v(9.33, 50.26) * mm, "end": v(9.38, 50.22) * mm});
            skLineSegment(sketch, "E1312", {"start": v(9.38, 50.22) * mm, "end": v(12.27, 47.34) * mm});
            skLineSegment(sketch, "E1313", {"start": v(12.27, 47.34) * mm, "end": v(12.3, 47.29) * mm});
            skLineSegment(sketch, "E1314", {"start": v(12.3, 47.29) * mm, "end": v(12.34, 47.24) * mm});
            skLineSegment(sketch, "E1315", {"start": v(12.34, 47.24) * mm, "end": v(12.37, 47.2) * mm});
            skLineSegment(sketch, "E1316", {"start": v(12.37, 47.2) * mm, "end": v(12.4, 47.14) * mm});
            skLineSegment(sketch, "E1317", {"start": v(12.4, 47.14) * mm, "end": v(12.4, 47.1) * mm});
            skLineSegment(sketch, "E1318", {"start": v(12.4, 47.1) * mm, "end": v(12.41, 47.02) * mm});
            skLineSegment(sketch, "E1319", {"start": v(12.41, 47.02) * mm, "end": v(12.4, 46.94) * mm});
            skLineSegment(sketch, "E1320", {"start": v(12.4, 46.94) * mm, "end": v(12.4, 46.85) * mm});
            skLineSegment(sketch, "E1321", {"start": v(12.4, 46.85) * mm, "end": v(12.36, 46.76) * mm});
            skLineSegment(sketch, "E1322", {"start": v(12.36, 46.76) * mm, "end": v(12.34, 46.71) * mm});
            skLineSegment(sketch, "E1323", {"start": v(12.34, 46.71) * mm, "end": v(12.62, 46.43) * mm});
            skLineSegment(sketch, "E1324", {"start": v(12.62, 46.43) * mm, "end": v(12.63, 46.44) * mm});
            skLineSegment(sketch, "E1325", {"start": v(12.63, 46.44) * mm, "end": v(12.64, 46.44) * mm});
            skLineSegment(sketch, "E1326", {"start": v(12.64, 46.44) * mm, "end": v(12.64, 46.43) * mm});
            skLineSegment(sketch, "E1327", {"start": v(12.64, 46.43) * mm, "end": v(12.64, 46.42) * mm});
            skLineSegment(sketch, "E1328", {"start": v(12.64, 46.42) * mm, "end": v(12.64, 46.41) * mm});
            skLineSegment(sketch, "E1329", {"start": v(-10.14, 34.7) * mm, "end": v(-10.1, 34.8) * mm});
            skLineSegment(sketch, "E1330", {"start": v(-10.1, 34.8) * mm, "end": v(-10.03, 34.96) * mm});
            skLineSegment(sketch, "E1331", {"start": v(-10.03, 34.96) * mm, "end": v(-10.01, 35.02) * mm});
            skLineSegment(sketch, "E1332", {"start": v(-10.01, 35.02) * mm, "end": v(-10, 35.08) * mm});
            skLineSegment(sketch, "E1333", {"start": v(-10, 35.08) * mm, "end": v(-10, 35.13) * mm});
            skLineSegment(sketch, "E1334", {"start": v(-10, 35.13) * mm, "end": v(-10.02, 35.18) * mm});
            skLineSegment(sketch, "E1335", {"start": v(-10.02, 35.18) * mm, "end": v(-10.03, 35.22) * mm});
            skLineSegment(sketch, "E1336", {"start": v(-10.03, 35.22) * mm, "end": v(-10.06, 35.27) * mm});
            skLineSegment(sketch, "E1337", {"start": v(-10.06, 35.27) * mm, "end": v(-10.09, 35.31) * mm});
            skLineSegment(sketch, "E1338", {"start": v(-10.09, 35.31) * mm, "end": v(-10.12, 35.35) * mm});
            skLineSegment(sketch, "E1339", {"start": v(-10.12, 35.35) * mm, "end": v(-10.15, 35.4) * mm});
            skLineSegment(sketch, "E1340", {"start": v(-10.15, 35.4) * mm, "end": v(-15.5, 40.73) * mm});
            skLineSegment(sketch, "E1341", {"start": v(-15.5, 40.73) * mm, "end": v(-15.54, 40.77) * mm});
            skLineSegment(sketch, "E1342", {"start": v(-15.54, 40.77) * mm, "end": v(-15.6, 40.82) * mm});
            skLineSegment(sketch, "E1343", {"start": v(-15.6, 40.82) * mm, "end": v(-15.67, 40.86) * mm});
            skLineSegment(sketch, "E1344", {"start": v(-15.67, 40.86) * mm, "end": v(-15.73, 40.89) * mm});
            skLineSegment(sketch, "E1345", {"start": v(-15.73, 40.89) * mm, "end": v(-15.79, 40.9) * mm});
            skLineSegment(sketch, "E1346", {"start": v(-15.79, 40.9) * mm, "end": v(-15.85, 40.9) * mm});
            skLineSegment(sketch, "E1347", {"start": v(-15.85, 40.9) * mm, "end": v(-15.92, 40.88) * mm});
            skLineSegment(sketch, "E1348", {"start": v(-15.92, 40.88) * mm, "end": v(-16, 40.85) * mm});
            skLineSegment(sketch, "E1349", {"start": v(-16, 40.85) * mm, "end": v(-16.1, 40.8) * mm});
            skLineSegment(sketch, "E1350", {"start": v(-16.1, 40.8) * mm, "end": v(-16.2, 40.76) * mm});
            skLineSegment(sketch, "E1351", {"start": v(-16.2, 40.76) * mm, "end": v(-16.2, 34.7) * mm});
            skLineSegment(sketch, "E1352", {"start": v(-16.2, 34.7) * mm, "end": v(-10.14, 34.7) * mm});
            skLineSegment(sketch, "E1353", {"start": v(-8.57, 51.02) * mm, "end": v(-8.58, 51.03) * mm});
            skLineSegment(sketch, "E1354", {"start": v(-8.58, 51.03) * mm, "end": v(-8.58, 51.02) * mm});
            skLineSegment(sketch, "E1355", {"start": v(-8.58, 51.02) * mm, "end": v(-8.58, 51.02) * mm});
            skLineSegment(sketch, "E1356", {"start": v(-8.58, 51.02) * mm, "end": v(-8.57, 51.02) * mm});
            skLineSegment(sketch, "E1357", {"start": v(-8.52, 51.08) * mm, "end": v(-8.52, 51.08) * mm});
            skLineSegment(sketch, "E1358", {"start": v(-8.52, 51.08) * mm, "end": v(-8.53, 51.08) * mm});
            skLineSegment(sketch, "E1359", {"start": v(-8.53, 51.08) * mm, "end": v(-8.52, 51.07) * mm});
            skLineSegment(sketch, "E1360", {"start": v(-8.52, 51.07) * mm, "end": v(-8.52, 51.08) * mm});
            skLineSegment(sketch, "E1361", {"start": v(5.58, 52.3) * mm, "end": v(5.57, 52.3) * mm});
            skLineSegment(sketch, "E1362", {"start": v(5.57, 52.3) * mm, "end": v(5.57, 52.3) * mm});
            skLineSegment(sketch, "E1363", {"start": v(5.57, 52.3) * mm, "end": v(5.58, 52.3) * mm});
            skLineSegment(sketch, "E1364", {"start": v(-12, 52.65) * mm, "end": v(-11.98, 52.64) * mm});
            skLineSegment(sketch, "E1365", {"start": v(-11.98, 52.64) * mm, "end": v(-11.94, 52.64) * mm});
            skLineSegment(sketch, "E1366", {"start": v(-11.94, 52.64) * mm, "end": v(-11.9, 52.64) * mm});
            skLineSegment(sketch, "E1367", {"start": v(-11.9, 52.64) * mm, "end": v(-11.85, 52.66) * mm});
            skLineSegment(sketch, "E1368", {"start": v(-11.85, 52.66) * mm, "end": v(-11.81, 52.69) * mm});
            skLineSegment(sketch, "E1369", {"start": v(-11.81, 52.69) * mm, "end": v(-11.8, 52.7) * mm});
            skLineSegment(sketch, "E1370", {"start": v(-11.8, 52.7) * mm, "end": v(-11.78, 52.71) * mm});
            skLineSegment(sketch, "E1371", {"start": v(-11.78, 52.71) * mm, "end": v(-11.75, 52.74) * mm});
            skLineSegment(sketch, "E1372", {"start": v(-11.75, 52.74) * mm, "end": v(-11.73, 52.77) * mm});
            skLineSegment(sketch, "E1373", {"start": v(-11.73, 52.77) * mm, "end": v(-11.72, 52.8) * mm});
            skLineSegment(sketch, "E1374", {"start": v(-11.72, 52.8) * mm, "end": v(-11.71, 52.84) * mm});
            skLineSegment(sketch, "E1375", {"start": v(-11.71, 52.84) * mm, "end": v(-11.71, 52.89) * mm});
            skLineSegment(sketch, "E1376", {"start": v(-11.71, 52.89) * mm, "end": v(-11.72, 52.93) * mm});
            skLineSegment(sketch, "E1377", {"start": v(-11.72, 52.93) * mm, "end": v(-11.73, 52.97) * mm});
            skLineSegment(sketch, "E1378", {"start": v(-11.73, 52.97) * mm, "end": v(-11.75, 53) * mm});
            skLineSegment(sketch, "E1379", {"start": v(-11.75, 53) * mm, "end": v(-11.75, 53) * mm});
            skLineSegment(sketch, "E1380", {"start": v(-11.75, 53) * mm, "end": v(-11.78, 53.06) * mm});
            skLineSegment(sketch, "E1381", {"start": v(-11.78, 53.06) * mm, "end": v(-11.84, 53.15) * mm});
            skLineSegment(sketch, "E1382", {"start": v(-11.84, 53.15) * mm, "end": v(-11.88, 53.2) * mm});
            skLineSegment(sketch, "E1383", {"start": v(-11.88, 53.2) * mm, "end": v(-12, 53.39) * mm});
            skLineSegment(sketch, "E1384", {"start": v(-12, 53.39) * mm, "end": v(-12.03, 53.42) * mm});
            skLineSegment(sketch, "E1385", {"start": v(-12.03, 53.42) * mm, "end": v(-12.05, 53.45) * mm});
            skLineSegment(sketch, "E1386", {"start": v(-12.05, 53.45) * mm, "end": v(-12.06, 53.46) * mm});
            skLineSegment(sketch, "E1387", {"start": v(-12.06, 53.46) * mm, "end": v(-12.06, 53.46) * mm});
            skLineSegment(sketch, "E1388", {"start": v(-12.06, 53.46) * mm, "end": v(-12.05, 53.47) * mm});
            skLineSegment(sketch, "E1389", {"start": v(-12.05, 53.47) * mm, "end": v(-12.1, 53.55) * mm});
            skLineSegment(sketch, "E1390", {"start": v(-12.1, 53.55) * mm, "end": v(-12.14, 53.64) * mm});
            skLineSegment(sketch, "E1391", {"start": v(-12.14, 53.64) * mm, "end": v(-12.18, 53.74) * mm});
            skLineSegment(sketch, "E1392", {"start": v(-12.18, 53.74) * mm, "end": v(-12.21, 53.84) * mm});
            skLineSegment(sketch, "E1393", {"start": v(-12.21, 53.84) * mm, "end": v(-12.24, 53.95) * mm});
            skLineSegment(sketch, "E1394", {"start": v(-12.24, 53.95) * mm, "end": v(-12.25, 54) * mm});
            skLineSegment(sketch, "E1395", {"start": v(-12.25, 54) * mm, "end": v(-12.25, 54.31) * mm});
            skLineSegment(sketch, "E1396", {"start": v(-12.25, 54.31) * mm, "end": v(-12.54, 54.6) * mm});
            skLineSegment(sketch, "E1397", {"start": v(-12.54, 54.6) * mm, "end": v(-13.26, 53.87) * mm});
            skLineSegment(sketch, "E1398", {"start": v(-13.26, 53.87) * mm, "end": v(-12.08, 52.69) * mm});
            skLineSegment(sketch, "E1399", {"start": v(-12.08, 52.69) * mm, "end": v(-12.05, 52.67) * mm});
            skLineSegment(sketch, "E1400", {"start": v(-12.05, 52.67) * mm, "end": v(-12, 52.65) * mm});
            skLineSegment(sketch, "E1401", {"start": v(5.36, 52.73) * mm, "end": v(5.36, 52.73) * mm});
            skLineSegment(sketch, "E1402", {"start": v(5.36, 52.73) * mm, "end": v(5.35, 52.73) * mm});
            skLineSegment(sketch, "E1403", {"start": v(5.35, 52.73) * mm, "end": v(5.36, 52.73) * mm});
            skLineSegment(sketch, "E1404", {"start": v(3.47, 47.52) * mm, "end": v(3.54, 47.5) * mm});
            skLineSegment(sketch, "E1405", {"start": v(3.54, 47.5) * mm, "end": v(3.58, 47.5) * mm});
            skLineSegment(sketch, "E1406", {"start": v(3.58, 47.5) * mm, "end": v(3.62, 47.51) * mm});
            skLineSegment(sketch, "E1407", {"start": v(3.62, 47.51) * mm, "end": v(3.7, 47.54) * mm});
            skLineSegment(sketch, "E1408", {"start": v(3.7, 47.54) * mm, "end": v(3.8, 47.59) * mm});
            skLineSegment(sketch, "E1409", {"start": v(3.8, 47.59) * mm, "end": v(3.89, 47.66) * mm});
            skLineSegment(sketch, "E1410", {"start": v(3.89, 47.66) * mm, "end": v(3.93, 47.69) * mm});
            skLineSegment(sketch, "E1411", {"start": v(3.93, 47.69) * mm, "end": v(5.3, 49.06) * mm});
            skLineSegment(sketch, "E1412", {"start": v(5.3, 49.06) * mm, "end": v(5.35, 49.11) * mm});
            skLineSegment(sketch, "E1413", {"start": v(5.35, 49.11) * mm, "end": v(5.42, 49.22) * mm});
            skLineSegment(sketch, "E1414", {"start": v(5.42, 49.22) * mm, "end": v(5.44, 49.27) * mm});
            skLineSegment(sketch, "E1415", {"start": v(5.44, 49.27) * mm, "end": v(5.46, 49.32) * mm});
            skLineSegment(sketch, "E1416", {"start": v(5.46, 49.32) * mm, "end": v(5.48, 49.37) * mm});
            skLineSegment(sketch, "E1417", {"start": v(5.48, 49.37) * mm, "end": v(5.49, 49.41) * mm});
            skLineSegment(sketch, "E1418", {"start": v(5.49, 49.41) * mm, "end": v(5.49, 49.46) * mm});
            skLineSegment(sketch, "E1419", {"start": v(5.49, 49.46) * mm, "end": v(5.48, 49.5) * mm});
            skLineSegment(sketch, "E1420", {"start": v(5.48, 49.5) * mm, "end": v(5.47, 49.54) * mm});
            skLineSegment(sketch, "E1421", {"start": v(5.47, 49.54) * mm, "end": v(5.45, 49.59) * mm});
            skLineSegment(sketch, "E1422", {"start": v(5.45, 49.59) * mm, "end": v(5.43, 49.63) * mm});
            skLineSegment(sketch, "E1423", {"start": v(5.43, 49.63) * mm, "end": v(5.4, 49.67) * mm});
            skLineSegment(sketch, "E1424", {"start": v(5.4, 49.67) * mm, "end": v(5.36, 49.7) * mm});
            skLineSegment(sketch, "E1425", {"start": v(5.36, 49.7) * mm, "end": v(5.32, 49.74) * mm});
            skLineSegment(sketch, "E1426", {"start": v(5.32, 49.74) * mm, "end": v(5.28, 49.76) * mm});
            skLineSegment(sketch, "E1427", {"start": v(5.28, 49.76) * mm, "end": v(5.23, 49.78) * mm});
            skLineSegment(sketch, "E1428", {"start": v(5.23, 49.78) * mm, "end": v(5.2, 49.79) * mm});
            skLineSegment(sketch, "E1429", {"start": v(5.2, 49.79) * mm, "end": v(5.16, 49.8) * mm});
            skLineSegment(sketch, "E1430", {"start": v(5.16, 49.8) * mm, "end": v(5.12, 49.79) * mm});
            skLineSegment(sketch, "E1431", {"start": v(5.12, 49.79) * mm, "end": v(5.07, 49.78) * mm});
            skLineSegment(sketch, "E1432", {"start": v(5.07, 49.78) * mm, "end": v(5.02, 49.77) * mm});
            skLineSegment(sketch, "E1433", {"start": v(5.02, 49.77) * mm, "end": v(4.92, 49.74) * mm});
            skLineSegment(sketch, "E1434", {"start": v(4.92, 49.74) * mm, "end": v(4.74, 49.69) * mm});
            skLineSegment(sketch, "E1435", {"start": v(4.74, 49.69) * mm, "end": v(4.67, 49.67) * mm});
            skLineSegment(sketch, "E1436", {"start": v(4.67, 49.67) * mm, "end": v(4.6, 49.66) * mm});
            skLineSegment(sketch, "E1437", {"start": v(4.6, 49.66) * mm, "end": v(4.52, 49.66) * mm});
            skLineSegment(sketch, "E1438", {"start": v(4.52, 49.66) * mm, "end": v(4.45, 49.66) * mm});
            skLineSegment(sketch, "E1439", {"start": v(4.45, 49.66) * mm, "end": v(4.38, 49.67) * mm});
            skLineSegment(sketch, "E1440", {"start": v(4.38, 49.67) * mm, "end": v(4.3, 49.68) * mm});
            skLineSegment(sketch, "E1441", {"start": v(4.3, 49.68) * mm, "end": v(4.2, 49.7) * mm});
            skLineSegment(sketch, "E1442", {"start": v(4.2, 49.7) * mm, "end": v(4.1, 49.74) * mm});
            skLineSegment(sketch, "E1443", {"start": v(4.1, 49.74) * mm, "end": v(4, 49.78) * mm});
            skLineSegment(sketch, "E1444", {"start": v(4, 49.78) * mm, "end": v(3.9, 49.83) * mm});
            skLineSegment(sketch, "E1445", {"start": v(3.9, 49.83) * mm, "end": v(3.79, 49.88) * mm});
            skLineSegment(sketch, "E1446", {"start": v(3.79, 49.88) * mm, "end": v(3.68, 49.95) * mm});
            skLineSegment(sketch, "E1447", {"start": v(3.68, 49.95) * mm, "end": v(3.57, 50.02) * mm});
            skLineSegment(sketch, "E1448", {"start": v(3.57, 50.02) * mm, "end": v(3.45, 50.1) * mm});
            skLineSegment(sketch, "E1449", {"start": v(3.45, 50.1) * mm, "end": v(3.4, 50.15) * mm});
            skLineSegment(sketch, "E1450", {"start": v(3.4, 50.15) * mm, "end": v(1.74, 51.8) * mm});
            skLineSegment(sketch, "E1451", {"start": v(1.74, 51.8) * mm, "end": v(1.03, 52.16) * mm});
            skLineSegment(sketch, "E1452", {"start": v(1.03, 52.16) * mm, "end": v(0.54, 52.4) * mm});
            skLineSegment(sketch, "E1453", {"start": v(0.54, 52.4) * mm, "end": v(-0.1, 52.71) * mm});
            skLineSegment(sketch, "E1454", {"start": v(-0.1, 52.71) * mm, "end": v(-0.37, 52.85) * mm});
            skLineSegment(sketch, "E1455", {"start": v(-0.37, 52.85) * mm, "end": v(-0.38, 52.83) * mm});
            skLineSegment(sketch, "E1456", {"start": v(-0.38, 52.83) * mm, "end": v(2.84, 49.6) * mm});
            skLineSegment(sketch, "E1457", {"start": v(2.84, 49.6) * mm, "end": v(2.9, 49.53) * mm});
            skLineSegment(sketch, "E1458", {"start": v(2.9, 49.53) * mm, "end": v(2.99, 49.4) * mm});
            skLineSegment(sketch, "E1459", {"start": v(2.99, 49.4) * mm, "end": v(3.03, 49.33) * mm});
            skLineSegment(sketch, "E1460", {"start": v(3.03, 49.33) * mm, "end": v(3.03, 49.33) * mm});
            skLineSegment(sketch, "E1461", {"start": v(3.03, 49.33) * mm, "end": v(3.05, 49.3) * mm});
            skLineSegment(sketch, "E1462", {"start": v(3.05, 49.3) * mm, "end": v(3.07, 49.27) * mm});
            skLineSegment(sketch, "E1463", {"start": v(3.07, 49.27) * mm, "end": v(3.12, 49.19) * mm});
            skLineSegment(sketch, "E1464", {"start": v(3.12, 49.19) * mm, "end": v(3.2, 49.01) * mm});
            skLineSegment(sketch, "E1465", {"start": v(3.2, 49.01) * mm, "end": v(3.24, 48.93) * mm});
            skLineSegment(sketch, "E1466", {"start": v(3.24, 48.93) * mm, "end": v(3.27, 48.85) * mm});
            skLineSegment(sketch, "E1467", {"start": v(3.27, 48.85) * mm, "end": v(3.3, 48.77) * mm});
            skLineSegment(sketch, "E1468", {"start": v(3.3, 48.77) * mm, "end": v(3.31, 48.69) * mm});
            skLineSegment(sketch, "E1469", {"start": v(3.31, 48.69) * mm, "end": v(3.33, 48.61) * mm});
            skLineSegment(sketch, "E1470", {"start": v(3.33, 48.61) * mm, "end": v(3.33, 48.53) * mm});
            skLineSegment(sketch, "E1471", {"start": v(3.33, 48.53) * mm, "end": v(3.33, 48.43) * mm});
            skLineSegment(sketch, "E1472", {"start": v(3.33, 48.43) * mm, "end": v(3.32, 48.33) * mm});
            skLineSegment(sketch, "E1473", {"start": v(3.32, 48.33) * mm, "end": v(3.3, 48.2) * mm});
            skLineSegment(sketch, "E1474", {"start": v(3.3, 48.2) * mm, "end": v(3.25, 48.06) * mm});
            skLineSegment(sketch, "E1475", {"start": v(3.25, 48.06) * mm, "end": v(3.22, 47.95) * mm});
            skLineSegment(sketch, "E1476", {"start": v(3.22, 47.95) * mm, "end": v(3.2, 47.9) * mm});
            skLineSegment(sketch, "E1477", {"start": v(3.2, 47.9) * mm, "end": v(3.2, 47.87) * mm});
            skLineSegment(sketch, "E1478", {"start": v(3.2, 47.87) * mm, "end": v(3.2, 47.81) * mm});
            skLineSegment(sketch, "E1479", {"start": v(3.2, 47.81) * mm, "end": v(3.21, 47.76) * mm});
            skLineSegment(sketch, "E1480", {"start": v(3.21, 47.76) * mm, "end": v(3.23, 47.71) * mm});
            skLineSegment(sketch, "E1481", {"start": v(3.23, 47.71) * mm, "end": v(3.26, 47.67) * mm});
            skLineSegment(sketch, "E1482", {"start": v(3.26, 47.67) * mm, "end": v(3.3, 47.62) * mm});
            skLineSegment(sketch, "E1483", {"start": v(3.3, 47.62) * mm, "end": v(3.35, 47.58) * mm});
            skLineSegment(sketch, "E1484", {"start": v(3.35, 47.58) * mm, "end": v(3.39, 47.55) * mm});
            skLineSegment(sketch, "E1485", {"start": v(3.39, 47.55) * mm, "end": v(3.42, 47.53) * mm});
            skLineSegment(sketch, "E1486", {"start": v(3.42, 47.53) * mm, "end": v(3.47, 47.52) * mm});
            skLineSegment(sketch, "E1487", {"start": v(14.3, 53.62) * mm, "end": v(14.35, 53.61) * mm});
            skLineSegment(sketch, "E1488", {"start": v(14.35, 53.61) * mm, "end": v(14.4, 53.61) * mm});
            skLineSegment(sketch, "E1489", {"start": v(14.4, 53.61) * mm, "end": v(14.44, 53.62) * mm});
            skLineSegment(sketch, "E1490", {"start": v(14.44, 53.62) * mm, "end": v(14.47, 53.63) * mm});
            skLineSegment(sketch, "E1491", {"start": v(14.47, 53.63) * mm, "end": v(14.5, 53.65) * mm});
            skLineSegment(sketch, "E1492", {"start": v(14.5, 53.65) * mm, "end": v(14.54, 53.68) * mm});
            skLineSegment(sketch, "E1493", {"start": v(14.54, 53.68) * mm, "end": v(14.57, 53.71) * mm});
            skLineSegment(sketch, "E1494", {"start": v(14.57, 53.71) * mm, "end": v(14.6, 53.74) * mm});
            skLineSegment(sketch, "E1495", {"start": v(14.6, 53.74) * mm, "end": v(14.61, 53.78) * mm});
            skLineSegment(sketch, "E1496", {"start": v(14.61, 53.78) * mm, "end": v(14.62, 53.81) * mm});
            skLineSegment(sketch, "E1497", {"start": v(14.62, 53.81) * mm, "end": v(14.63, 53.85) * mm});
            skLineSegment(sketch, "E1498", {"start": v(14.63, 53.85) * mm, "end": v(14.63, 53.89) * mm});
            skLineSegment(sketch, "E1499", {"start": v(14.63, 53.89) * mm, "end": v(14.62, 53.92) * mm});
            skLineSegment(sketch, "E1500", {"start": v(14.62, 53.92) * mm, "end": v(14.6, 53.96) * mm});
            skLineSegment(sketch, "E1501", {"start": v(14.6, 53.96) * mm, "end": v(14.59, 54) * mm});
            skLineSegment(sketch, "E1502", {"start": v(14.59, 54) * mm, "end": v(13.32, 55.26) * mm});
            skLineSegment(sketch, "E1503", {"start": v(13.32, 55.26) * mm, "end": v(12.55, 54.5) * mm});
            skLineSegment(sketch, "E1504", {"start": v(12.55, 54.5) * mm, "end": v(12.86, 54.18) * mm});
            skLineSegment(sketch, "E1505", {"start": v(12.86, 54.18) * mm, "end": v(12.94, 54.2) * mm});
            skLineSegment(sketch, "E1506", {"start": v(12.94, 54.2) * mm, "end": v(13.07, 54.2) * mm});
            skLineSegment(sketch, "E1507", {"start": v(13.07, 54.2) * mm, "end": v(13.2, 54.18) * mm});
            skLineSegment(sketch, "E1508", {"start": v(13.2, 54.18) * mm, "end": v(13.33, 54.15) * mm});
            skLineSegment(sketch, "E1509", {"start": v(13.33, 54.15) * mm, "end": v(13.48, 54.1) * mm});
            skLineSegment(sketch, "E1510", {"start": v(13.48, 54.1) * mm, "end": v(13.52, 54.1) * mm});
            skLineSegment(sketch, "E1511", {"start": v(13.52, 54.1) * mm, "end": v(13.6, 54.05) * mm});
            skLineSegment(sketch, "E1512", {"start": v(13.6, 54.05) * mm, "end": v(13.75, 53.97) * mm});
            skLineSegment(sketch, "E1513", {"start": v(13.75, 53.97) * mm, "end": v(13.8, 53.94) * mm});
            skLineSegment(sketch, "E1514", {"start": v(13.8, 53.94) * mm, "end": v(13.81, 53.95) * mm});
            skLineSegment(sketch, "E1515", {"start": v(13.81, 53.95) * mm, "end": v(13.81, 53.95) * mm});
            skLineSegment(sketch, "E1516", {"start": v(13.81, 53.95) * mm, "end": v(13.81, 53.94) * mm});
            skLineSegment(sketch, "E1517", {"start": v(13.81, 53.94) * mm, "end": v(13.81, 53.94) * mm});
            skLineSegment(sketch, "E1518", {"start": v(13.81, 53.94) * mm, "end": v(13.82, 53.93) * mm});
            skLineSegment(sketch, "E1519", {"start": v(13.82, 53.93) * mm, "end": v(13.83, 53.93) * mm});
            skLineSegment(sketch, "E1520", {"start": v(13.83, 53.93) * mm, "end": v(13.9, 53.88) * mm});
            skLineSegment(sketch, "E1521", {"start": v(13.9, 53.88) * mm, "end": v(14.09, 53.75) * mm});
            skLineSegment(sketch, "E1522", {"start": v(14.09, 53.75) * mm, "end": v(14.19, 53.68) * mm});
            skLineSegment(sketch, "E1523", {"start": v(14.19, 53.68) * mm, "end": v(14.23, 53.66) * mm});
            skLineSegment(sketch, "E1524", {"start": v(14.23, 53.66) * mm, "end": v(14.3, 53.62) * mm});
            skLineSegment(sketch, "E1525", {"start": v(-8.87, 50.86) * mm, "end": v(-8.83, 50.86) * mm});
            skLineSegment(sketch, "E1526", {"start": v(-8.83, 50.86) * mm, "end": v(-8.8, 50.86) * mm});
            skLineSegment(sketch, "E1527", {"start": v(-8.8, 50.86) * mm, "end": v(-8.77, 50.87) * mm});
            skLineSegment(sketch, "E1528", {"start": v(-8.77, 50.87) * mm, "end": v(-8.73, 50.89) * mm});
            skLineSegment(sketch, "E1529", {"start": v(-8.73, 50.89) * mm, "end": v(-8.7, 50.9) * mm});
            skLineSegment(sketch, "E1530", {"start": v(-8.7, 50.9) * mm, "end": v(-8.65, 50.93) * mm});
            skLineSegment(sketch, "E1531", {"start": v(-8.65, 50.93) * mm, "end": v(-7.18, 52.4) * mm});
            skLineSegment(sketch, "E1532", {"start": v(-7.18, 52.4) * mm, "end": v(-7.17, 52.42) * mm});
            skLineSegment(sketch, "E1533", {"start": v(-7.17, 52.42) * mm, "end": v(-7.13, 52.48) * mm});
            skLineSegment(sketch, "E1534", {"start": v(-7.13, 52.48) * mm, "end": v(-7.12, 52.52) * mm});
            skLineSegment(sketch, "E1535", {"start": v(-7.12, 52.52) * mm, "end": v(-7.11, 52.58) * mm});
            skLineSegment(sketch, "E1536", {"start": v(-7.11, 52.58) * mm, "end": v(-7.11, 52.62) * mm});
            skLineSegment(sketch, "E1537", {"start": v(-7.11, 52.62) * mm, "end": v(-7.12, 52.66) * mm});
            skLineSegment(sketch, "E1538", {"start": v(-7.12, 52.66) * mm, "end": v(-7.14, 52.69) * mm});
            skLineSegment(sketch, "E1539", {"start": v(-7.14, 52.69) * mm, "end": v(-7.17, 52.72) * mm});
            skLineSegment(sketch, "E1540", {"start": v(-7.17, 52.72) * mm, "end": v(-7.2, 52.74) * mm});
            skLineSegment(sketch, "E1541", {"start": v(-7.2, 52.74) * mm, "end": v(-7.22, 52.76) * mm});
            skLineSegment(sketch, "E1542", {"start": v(-7.22, 52.76) * mm, "end": v(-7.25, 52.77) * mm});
            skLineSegment(sketch, "E1543", {"start": v(-7.25, 52.77) * mm, "end": v(-7.28, 52.78) * mm});
            skLineSegment(sketch, "E1544", {"start": v(-7.28, 52.78) * mm, "end": v(-7.32, 52.78) * mm});
            skLineSegment(sketch, "E1545", {"start": v(-7.32, 52.78) * mm, "end": v(-7.35, 52.77) * mm});
            skLineSegment(sketch, "E1546", {"start": v(-7.35, 52.77) * mm, "end": v(-7.39, 52.76) * mm});
            skLineSegment(sketch, "E1547", {"start": v(-7.39, 52.76) * mm, "end": v(-7.43, 52.74) * mm});
            skLineSegment(sketch, "E1548", {"start": v(-7.43, 52.74) * mm, "end": v(-7.52, 52.7) * mm});
            skLineSegment(sketch, "E1549", {"start": v(-7.52, 52.7) * mm, "end": v(-7.58, 52.68) * mm});
            skLineSegment(sketch, "E1550", {"start": v(-7.58, 52.68) * mm, "end": v(-7.61, 52.68) * mm});
            skLineSegment(sketch, "E1551", {"start": v(-7.61, 52.68) * mm, "end": v(-7.64, 52.68) * mm});
            skLineSegment(sketch, "E1552", {"start": v(-7.64, 52.68) * mm, "end": v(-7.69, 52.7) * mm});
            skLineSegment(sketch, "E1553", {"start": v(-7.69, 52.7) * mm, "end": v(-7.73, 52.72) * mm});
            skLineSegment(sketch, "E1554", {"start": v(-7.73, 52.72) * mm, "end": v(-11.07, 56.06) * mm});
            skLineSegment(sketch, "E1555", {"start": v(-11.07, 56.06) * mm, "end": v(-12.3, 54.83) * mm});
            skLineSegment(sketch, "E1556", {"start": v(-12.3, 54.83) * mm, "end": v(-8.97, 51.48) * mm});
            skLineSegment(sketch, "E1557", {"start": v(-8.97, 51.48) * mm, "end": v(-8.94, 51.44) * mm});
            skLineSegment(sketch, "E1558", {"start": v(-8.94, 51.44) * mm, "end": v(-8.93, 51.4) * mm});
            skLineSegment(sketch, "E1559", {"start": v(-8.93, 51.4) * mm, "end": v(-8.92, 51.37) * mm});
            skLineSegment(sketch, "E1560", {"start": v(-8.92, 51.37) * mm, "end": v(-8.93, 51.34) * mm});
            skLineSegment(sketch, "E1561", {"start": v(-8.93, 51.34) * mm, "end": v(-8.93, 51.3) * mm});
            skLineSegment(sketch, "E1562", {"start": v(-8.93, 51.3) * mm, "end": v(-8.94, 51.27) * mm});
            skLineSegment(sketch, "E1563", {"start": v(-8.94, 51.27) * mm, "end": v(-8.98, 51.2) * mm});
            skLineSegment(sketch, "E1564", {"start": v(-8.98, 51.2) * mm, "end": v(-9.02, 51.11) * mm});
            skLineSegment(sketch, "E1565", {"start": v(-9.02, 51.11) * mm, "end": v(-9.02, 51.05) * mm});
            skLineSegment(sketch, "E1566", {"start": v(-9.02, 51.05) * mm, "end": v(-9.02, 51) * mm});
            skLineSegment(sketch, "E1567", {"start": v(-9.02, 51) * mm, "end": v(-9, 50.97) * mm});
            skLineSegment(sketch, "E1568", {"start": v(-9, 50.97) * mm, "end": v(-8.98, 50.93) * mm});
            skLineSegment(sketch, "E1569", {"start": v(-8.98, 50.93) * mm, "end": v(-8.95, 50.9) * mm});
            skLineSegment(sketch, "E1570", {"start": v(-8.95, 50.9) * mm, "end": v(-8.9, 50.88) * mm});
            skLineSegment(sketch, "E1571", {"start": v(-8.9, 50.88) * mm, "end": v(-8.87, 50.86) * mm});
            skLineSegment(sketch, "E1572", {"start": v(-4.37, 55.42) * mm, "end": v(-4.33, 55.4) * mm});
            skLineSegment(sketch, "E1573", {"start": v(-4.33, 55.4) * mm, "end": v(-4.28, 55.4) * mm});
            skLineSegment(sketch, "E1574", {"start": v(-4.28, 55.4) * mm, "end": v(-4.23, 55.4) * mm});
            skLineSegment(sketch, "E1575", {"start": v(-4.23, 55.4) * mm, "end": v(-4.18, 55.43) * mm});
            skLineSegment(sketch, "E1576", {"start": v(-4.18, 55.43) * mm, "end": v(-4.14, 55.45) * mm});
            skLineSegment(sketch, "E1577", {"start": v(-4.14, 55.45) * mm, "end": v(-2.62, 56.96) * mm});
            skLineSegment(sketch, "E1578", {"start": v(-2.62, 56.96) * mm, "end": v(-2.6, 57) * mm});
            skLineSegment(sketch, "E1579", {"start": v(-2.6, 57) * mm, "end": v(-2.58, 57.06) * mm});
            skLineSegment(sketch, "E1580", {"start": v(-2.58, 57.06) * mm, "end": v(-2.57, 57.1) * mm});
            skLineSegment(sketch, "E1581", {"start": v(-2.57, 57.1) * mm, "end": v(-2.58, 57.15) * mm});
            skLineSegment(sketch, "E1582", {"start": v(-2.58, 57.15) * mm, "end": v(-2.59, 57.2) * mm});
            skLineSegment(sketch, "E1583", {"start": v(-2.59, 57.2) * mm, "end": v(-2.6, 57.23) * mm});
            skLineSegment(sketch, "E1584", {"start": v(-2.6, 57.23) * mm, "end": v(-2.64, 57.26) * mm});
            skLineSegment(sketch, "E1585", {"start": v(-2.64, 57.26) * mm, "end": v(-2.67, 57.29) * mm});
            skLineSegment(sketch, "E1586", {"start": v(-2.67, 57.29) * mm, "end": v(-2.7, 57.3) * mm});
            skLineSegment(sketch, "E1587", {"start": v(-2.7, 57.3) * mm, "end": v(-2.75, 57.31) * mm});
            skLineSegment(sketch, "E1588", {"start": v(-2.75, 57.31) * mm, "end": v(-2.8, 57.31) * mm});
            skLineSegment(sketch, "E1589", {"start": v(-2.8, 57.31) * mm, "end": v(-2.84, 57.3) * mm});
            skLineSegment(sketch, "E1590", {"start": v(-2.84, 57.3) * mm, "end": v(-2.9, 57.27) * mm});
            skLineSegment(sketch, "E1591", {"start": v(-2.9, 57.27) * mm, "end": v(-2.98, 57.23) * mm});
            skLineSegment(sketch, "E1592", {"start": v(-2.98, 57.23) * mm, "end": v(-3.05, 57.22) * mm});
            skLineSegment(sketch, "E1593", {"start": v(-3.05, 57.22) * mm, "end": v(-3.08, 57.21) * mm});
            skLineSegment(sketch, "E1594", {"start": v(-3.08, 57.21) * mm, "end": v(-3.1, 57.22) * mm});
            skLineSegment(sketch, "E1595", {"start": v(-3.1, 57.22) * mm, "end": v(-3.16, 57.24) * mm});
            skLineSegment(sketch, "E1596", {"start": v(-3.16, 57.24) * mm, "end": v(-3.2, 57.26) * mm});
            skLineSegment(sketch, "E1597", {"start": v(-3.2, 57.26) * mm, "end": v(-6.1, 60.16) * mm});
            skLineSegment(sketch, "E1598", {"start": v(-6.1, 60.16) * mm, "end": v(-6.12, 60.2) * mm});
            skLineSegment(sketch, "E1599", {"start": v(-6.12, 60.2) * mm, "end": v(-6.14, 60.24) * mm});
            skLineSegment(sketch, "E1600", {"start": v(-6.14, 60.24) * mm, "end": v(-6.14, 60.27) * mm});
            skLineSegment(sketch, "E1601", {"start": v(-6.14, 60.27) * mm, "end": v(-6.14, 60.3) * mm});
            skLineSegment(sketch, "E1602", {"start": v(-6.14, 60.3) * mm, "end": v(-6.13, 60.34) * mm});
            skLineSegment(sketch, "E1603", {"start": v(-6.13, 60.34) * mm, "end": v(-6.13, 60.37) * mm});
            skLineSegment(sketch, "E1604", {"start": v(-6.13, 60.37) * mm, "end": v(-6.09, 60.45) * mm});
            skLineSegment(sketch, "E1605", {"start": v(-6.09, 60.45) * mm, "end": v(-6.05, 60.53) * mm});
            skLineSegment(sketch, "E1606", {"start": v(-6.05, 60.53) * mm, "end": v(-6.04, 60.58) * mm});
            skLineSegment(sketch, "E1607", {"start": v(-6.04, 60.58) * mm, "end": v(-6.05, 60.63) * mm});
            skLineSegment(sketch, "E1608", {"start": v(-6.05, 60.63) * mm, "end": v(-6.07, 60.68) * mm});
            skLineSegment(sketch, "E1609", {"start": v(-6.07, 60.68) * mm, "end": v(-6.1, 60.73) * mm});
            skLineSegment(sketch, "E1610", {"start": v(-6.1, 60.73) * mm, "end": v(-6.15, 60.76) * mm});
            skLineSegment(sketch, "E1611", {"start": v(-6.15, 60.76) * mm, "end": v(-6.19, 60.78) * mm});
            skLineSegment(sketch, "E1612", {"start": v(-6.19, 60.78) * mm, "end": v(-6.24, 60.78) * mm});
            skLineSegment(sketch, "E1613", {"start": v(-6.24, 60.78) * mm, "end": v(-6.3, 60.78) * mm});
            skLineSegment(sketch, "E1614", {"start": v(-6.3, 60.78) * mm, "end": v(-6.35, 60.75) * mm});
            skLineSegment(sketch, "E1615", {"start": v(-6.35, 60.75) * mm, "end": v(-6.4, 60.73) * mm});
            skLineSegment(sketch, "E1616", {"start": v(-6.4, 60.73) * mm, "end": v(-7.9, 59.23) * mm});
            skLineSegment(sketch, "E1617", {"start": v(-7.9, 59.23) * mm, "end": v(-7.93, 59.18) * mm});
            skLineSegment(sketch, "E1618", {"start": v(-7.93, 59.18) * mm, "end": v(-7.95, 59.13) * mm});
            skLineSegment(sketch, "E1619", {"start": v(-7.95, 59.13) * mm, "end": v(-7.96, 59.1) * mm});
            skLineSegment(sketch, "E1620", {"start": v(-7.96, 59.1) * mm, "end": v(-7.96, 59.06) * mm});
            skLineSegment(sketch, "E1621", {"start": v(-7.96, 59.06) * mm, "end": v(-7.96, 59.02) * mm});
            skLineSegment(sketch, "E1622", {"start": v(-7.96, 59.02) * mm, "end": v(-7.94, 58.99) * mm});
            skLineSegment(sketch, "E1623", {"start": v(-7.94, 58.99) * mm, "end": v(-7.92, 58.95) * mm});
            skLineSegment(sketch, "E1624", {"start": v(-7.92, 58.95) * mm, "end": v(-7.9, 58.92) * mm});
            skLineSegment(sketch, "E1625", {"start": v(-7.9, 58.92) * mm, "end": v(-7.86, 58.9) * mm});
            skLineSegment(sketch, "E1626", {"start": v(-7.86, 58.9) * mm, "end": v(-7.82, 58.87) * mm});
            skLineSegment(sketch, "E1627", {"start": v(-7.82, 58.87) * mm, "end": v(-7.77, 58.87) * mm});
            skLineSegment(sketch, "E1628", {"start": v(-7.77, 58.87) * mm, "end": v(-7.73, 58.87) * mm});
            skLineSegment(sketch, "E1629", {"start": v(-7.73, 58.87) * mm, "end": v(-7.7, 58.88) * mm});
            skLineSegment(sketch, "E1630", {"start": v(-7.7, 58.88) * mm, "end": v(-7.64, 58.9) * mm});
            skLineSegment(sketch, "E1631", {"start": v(-7.64, 58.9) * mm, "end": v(-7.54, 58.95) * mm});
            skLineSegment(sketch, "E1632", {"start": v(-7.54, 58.95) * mm, "end": v(-7.5, 58.96) * mm});
            skLineSegment(sketch, "E1633", {"start": v(-7.5, 58.96) * mm, "end": v(-7.46, 58.97) * mm});
            skLineSegment(sketch, "E1634", {"start": v(-7.46, 58.97) * mm, "end": v(-7.43, 58.97) * mm});
            skLineSegment(sketch, "E1635", {"start": v(-7.43, 58.97) * mm, "end": v(-7.4, 58.96) * mm});
            skLineSegment(sketch, "E1636", {"start": v(-7.4, 58.96) * mm, "end": v(-7.38, 58.95) * mm});
            skLineSegment(sketch, "E1637", {"start": v(-7.38, 58.95) * mm, "end": v(-7.35, 58.93) * mm});
            skLineSegment(sketch, "E1638", {"start": v(-7.35, 58.93) * mm, "end": v(-7.31, 58.9) * mm});
            skLineSegment(sketch, "E1639", {"start": v(-7.31, 58.9) * mm, "end": v(-6.09, 57.67) * mm});
            skLineSegment(sketch, "E1640", {"start": v(-6.09, 57.67) * mm, "end": v(-6.06, 57.65) * mm});
            skLineSegment(sketch, "E1641", {"start": v(-6.06, 57.65) * mm, "end": v(-6.5, 57.2) * mm});
            skLineSegment(sketch, "E1642", {"start": v(-6.5, 57.2) * mm, "end": v(-6.21, 56.91) * mm});
            skLineSegment(sketch, "E1643", {"start": v(-6.21, 56.91) * mm, "end": v(-5.77, 57.36) * mm});
            skLineSegment(sketch, "E1644", {"start": v(-5.77, 57.36) * mm, "end": v(-4.45, 56.04) * mm});
            skLineSegment(sketch, "E1645", {"start": v(-4.45, 56.04) * mm, "end": v(-4.43, 56.01) * mm});
            skLineSegment(sketch, "E1646", {"start": v(-4.43, 56.01) * mm, "end": v(-4.4, 55.95) * mm});
            skLineSegment(sketch, "E1647", {"start": v(-4.4, 55.95) * mm, "end": v(-4.39, 55.9) * mm});
            skLineSegment(sketch, "E1648", {"start": v(-4.39, 55.9) * mm, "end": v(-4.4, 55.86) * mm});
            skLineSegment(sketch, "E1649", {"start": v(-4.4, 55.86) * mm, "end": v(-4.42, 55.8) * mm});
            skLineSegment(sketch, "E1650", {"start": v(-4.42, 55.8) * mm, "end": v(-4.45, 55.72) * mm});
            skLineSegment(sketch, "E1651", {"start": v(-4.45, 55.72) * mm, "end": v(-4.47, 55.67) * mm});
            skLineSegment(sketch, "E1652", {"start": v(-4.47, 55.67) * mm, "end": v(-4.48, 55.63) * mm});
            skLineSegment(sketch, "E1653", {"start": v(-4.48, 55.63) * mm, "end": v(-4.49, 55.6) * mm});
            skLineSegment(sketch, "E1654", {"start": v(-4.49, 55.6) * mm, "end": v(-4.49, 55.57) * mm});
            skLineSegment(sketch, "E1655", {"start": v(-4.49, 55.57) * mm, "end": v(-4.48, 55.52) * mm});
            skLineSegment(sketch, "E1656", {"start": v(-4.48, 55.52) * mm, "end": v(-4.45, 55.48) * mm});
            skLineSegment(sketch, "E1657", {"start": v(-4.45, 55.48) * mm, "end": v(-4.42, 55.44) * mm});
            skLineSegment(sketch, "E1658", {"start": v(-4.42, 55.44) * mm, "end": v(-4.37, 55.42) * mm});
            skLineSegment(sketch, "E1659", {"start": v(-9.18, 55.47) * mm, "end": v(-9.14, 55.46) * mm});
            skLineSegment(sketch, "E1660", {"start": v(-9.14, 55.46) * mm, "end": v(-9.1, 55.46) * mm});
            skLineSegment(sketch, "E1661", {"start": v(-9.1, 55.46) * mm, "end": v(-9.07, 55.47) * mm});
            skLineSegment(sketch, "E1662", {"start": v(-9.07, 55.47) * mm, "end": v(-9.03, 55.48) * mm});
            skLineSegment(sketch, "E1663", {"start": v(-9.03, 55.48) * mm, "end": v(-9, 55.5) * mm});
            skLineSegment(sketch, "E1664", {"start": v(-9, 55.5) * mm, "end": v(-8.96, 55.53) * mm});
            skLineSegment(sketch, "E1665", {"start": v(-8.96, 55.53) * mm, "end": v(-8.93, 55.57) * mm});
            skLineSegment(sketch, "E1666", {"start": v(-8.93, 55.57) * mm, "end": v(-8.9, 55.61) * mm});
            skLineSegment(sketch, "E1667", {"start": v(-8.9, 55.61) * mm, "end": v(-8.9, 55.65) * mm});
            skLineSegment(sketch, "E1668", {"start": v(-8.9, 55.65) * mm, "end": v(-8.89, 55.7) * mm});
            skLineSegment(sketch, "E1669", {"start": v(-8.89, 55.7) * mm, "end": v(-8.9, 55.74) * mm});
            skLineSegment(sketch, "E1670", {"start": v(-8.9, 55.74) * mm, "end": v(-8.9, 55.78) * mm});
            skLineSegment(sketch, "E1671", {"start": v(-8.9, 55.78) * mm, "end": v(-8.93, 55.83) * mm});
            skLineSegment(sketch, "E1672", {"start": v(-8.93, 55.83) * mm, "end": v(-10.12, 57.02) * mm});
            skLineSegment(sketch, "E1673", {"start": v(-10.12, 57.02) * mm, "end": v(-10.84, 56.3) * mm});
            skLineSegment(sketch, "E1674", {"start": v(-10.84, 56.3) * mm, "end": v(-10.55, 56) * mm});
            skLineSegment(sketch, "E1675", {"start": v(-10.55, 56) * mm, "end": v(-10.47, 56) * mm});
            skLineSegment(sketch, "E1676", {"start": v(-10.47, 56) * mm, "end": v(-10.4, 56.01) * mm});
            skLineSegment(sketch, "E1677", {"start": v(-10.4, 56.01) * mm, "end": v(-10.34, 56.01) * mm});
            skLineSegment(sketch, "E1678", {"start": v(-10.34, 56.01) * mm, "end": v(-10.27, 56) * mm});
            skLineSegment(sketch, "E1679", {"start": v(-10.27, 56) * mm, "end": v(-10.2, 56) * mm});
            skLineSegment(sketch, "E1680", {"start": v(-10.2, 56) * mm, "end": v(-10.12, 55.97) * mm});
            skLineSegment(sketch, "E1681", {"start": v(-10.12, 55.97) * mm, "end": v(-10.04, 55.95) * mm});
            skLineSegment(sketch, "E1682", {"start": v(-10.04, 55.95) * mm, "end": v(-9.97, 55.93) * mm});
            skLineSegment(sketch, "E1683", {"start": v(-9.97, 55.93) * mm, "end": v(-9.89, 55.9) * mm});
            skLineSegment(sketch, "E1684", {"start": v(-9.89, 55.9) * mm, "end": v(-9.78, 55.84) * mm});
            skLineSegment(sketch, "E1685", {"start": v(-9.78, 55.84) * mm, "end": v(-9.66, 55.77) * mm});
            skLineSegment(sketch, "E1686", {"start": v(-9.66, 55.77) * mm, "end": v(-9.53, 55.69) * mm});
            skLineSegment(sketch, "E1687", {"start": v(-9.53, 55.69) * mm, "end": v(-9.38, 55.59) * mm});
            skLineSegment(sketch, "E1688", {"start": v(-9.38, 55.59) * mm, "end": v(-9.28, 55.52) * mm});
            skLineSegment(sketch, "E1689", {"start": v(-9.28, 55.52) * mm, "end": v(-9.24, 55.5) * mm});
            skLineSegment(sketch, "E1690", {"start": v(-9.24, 55.5) * mm, "end": v(-9.18, 55.47) * mm});
            skLineSegment(sketch, "E1691", {"start": v(11.28, 56.55) * mm, "end": v(11.27, 56.55) * mm});
            skLineSegment(sketch, "E1692", {"start": v(11.27, 56.55) * mm, "end": v(11.27, 56.55) * mm});
            skLineSegment(sketch, "E1693", {"start": v(11.27, 56.55) * mm, "end": v(11.28, 56.55) * mm});
            skLineSegment(sketch, "E1694", {"start": v(11.14, 56.71) * mm, "end": v(11.14, 56.72) * mm});
            skLineSegment(sketch, "E1695", {"start": v(11.14, 56.72) * mm, "end": v(11.14, 56.71) * mm});
            skLineSegment(sketch, "E1696", {"start": v(11.14, 56.71) * mm, "end": v(11.14, 56.7) * mm});
            skLineSegment(sketch, "E1697", {"start": v(11.14, 56.7) * mm, "end": v(11.14, 56.71) * mm});
            skLineSegment(sketch, "E1698", {"start": v(-6.28, 53.5) * mm, "end": v(-6.24, 53.5) * mm});
            skLineSegment(sketch, "E1699", {"start": v(-6.24, 53.5) * mm, "end": v(-6.2, 53.5) * mm});
            skLineSegment(sketch, "E1700", {"start": v(-6.2, 53.5) * mm, "end": v(-6.14, 53.5) * mm});
            skLineSegment(sketch, "E1701", {"start": v(-6.14, 53.5) * mm, "end": v(-6.1, 53.52) * mm});
            skLineSegment(sketch, "E1702", {"start": v(-6.1, 53.52) * mm, "end": v(-6.05, 53.54) * mm});
            skLineSegment(sketch, "E1703", {"start": v(-6.05, 53.54) * mm, "end": v(-4.53, 55.05) * mm});
            skLineSegment(sketch, "E1704", {"start": v(-4.53, 55.05) * mm, "end": v(-4.5, 55.1) * mm});
            skLineSegment(sketch, "E1705", {"start": v(-4.5, 55.1) * mm, "end": v(-4.5, 55.15) * mm});
            skLineSegment(sketch, "E1706", {"start": v(-4.5, 55.15) * mm, "end": v(-4.48, 55.2) * mm});
            skLineSegment(sketch, "E1707", {"start": v(-4.48, 55.2) * mm, "end": v(-4.49, 55.24) * mm});
            skLineSegment(sketch, "E1708", {"start": v(-4.49, 55.24) * mm, "end": v(-4.5, 55.29) * mm});
            skLineSegment(sketch, "E1709", {"start": v(-4.5, 55.29) * mm, "end": v(-4.52, 55.32) * mm});
            skLineSegment(sketch, "E1710", {"start": v(-4.52, 55.32) * mm, "end": v(-4.54, 55.34) * mm});
            skLineSegment(sketch, "E1711", {"start": v(-4.54, 55.34) * mm, "end": v(-4.56, 55.37) * mm});
            skLineSegment(sketch, "E1712", {"start": v(-4.56, 55.37) * mm, "end": v(-4.6, 55.38) * mm});
            skLineSegment(sketch, "E1713", {"start": v(-4.6, 55.38) * mm, "end": v(-4.62, 55.4) * mm});
            skLineSegment(sketch, "E1714", {"start": v(-4.62, 55.4) * mm, "end": v(-4.65, 55.4) * mm});
            skLineSegment(sketch, "E1715", {"start": v(-4.65, 55.4) * mm, "end": v(-4.68, 55.4) * mm});
            skLineSegment(sketch, "E1716", {"start": v(-4.68, 55.4) * mm, "end": v(-4.72, 55.4) * mm});
            skLineSegment(sketch, "E1717", {"start": v(-4.72, 55.4) * mm, "end": v(-4.75, 55.4) * mm});
            skLineSegment(sketch, "E1718", {"start": v(-4.75, 55.4) * mm, "end": v(-4.84, 55.35) * mm});
            skLineSegment(sketch, "E1719", {"start": v(-4.84, 55.35) * mm, "end": v(-4.92, 55.32) * mm});
            skLineSegment(sketch, "E1720", {"start": v(-4.92, 55.32) * mm, "end": v(-4.97, 55.3) * mm});
            skLineSegment(sketch, "E1721", {"start": v(-4.97, 55.3) * mm, "end": v(-5.02, 55.3) * mm});
            skLineSegment(sketch, "E1722", {"start": v(-5.02, 55.3) * mm, "end": v(-5.05, 55.32) * mm});
            skLineSegment(sketch, "E1723", {"start": v(-5.05, 55.32) * mm, "end": v(-5.09, 55.33) * mm});
            skLineSegment(sketch, "E1724", {"start": v(-5.09, 55.33) * mm, "end": v(-8.01, 58.26) * mm});
            skLineSegment(sketch, "E1725", {"start": v(-8.01, 58.26) * mm, "end": v(-8.03, 58.29) * mm});
            skLineSegment(sketch, "E1726", {"start": v(-8.03, 58.29) * mm, "end": v(-8.05, 58.36) * mm});
            skLineSegment(sketch, "E1727", {"start": v(-8.05, 58.36) * mm, "end": v(-8.06, 58.39) * mm});
            skLineSegment(sketch, "E1728", {"start": v(-8.06, 58.39) * mm, "end": v(-8.05, 58.4) * mm});
            skLineSegment(sketch, "E1729", {"start": v(-8.05, 58.4) * mm, "end": v(-8.04, 58.43) * mm});
            skLineSegment(sketch, "E1730", {"start": v(-8.04, 58.43) * mm, "end": v(-8.03, 58.47) * mm});
            skLineSegment(sketch, "E1731", {"start": v(-8.03, 58.47) * mm, "end": v(-8, 58.55) * mm});
            skLineSegment(sketch, "E1732", {"start": v(-8, 58.55) * mm, "end": v(-7.96, 58.62) * mm});
            skLineSegment(sketch, "E1733", {"start": v(-7.96, 58.62) * mm, "end": v(-7.96, 58.68) * mm});
            skLineSegment(sketch, "E1734", {"start": v(-7.96, 58.68) * mm, "end": v(-7.96, 58.73) * mm});
            skLineSegment(sketch, "E1735", {"start": v(-7.96, 58.73) * mm, "end": v(-7.97, 58.77) * mm});
            skLineSegment(sketch, "E1736", {"start": v(-7.97, 58.77) * mm, "end": v(-8, 58.8) * mm});
            skLineSegment(sketch, "E1737", {"start": v(-8, 58.8) * mm, "end": v(-8.04, 58.84) * mm});
            skLineSegment(sketch, "E1738", {"start": v(-8.04, 58.84) * mm, "end": v(-8.07, 58.86) * mm});
            skLineSegment(sketch, "E1739", {"start": v(-8.07, 58.86) * mm, "end": v(-8.11, 58.87) * mm});
            skLineSegment(sketch, "E1740", {"start": v(-8.11, 58.87) * mm, "end": v(-8.16, 58.87) * mm});
            skLineSegment(sketch, "E1741", {"start": v(-8.16, 58.87) * mm, "end": v(-8.2, 58.87) * mm});
            skLineSegment(sketch, "E1742", {"start": v(-8.2, 58.87) * mm, "end": v(-8.25, 58.85) * mm});
            skLineSegment(sketch, "E1743", {"start": v(-8.25, 58.85) * mm, "end": v(-8.3, 58.82) * mm});
            skLineSegment(sketch, "E1744", {"start": v(-8.3, 58.82) * mm, "end": v(-8.34, 58.8) * mm});
            skLineSegment(sketch, "E1745", {"start": v(-8.34, 58.8) * mm, "end": v(-9.81, 57.32) * mm});
            skLineSegment(sketch, "E1746", {"start": v(-9.81, 57.32) * mm, "end": v(-9.84, 57.27) * mm});
            skLineSegment(sketch, "E1747", {"start": v(-9.84, 57.27) * mm, "end": v(-9.86, 57.21) * mm});
            skLineSegment(sketch, "E1748", {"start": v(-9.86, 57.21) * mm, "end": v(-9.86, 57.15) * mm});
            skLineSegment(sketch, "E1749", {"start": v(-9.86, 57.15) * mm, "end": v(-9.86, 57.11) * mm});
            skLineSegment(sketch, "E1750", {"start": v(-9.86, 57.11) * mm, "end": v(-9.85, 57.08) * mm});
            skLineSegment(sketch, "E1751", {"start": v(-9.85, 57.08) * mm, "end": v(-9.84, 57.05) * mm});
            skLineSegment(sketch, "E1752", {"start": v(-9.84, 57.05) * mm, "end": v(-9.8, 57.02) * mm});
            skLineSegment(sketch, "E1753", {"start": v(-9.8, 57.02) * mm, "end": v(-9.78, 56.99) * mm});
            skLineSegment(sketch, "E1754", {"start": v(-9.78, 56.99) * mm, "end": v(-9.75, 56.97) * mm});
            skLineSegment(sketch, "E1755", {"start": v(-9.75, 56.97) * mm, "end": v(-9.72, 56.96) * mm});
            skLineSegment(sketch, "E1756", {"start": v(-9.72, 56.96) * mm, "end": v(-9.68, 56.96) * mm});
            skLineSegment(sketch, "E1757", {"start": v(-9.68, 56.96) * mm, "end": v(-9.64, 56.96) * mm});
            skLineSegment(sketch, "E1758", {"start": v(-9.64, 56.96) * mm, "end": v(-9.62, 56.97) * mm});
            skLineSegment(sketch, "E1759", {"start": v(-9.62, 56.97) * mm, "end": v(-9.54, 57) * mm});
            skLineSegment(sketch, "E1760", {"start": v(-9.54, 57) * mm, "end": v(-9.46, 57.04) * mm});
            skLineSegment(sketch, "E1761", {"start": v(-9.46, 57.04) * mm, "end": v(-9.42, 57.05) * mm});
            skLineSegment(sketch, "E1762", {"start": v(-9.42, 57.05) * mm, "end": v(-9.38, 57.06) * mm});
            skLineSegment(sketch, "E1763", {"start": v(-9.38, 57.06) * mm, "end": v(-9.35, 57.06) * mm});
            skLineSegment(sketch, "E1764", {"start": v(-9.35, 57.06) * mm, "end": v(-9.31, 57.05) * mm});
            skLineSegment(sketch, "E1765", {"start": v(-9.31, 57.05) * mm, "end": v(-9.28, 57.03) * mm});
            skLineSegment(sketch, "E1766", {"start": v(-9.28, 57.03) * mm, "end": v(-9.24, 57) * mm});
            skLineSegment(sketch, "E1767", {"start": v(-9.24, 57) * mm, "end": v(-6.33, 54.1) * mm});
            skLineSegment(sketch, "E1768", {"start": v(-6.33, 54.1) * mm, "end": v(-6.32, 54.07) * mm});
            skLineSegment(sketch, "E1769", {"start": v(-6.32, 54.07) * mm, "end": v(-6.3, 54.02) * mm});
            skLineSegment(sketch, "E1770", {"start": v(-6.3, 54.02) * mm, "end": v(-6.3, 54) * mm});
            skLineSegment(sketch, "E1771", {"start": v(-6.3, 54) * mm, "end": v(-6.3, 53.97) * mm});
            skLineSegment(sketch, "E1772", {"start": v(-6.3, 53.97) * mm, "end": v(-6.32, 53.9) * mm});
            skLineSegment(sketch, "E1773", {"start": v(-6.32, 53.9) * mm, "end": v(-6.36, 53.8) * mm});
            skLineSegment(sketch, "E1774", {"start": v(-6.36, 53.8) * mm, "end": v(-6.4, 53.73) * mm});
            skLineSegment(sketch, "E1775", {"start": v(-6.4, 53.73) * mm, "end": v(-6.4, 53.68) * mm});
            skLineSegment(sketch, "E1776", {"start": v(-6.4, 53.68) * mm, "end": v(-6.4, 53.63) * mm});
            skLineSegment(sketch, "E1777", {"start": v(-6.4, 53.63) * mm, "end": v(-6.37, 53.59) * mm});
            skLineSegment(sketch, "E1778", {"start": v(-6.37, 53.59) * mm, "end": v(-6.35, 53.56) * mm});
            skLineSegment(sketch, "E1779", {"start": v(-6.35, 53.56) * mm, "end": v(-6.33, 53.54) * mm});
            skLineSegment(sketch, "E1780", {"start": v(-6.33, 53.54) * mm, "end": v(-6.3, 53.52) * mm});
            skLineSegment(sketch, "E1781", {"start": v(-6.3, 53.52) * mm, "end": v(-6.28, 53.5) * mm});
            skLineSegment(sketch, "E1782", {"start": v(-0.91, 59.25) * mm, "end": v(-0.63, 58.96) * mm});
            skLineSegment(sketch, "E1783", {"start": v(-0.63, 58.96) * mm, "end": v(0.53, 60.12) * mm});
            skLineSegment(sketch, "E1784", {"start": v(0.53, 60.12) * mm, "end": v(-0.53, 61.18) * mm});
            skLineSegment(sketch, "E1785", {"start": v(-0.53, 61.18) * mm, "end": v(-0.57, 61.2) * mm});
            skLineSegment(sketch, "E1786", {"start": v(-0.57, 61.2) * mm, "end": v(-0.6, 61.21) * mm});
            skLineSegment(sketch, "E1787", {"start": v(-0.6, 61.21) * mm, "end": v(-0.63, 61.22) * mm});
            skLineSegment(sketch, "E1788", {"start": v(-0.63, 61.22) * mm, "end": v(-0.66, 61.22) * mm});
            skLineSegment(sketch, "E1789", {"start": v(-0.66, 61.22) * mm, "end": v(-0.69, 61.21) * mm});
            skLineSegment(sketch, "E1790", {"start": v(-0.69, 61.21) * mm, "end": v(-0.71, 61.2) * mm});
            skLineSegment(sketch, "E1791", {"start": v(-0.71, 61.2) * mm, "end": v(-0.74, 61.19) * mm});
            skLineSegment(sketch, "E1792", {"start": v(-0.74, 61.19) * mm, "end": v(-0.77, 61.17) * mm});
            skLineSegment(sketch, "E1793", {"start": v(-0.77, 61.17) * mm, "end": v(-0.8, 61.15) * mm});
            skLineSegment(sketch, "E1794", {"start": v(-0.8, 61.15) * mm, "end": v(-0.82, 61.1) * mm});
            skLineSegment(sketch, "E1795", {"start": v(-0.82, 61.1) * mm, "end": v(-0.84, 61.06) * mm});
            skLineSegment(sketch, "E1796", {"start": v(-0.84, 61.06) * mm, "end": v(-0.84, 61) * mm});
            skLineSegment(sketch, "E1797", {"start": v(-0.84, 61) * mm, "end": v(-0.82, 60.94) * mm});
            skLineSegment(sketch, "E1798", {"start": v(-0.82, 60.94) * mm, "end": v(-0.79, 60.83) * mm});
            skLineSegment(sketch, "E1799", {"start": v(-0.79, 60.83) * mm, "end": v(-0.72, 60.67) * mm});
            skLineSegment(sketch, "E1800", {"start": v(-0.72, 60.67) * mm, "end": v(-0.67, 60.52) * mm});
            skLineSegment(sketch, "E1801", {"start": v(-0.67, 60.52) * mm, "end": v(-0.64, 60.37) * mm});
            skLineSegment(sketch, "E1802", {"start": v(-0.64, 60.37) * mm, "end": v(-0.62, 60.21) * mm});
            skLineSegment(sketch, "E1803", {"start": v(-0.62, 60.21) * mm, "end": v(-0.61, 60.12) * mm});
            skLineSegment(sketch, "E1804", {"start": v(-0.61, 60.12) * mm, "end": v(-0.62, 60.03) * mm});
            skLineSegment(sketch, "E1805", {"start": v(-0.62, 60.03) * mm, "end": v(-0.63, 59.93) * mm});
            skLineSegment(sketch, "E1806", {"start": v(-0.63, 59.93) * mm, "end": v(-0.64, 59.84) * mm});
            skLineSegment(sketch, "E1807", {"start": v(-0.64, 59.84) * mm, "end": v(-0.66, 59.75) * mm});
            skLineSegment(sketch, "E1808", {"start": v(-0.66, 59.75) * mm, "end": v(-0.7, 59.66) * mm});
            skLineSegment(sketch, "E1809", {"start": v(-0.7, 59.66) * mm, "end": v(-0.73, 59.57) * mm});
            skLineSegment(sketch, "E1810", {"start": v(-0.73, 59.57) * mm, "end": v(-0.77, 59.48) * mm});
            skLineSegment(sketch, "E1811", {"start": v(-0.77, 59.48) * mm, "end": v(-0.8, 59.43) * mm});
            skLineSegment(sketch, "E1812", {"start": v(-0.8, 59.43) * mm, "end": v(-0.8, 59.42) * mm});
            skLineSegment(sketch, "E1813", {"start": v(-0.8, 59.42) * mm, "end": v(-0.8, 59.42) * mm});
            skLineSegment(sketch, "E1814", {"start": v(-0.8, 59.42) * mm, "end": v(-0.83, 59.37) * mm});
            skLineSegment(sketch, "E1815", {"start": v(-0.83, 59.37) * mm, "end": v(-0.88, 59.3) * mm});
            skLineSegment(sketch, "E1816", {"start": v(-0.88, 59.3) * mm, "end": v(-0.91, 59.25) * mm});
            skLineSegment(sketch, "E1817", {"start": v(-1.47, 60.59) * mm, "end": v(-1.42, 60.58) * mm});
            skLineSegment(sketch, "E1818", {"start": v(-1.42, 60.58) * mm, "end": v(-1.37, 60.58) * mm});
            skLineSegment(sketch, "E1819", {"start": v(-1.37, 60.58) * mm, "end": v(-1.32, 60.6) * mm});
            skLineSegment(sketch, "E1820", {"start": v(-1.32, 60.6) * mm, "end": v(-1.28, 60.64) * mm});
            skLineSegment(sketch, "E1821", {"start": v(-1.28, 60.64) * mm, "end": v(-1.24, 60.68) * mm});
            skLineSegment(sketch, "E1822", {"start": v(-1.24, 60.68) * mm, "end": v(-1.23, 60.72) * mm});
            skLineSegment(sketch, "E1823", {"start": v(-1.23, 60.72) * mm, "end": v(-1.22, 60.76) * mm});
            skLineSegment(sketch, "E1824", {"start": v(-1.22, 60.76) * mm, "end": v(-1.23, 60.8) * mm});
            skLineSegment(sketch, "E1825", {"start": v(-1.23, 60.8) * mm, "end": v(-1.24, 60.84) * mm});
            skLineSegment(sketch, "E1826", {"start": v(-1.24, 60.84) * mm, "end": v(-1.26, 60.88) * mm});
            skLineSegment(sketch, "E1827", {"start": v(-1.26, 60.88) * mm, "end": v(-2.56, 62.18) * mm});
            skLineSegment(sketch, "E1828", {"start": v(-2.56, 62.18) * mm, "end": v(-2.59, 62.2) * mm});
            skLineSegment(sketch, "E1829", {"start": v(-2.59, 62.2) * mm, "end": v(-2.63, 62.22) * mm});
            skLineSegment(sketch, "E1830", {"start": v(-2.63, 62.22) * mm, "end": v(-2.65, 62.22) * mm});
            skLineSegment(sketch, "E1831", {"start": v(-2.65, 62.22) * mm, "end": v(-2.66, 62.23) * mm});
            skLineSegment(sketch, "E1832", {"start": v(-2.66, 62.23) * mm, "end": v(-2.69, 62.23) * mm});
            skLineSegment(sketch, "E1833", {"start": v(-2.69, 62.23) * mm, "end": v(-2.74, 62.22) * mm});
            skLineSegment(sketch, "E1834", {"start": v(-2.74, 62.22) * mm, "end": v(-2.77, 62.2) * mm});
            skLineSegment(sketch, "E1835", {"start": v(-2.77, 62.2) * mm, "end": v(-2.8, 62.17) * mm});
            skLineSegment(sketch, "E1836", {"start": v(-2.8, 62.17) * mm, "end": v(-2.83, 62.14) * mm});
            skLineSegment(sketch, "E1837", {"start": v(-2.83, 62.14) * mm, "end": v(-2.85, 62.1) * mm});
            skLineSegment(sketch, "E1838", {"start": v(-2.85, 62.1) * mm, "end": v(-2.87, 62.06) * mm});
            skLineSegment(sketch, "E1839", {"start": v(-2.87, 62.06) * mm, "end": v(-2.87, 62.02) * mm});
            skLineSegment(sketch, "E1840", {"start": v(-2.87, 62.02) * mm, "end": v(-2.86, 61.96) * mm});
            skLineSegment(sketch, "E1841", {"start": v(-2.86, 61.96) * mm, "end": v(-2.84, 61.9) * mm});
            skLineSegment(sketch, "E1842", {"start": v(-2.84, 61.9) * mm, "end": v(-2.82, 61.87) * mm});
            skLineSegment(sketch, "E1843", {"start": v(-2.82, 61.87) * mm, "end": v(-2.77, 61.78) * mm});
            skLineSegment(sketch, "E1844", {"start": v(-2.77, 61.78) * mm, "end": v(-2.7, 61.66) * mm});
            skLineSegment(sketch, "E1845", {"start": v(-2.7, 61.66) * mm, "end": v(-2.67, 61.55) * mm});
            skLineSegment(sketch, "E1846", {"start": v(-2.67, 61.55) * mm, "end": v(-2.65, 61.45) * mm});
            skLineSegment(sketch, "E1847", {"start": v(-2.65, 61.45) * mm, "end": v(-2.64, 61.34) * mm});
            skLineSegment(sketch, "E1848", {"start": v(-2.64, 61.34) * mm, "end": v(-2.64, 61.27) * mm});
            skLineSegment(sketch, "E1849", {"start": v(-2.64, 61.27) * mm, "end": v(-2.65, 61.21) * mm});
            skLineSegment(sketch, "E1850", {"start": v(-2.65, 61.21) * mm, "end": v(-2.66, 61.16) * mm});
            skLineSegment(sketch, "E1851", {"start": v(-2.66, 61.16) * mm, "end": v(-2.69, 61.1) * mm});
            skLineSegment(sketch, "E1852", {"start": v(-2.69, 61.1) * mm, "end": v(-2.71, 61.04) * mm});
            skLineSegment(sketch, "E1853", {"start": v(-2.71, 61.04) * mm, "end": v(-2.4, 60.74) * mm});
            skLineSegment(sketch, "E1854", {"start": v(-2.4, 60.74) * mm, "end": v(-2.39, 60.74) * mm});
            skLineSegment(sketch, "E1855", {"start": v(-2.39, 60.74) * mm, "end": v(-2.33, 60.77) * mm});
            skLineSegment(sketch, "E1856", {"start": v(-2.33, 60.77) * mm, "end": v(-2.28, 60.79) * mm});
            skLineSegment(sketch, "E1857", {"start": v(-2.28, 60.79) * mm, "end": v(-2.23, 60.8) * mm});
            skLineSegment(sketch, "E1858", {"start": v(-2.23, 60.8) * mm, "end": v(-2.17, 60.8) * mm});
            skLineSegment(sketch, "E1859", {"start": v(-2.17, 60.8) * mm, "end": v(-2.12, 60.81) * mm});
            skLineSegment(sketch, "E1860", {"start": v(-2.12, 60.81) * mm, "end": v(-2.06, 60.8) * mm});
            skLineSegment(sketch, "E1861", {"start": v(-2.06, 60.8) * mm, "end": v(-2, 60.8) * mm});
            skLineSegment(sketch, "E1862", {"start": v(-2, 60.8) * mm, "end": v(-1.93, 60.79) * mm});
            skLineSegment(sketch, "E1863", {"start": v(-1.93, 60.79) * mm, "end": v(-1.87, 60.77) * mm});
            skLineSegment(sketch, "E1864", {"start": v(-1.87, 60.77) * mm, "end": v(-1.75, 60.72) * mm});
            skLineSegment(sketch, "E1865", {"start": v(-1.75, 60.72) * mm, "end": v(-1.58, 60.63) * mm});
            skLineSegment(sketch, "E1866", {"start": v(-1.58, 60.63) * mm, "end": v(-1.52, 60.6) * mm});
            skLineSegment(sketch, "E1867", {"start": v(-1.52, 60.6) * mm, "end": v(-1.47, 60.59) * mm});
            skLineSegment(sketch, "E1868", {"start": v(-2.4, 60.75) * mm, "end": v(-2.4, 60.76) * mm});
            skLineSegment(sketch, "E1869", {"start": v(-2.4, 60.76) * mm, "end": v(-2.4, 60.75) * mm});
            skLineSegment(sketch, "E1870", {"start": v(-2.4, 60.75) * mm, "end": v(-2.4, 60.75) * mm});
            skLineSegment(sketch, "E1871", {"start": v(13.2, 61.64) * mm, "end": v(13.25, 61.63) * mm});
            skLineSegment(sketch, "E1872", {"start": v(13.25, 61.63) * mm, "end": v(13.31, 61.63) * mm});
            skLineSegment(sketch, "E1873", {"start": v(13.31, 61.63) * mm, "end": v(13.37, 61.63) * mm});
            skLineSegment(sketch, "E1874", {"start": v(13.37, 61.63) * mm, "end": v(13.41, 61.64) * mm});
            skLineSegment(sketch, "E1875", {"start": v(13.41, 61.64) * mm, "end": v(13.46, 61.66) * mm});
            skLineSegment(sketch, "E1876", {"start": v(13.46, 61.66) * mm, "end": v(13.5, 61.68) * mm});
            skLineSegment(sketch, "E1877", {"start": v(13.5, 61.68) * mm, "end": v(13.54, 61.71) * mm});
            skLineSegment(sketch, "E1878", {"start": v(13.54, 61.71) * mm, "end": v(13.58, 61.75) * mm});
            skLineSegment(sketch, "E1879", {"start": v(13.58, 61.75) * mm, "end": v(13.61, 61.78) * mm});
            skLineSegment(sketch, "E1880", {"start": v(13.61, 61.78) * mm, "end": v(13.64, 61.82) * mm});
            skLineSegment(sketch, "E1881", {"start": v(13.64, 61.82) * mm, "end": v(13.66, 61.86) * mm});
            skLineSegment(sketch, "E1882", {"start": v(13.66, 61.86) * mm, "end": v(13.67, 61.9) * mm});
            skLineSegment(sketch, "E1883", {"start": v(13.67, 61.9) * mm, "end": v(13.68, 61.95) * mm});
            skLineSegment(sketch, "E1884", {"start": v(13.68, 61.95) * mm, "end": v(13.68, 62) * mm});
            skLineSegment(sketch, "E1885", {"start": v(13.68, 62) * mm, "end": v(13.66, 62.07) * mm});
            skLineSegment(sketch, "E1886", {"start": v(13.66, 62.07) * mm, "end": v(13.65, 62.1) * mm});
            skLineSegment(sketch, "E1887", {"start": v(13.65, 62.1) * mm, "end": v(13.64, 62.12) * mm});
            skLineSegment(sketch, "E1888", {"start": v(13.64, 62.12) * mm, "end": v(13.64, 62.12) * mm});
            skLineSegment(sketch, "E1889", {"start": v(13.64, 62.12) * mm, "end": v(13.64, 62.13) * mm});
            skLineSegment(sketch, "E1890", {"start": v(13.64, 62.13) * mm, "end": v(13.64, 62.13) * mm});
            skLineSegment(sketch, "E1891", {"start": v(13.64, 62.13) * mm, "end": v(13.58, 62.22) * mm});
            skLineSegment(sketch, "E1892", {"start": v(13.58, 62.22) * mm, "end": v(11.18, 64.62) * mm});
            skLineSegment(sketch, "E1893", {"start": v(11.18, 64.62) * mm, "end": v(11.15, 64.65) * mm});
            skLineSegment(sketch, "E1894", {"start": v(11.15, 64.65) * mm, "end": v(11.12, 64.67) * mm});
            skLineSegment(sketch, "E1895", {"start": v(11.12, 64.67) * mm, "end": v(11.1, 64.68) * mm});
            skLineSegment(sketch, "E1896", {"start": v(11.1, 64.68) * mm, "end": v(11.1, 64.68) * mm});
            skLineSegment(sketch, "E1897", {"start": v(11.1, 64.68) * mm, "end": v(11.05, 64.7) * mm});
            skLineSegment(sketch, "E1898", {"start": v(11.05, 64.7) * mm, "end": v(11.01, 64.73) * mm});
            skLineSegment(sketch, "E1899", {"start": v(11.01, 64.73) * mm, "end": v(10.97, 64.74) * mm});
            skLineSegment(sketch, "E1900", {"start": v(10.97, 64.74) * mm, "end": v(10.93, 64.75) * mm});
            skLineSegment(sketch, "E1901", {"start": v(10.93, 64.75) * mm, "end": v(10.9, 64.75) * mm});
            skLineSegment(sketch, "E1902", {"start": v(10.9, 64.75) * mm, "end": v(10.85, 64.75) * mm});
            skLineSegment(sketch, "E1903", {"start": v(10.85, 64.75) * mm, "end": v(10.82, 64.74) * mm});
            skLineSegment(sketch, "E1904", {"start": v(10.82, 64.74) * mm, "end": v(10.78, 64.72) * mm});
            skLineSegment(sketch, "E1905", {"start": v(10.78, 64.72) * mm, "end": v(10.74, 64.7) * mm});
            skLineSegment(sketch, "E1906", {"start": v(10.74, 64.7) * mm, "end": v(10.7, 64.67) * mm});
            skLineSegment(sketch, "E1907", {"start": v(10.7, 64.67) * mm, "end": v(10.65, 64.63) * mm});
            skLineSegment(sketch, "E1908", {"start": v(10.65, 64.63) * mm, "end": v(10.62, 64.58) * mm});
            skLineSegment(sketch, "E1909", {"start": v(10.62, 64.58) * mm, "end": v(10.59, 64.53) * mm});
            skLineSegment(sketch, "E1910", {"start": v(10.59, 64.53) * mm, "end": v(10.57, 64.5) * mm});
            skLineSegment(sketch, "E1911", {"start": v(10.57, 64.5) * mm, "end": v(10.56, 64.47) * mm});
            skLineSegment(sketch, "E1912", {"start": v(10.56, 64.47) * mm, "end": v(10.56, 64.39) * mm});
            skLineSegment(sketch, "E1913", {"start": v(10.56, 64.39) * mm, "end": v(10.56, 64.3) * mm});
            skLineSegment(sketch, "E1914", {"start": v(10.56, 64.3) * mm, "end": v(10.58, 64.25) * mm});
            skLineSegment(sketch, "E1915", {"start": v(10.58, 64.25) * mm, "end": v(10.63, 64.12) * mm});
            skLineSegment(sketch, "E1916", {"start": v(10.63, 64.12) * mm, "end": v(10.7, 64) * mm});
            skLineSegment(sketch, "E1917", {"start": v(10.7, 64) * mm, "end": v(10.72, 63.96) * mm});
            skLineSegment(sketch, "E1918", {"start": v(10.72, 63.96) * mm, "end": v(10.76, 63.88) * mm});
            skLineSegment(sketch, "E1919", {"start": v(10.76, 63.88) * mm, "end": v(10.82, 63.77) * mm});
            skLineSegment(sketch, "E1920", {"start": v(10.82, 63.77) * mm, "end": v(10.87, 63.67) * mm});
            skLineSegment(sketch, "E1921", {"start": v(10.87, 63.67) * mm, "end": v(10.9, 63.56) * mm});
            skLineSegment(sketch, "E1922", {"start": v(10.9, 63.56) * mm, "end": v(10.94, 63.46) * mm});
            skLineSegment(sketch, "E1923", {"start": v(10.94, 63.46) * mm, "end": v(10.97, 63.35) * mm});
            skLineSegment(sketch, "E1924", {"start": v(10.97, 63.35) * mm, "end": v(10.99, 63.25) * mm});
            skLineSegment(sketch, "E1925", {"start": v(10.99, 63.25) * mm, "end": v(11, 63.16) * mm});
            skLineSegment(sketch, "E1926", {"start": v(11, 63.16) * mm, "end": v(11, 63.06) * mm});
            skLineSegment(sketch, "E1927", {"start": v(11, 63.06) * mm, "end": v(11, 62.97) * mm});
            skLineSegment(sketch, "E1928", {"start": v(11, 62.97) * mm, "end": v(10.98, 62.87) * mm});
            skLineSegment(sketch, "E1929", {"start": v(10.98, 62.87) * mm, "end": v(10.96, 62.78) * mm});
            skLineSegment(sketch, "E1930", {"start": v(10.96, 62.78) * mm, "end": v(10.93, 62.69) * mm});
            skLineSegment(sketch, "E1931", {"start": v(10.93, 62.69) * mm, "end": v(10.91, 62.63) * mm});
            skLineSegment(sketch, "E1932", {"start": v(10.91, 62.63) * mm, "end": v(10.92, 62.62) * mm});
            skLineSegment(sketch, "E1933", {"start": v(10.92, 62.62) * mm, "end": v(10.92, 62.62) * mm});
            skLineSegment(sketch, "E1934", {"start": v(10.92, 62.62) * mm, "end": v(10.9, 62.63) * mm});
            skLineSegment(sketch, "E1935", {"start": v(10.9, 62.63) * mm, "end": v(10.85, 62.51) * mm});
            skLineSegment(sketch, "E1936", {"start": v(10.85, 62.51) * mm, "end": v(11.44, 61.93) * mm});
            skLineSegment(sketch, "E1937", {"start": v(11.44, 61.93) * mm, "end": v(11.5, 61.96) * mm});
            skLineSegment(sketch, "E1938", {"start": v(11.5, 61.96) * mm, "end": v(11.57, 61.99) * mm});
            skLineSegment(sketch, "E1939", {"start": v(11.57, 61.99) * mm, "end": v(11.63, 62.01) * mm});
            skLineSegment(sketch, "E1940", {"start": v(11.63, 62.01) * mm, "end": v(11.7, 62.03) * mm});
            skLineSegment(sketch, "E1941", {"start": v(11.7, 62.03) * mm, "end": v(11.78, 62.05) * mm});
            skLineSegment(sketch, "E1942", {"start": v(11.78, 62.05) * mm, "end": v(11.87, 62.07) * mm});
            skLineSegment(sketch, "E1943", {"start": v(11.87, 62.07) * mm, "end": v(12, 62.07) * mm});
            skLineSegment(sketch, "E1944", {"start": v(12, 62.07) * mm, "end": v(12.13, 62.07) * mm});
            skLineSegment(sketch, "E1945", {"start": v(12.13, 62.07) * mm, "end": v(12.2, 62.06) * mm});
            skLineSegment(sketch, "E1946", {"start": v(12.2, 62.06) * mm, "end": v(12.29, 62.04) * mm});
            skLineSegment(sketch, "E1947", {"start": v(12.29, 62.04) * mm, "end": v(12.39, 62.01) * mm});
            skLineSegment(sketch, "E1948", {"start": v(12.39, 62.01) * mm, "end": v(12.48, 61.98) * mm});
            skLineSegment(sketch, "E1949", {"start": v(12.48, 61.98) * mm, "end": v(12.57, 61.95) * mm});
            skLineSegment(sketch, "E1950", {"start": v(12.57, 61.95) * mm, "end": v(12.76, 61.86) * mm});
            skLineSegment(sketch, "E1951", {"start": v(12.76, 61.86) * mm, "end": v(12.85, 61.81) * mm});
            skLineSegment(sketch, "E1952", {"start": v(12.85, 61.81) * mm, "end": v(12.91, 61.78) * mm});
            skLineSegment(sketch, "E1953", {"start": v(12.91, 61.78) * mm, "end": v(12.93, 61.76) * mm});
            skLineSegment(sketch, "E1954", {"start": v(12.93, 61.76) * mm, "end": v(13, 61.73) * mm});
            skLineSegment(sketch, "E1955", {"start": v(13, 61.73) * mm, "end": v(13.1, 61.68) * mm});
            skLineSegment(sketch, "E1956", {"start": v(13.1, 61.68) * mm, "end": v(13.2, 61.64) * mm});
            skLineSegment(sketch, "E1957", {"start": v(-4.4, 62.73) * mm, "end": v(-4.11, 62.44) * mm});
            skLineSegment(sketch, "E1958", {"start": v(-4.11, 62.44) * mm, "end": v(-4.1, 62.44) * mm});
            skLineSegment(sketch, "E1959", {"start": v(-4.1, 62.44) * mm, "end": v(-4.03, 62.5) * mm});
            skLineSegment(sketch, "E1960", {"start": v(-4.03, 62.5) * mm, "end": v(-3.94, 62.55) * mm});
            skLineSegment(sketch, "E1961", {"start": v(-3.94, 62.55) * mm, "end": v(-3.85, 62.6) * mm});
            skLineSegment(sketch, "E1962", {"start": v(-3.85, 62.6) * mm, "end": v(-3.74, 62.65) * mm});
            skLineSegment(sketch, "E1963", {"start": v(-3.74, 62.65) * mm, "end": v(-3.69, 62.67) * mm});
            skLineSegment(sketch, "E1964", {"start": v(-3.69, 62.67) * mm, "end": v(-3.55, 62.7) * mm});
            skLineSegment(sketch, "E1965", {"start": v(-3.55, 62.7) * mm, "end": v(-3.42, 62.73) * mm});
            skLineSegment(sketch, "E1966", {"start": v(-3.42, 62.73) * mm, "end": v(-3.3, 62.74) * mm});
            skLineSegment(sketch, "E1967", {"start": v(-3.3, 62.74) * mm, "end": v(-3.16, 62.73) * mm});
            skLineSegment(sketch, "E1968", {"start": v(-3.16, 62.73) * mm, "end": v(-3.02, 62.72) * mm});
            skLineSegment(sketch, "E1969", {"start": v(-3.02, 62.72) * mm, "end": v(-2.89, 62.68) * mm});
            skLineSegment(sketch, "E1970", {"start": v(-2.89, 62.68) * mm, "end": v(-2.74, 62.63) * mm});
            skLineSegment(sketch, "E1971", {"start": v(-2.74, 62.63) * mm, "end": v(-2.6, 62.57) * mm});
            skLineSegment(sketch, "E1972", {"start": v(-2.6, 62.57) * mm, "end": v(-2.47, 62.51) * mm});
            skLineSegment(sketch, "E1973", {"start": v(-2.47, 62.51) * mm, "end": v(-2.44, 62.5) * mm});
            skLineSegment(sketch, "E1974", {"start": v(-2.44, 62.5) * mm, "end": v(-2.4, 62.5) * mm});
            skLineSegment(sketch, "E1975", {"start": v(-2.4, 62.5) * mm, "end": v(-2.35, 62.51) * mm});
            skLineSegment(sketch, "E1976", {"start": v(-2.35, 62.51) * mm, "end": v(-2.31, 62.54) * mm});
            skLineSegment(sketch, "E1977", {"start": v(-2.31, 62.54) * mm, "end": v(-2.27, 62.57) * mm});
            skLineSegment(sketch, "E1978", {"start": v(-2.27, 62.57) * mm, "end": v(-2.23, 62.63) * mm});
            skLineSegment(sketch, "E1979", {"start": v(-2.23, 62.63) * mm, "end": v(-2.21, 62.68) * mm});
            skLineSegment(sketch, "E1980", {"start": v(-2.21, 62.68) * mm, "end": v(-2.2, 62.72) * mm});
            skLineSegment(sketch, "E1981", {"start": v(-2.2, 62.72) * mm, "end": v(-2.21, 62.77) * mm});
            skLineSegment(sketch, "E1982", {"start": v(-2.21, 62.77) * mm, "end": v(-2.23, 62.8) * mm});
            skLineSegment(sketch, "E1983", {"start": v(-2.23, 62.8) * mm, "end": v(-3.28, 63.86) * mm});
            skLineSegment(sketch, "E1984", {"start": v(-3.28, 63.86) * mm, "end": v(-4.4, 62.73) * mm});
            skLineSegment(sketch, "E1985", {"start": v(-2.45, 57.32) * mm, "end": v(-2.42, 57.3) * mm});
            skLineSegment(sketch, "E1986", {"start": v(-2.42, 57.3) * mm, "end": v(-2.4, 57.3) * mm});
            skLineSegment(sketch, "E1987", {"start": v(-2.4, 57.3) * mm, "end": v(-2.35, 57.3) * mm});
            skLineSegment(sketch, "E1988", {"start": v(-2.35, 57.3) * mm, "end": v(-2.3, 57.32) * mm});
            skLineSegment(sketch, "E1989", {"start": v(-2.3, 57.32) * mm, "end": v(-2.25, 57.35) * mm});
            skLineSegment(sketch, "E1990", {"start": v(-2.25, 57.35) * mm, "end": v(-2.2, 57.38) * mm});
            skLineSegment(sketch, "E1991", {"start": v(-2.2, 57.38) * mm, "end": v(-2.17, 57.4) * mm});
            skLineSegment(sketch, "E1992", {"start": v(-2.17, 57.4) * mm, "end": v(-0.86, 58.72) * mm});
            skLineSegment(sketch, "E1993", {"start": v(-0.86, 58.72) * mm, "end": v(-0.86, 58.73) * mm});
            skLineSegment(sketch, "E1994", {"start": v(-0.86, 58.73) * mm, "end": v(-4.63, 62.5) * mm});
            skLineSegment(sketch, "E1995", {"start": v(-4.63, 62.5) * mm, "end": v(-4.64, 62.5) * mm});
            skLineSegment(sketch, "E1996", {"start": v(-4.64, 62.5) * mm, "end": v(-6, 61.13) * mm});
            skLineSegment(sketch, "E1997", {"start": v(-6, 61.13) * mm, "end": v(-6.02, 61.09) * mm});
            skLineSegment(sketch, "E1998", {"start": v(-6.02, 61.09) * mm, "end": v(-6.05, 61.02) * mm});
            skLineSegment(sketch, "E1999", {"start": v(-6.05, 61.02) * mm, "end": v(-6.05, 60.96) * mm});
            skLineSegment(sketch, "E2000", {"start": v(-6.05, 60.96) * mm, "end": v(-6.05, 60.93) * mm});
            skLineSegment(sketch, "E2001", {"start": v(-6.05, 60.93) * mm, "end": v(-6.04, 60.9) * mm});
            skLineSegment(sketch, "E2002", {"start": v(-6.04, 60.9) * mm, "end": v(-6.02, 60.86) * mm});
            skLineSegment(sketch, "E2003", {"start": v(-6.02, 60.86) * mm, "end": v(-5.98, 60.82) * mm});
            skLineSegment(sketch, "E2004", {"start": v(-5.98, 60.82) * mm, "end": v(-5.93, 60.79) * mm});
            skLineSegment(sketch, "E2005", {"start": v(-5.93, 60.79) * mm, "end": v(-5.88, 60.77) * mm});
            skLineSegment(sketch, "E2006", {"start": v(-5.88, 60.77) * mm, "end": v(-5.83, 60.78) * mm});
            skLineSegment(sketch, "E2007", {"start": v(-5.83, 60.78) * mm, "end": v(-5.78, 60.8) * mm});
            skLineSegment(sketch, "E2008", {"start": v(-5.78, 60.8) * mm, "end": v(-5.72, 60.82) * mm});
            skLineSegment(sketch, "E2009", {"start": v(-5.72, 60.82) * mm, "end": v(-5.62, 60.86) * mm});
            skLineSegment(sketch, "E2010", {"start": v(-5.62, 60.86) * mm, "end": v(-5.58, 60.87) * mm});
            skLineSegment(sketch, "E2011", {"start": v(-5.58, 60.87) * mm, "end": v(-5.55, 60.87) * mm});
            skLineSegment(sketch, "E2012", {"start": v(-5.55, 60.87) * mm, "end": v(-5.51, 60.87) * mm});
            skLineSegment(sketch, "E2013", {"start": v(-5.51, 60.87) * mm, "end": v(-5.48, 60.86) * mm});
            skLineSegment(sketch, "E2014", {"start": v(-5.48, 60.86) * mm, "end": v(-5.45, 60.84) * mm});
            skLineSegment(sketch, "E2015", {"start": v(-5.45, 60.84) * mm, "end": v(-5.42, 60.81) * mm});
            skLineSegment(sketch, "E2016", {"start": v(-5.42, 60.81) * mm, "end": v(-5.4, 60.8) * mm});
            skLineSegment(sketch, "E2017", {"start": v(-5.4, 60.8) * mm, "end": v(-2.53, 57.93) * mm});
            skLineSegment(sketch, "E2018", {"start": v(-2.53, 57.93) * mm, "end": v(-2.51, 57.9) * mm});
            skLineSegment(sketch, "E2019", {"start": v(-2.51, 57.9) * mm, "end": v(-2.5, 57.87) * mm});
            skLineSegment(sketch, "E2020", {"start": v(-2.5, 57.87) * mm, "end": v(-2.49, 57.84) * mm});
            skLineSegment(sketch, "E2021", {"start": v(-2.49, 57.84) * mm, "end": v(-2.48, 57.8) * mm});
            skLineSegment(sketch, "E2022", {"start": v(-2.48, 57.8) * mm, "end": v(-2.49, 57.76) * mm});
            skLineSegment(sketch, "E2023", {"start": v(-2.49, 57.76) * mm, "end": v(-2.5, 57.7) * mm});
            skLineSegment(sketch, "E2024", {"start": v(-2.5, 57.7) * mm, "end": v(-2.54, 57.64) * mm});
            skLineSegment(sketch, "E2025", {"start": v(-2.54, 57.64) * mm, "end": v(-2.57, 57.56) * mm});
            skLineSegment(sketch, "E2026", {"start": v(-2.57, 57.56) * mm, "end": v(-2.58, 57.5) * mm});
            skLineSegment(sketch, "E2027", {"start": v(-2.58, 57.5) * mm, "end": v(-2.57, 57.44) * mm});
            skLineSegment(sketch, "E2028", {"start": v(-2.57, 57.44) * mm, "end": v(-2.56, 57.4) * mm});
            skLineSegment(sketch, "E2029", {"start": v(-2.56, 57.4) * mm, "end": v(-2.54, 57.37) * mm});
            skLineSegment(sketch, "E2030", {"start": v(-2.54, 57.37) * mm, "end": v(-2.51, 57.35) * mm});
            skLineSegment(sketch, "E2031", {"start": v(-2.51, 57.35) * mm, "end": v(-2.48, 57.33) * mm});
            skLineSegment(sketch, "E2032", {"start": v(-2.48, 57.33) * mm, "end": v(-2.45, 57.32) * mm});
            skLineSegment(sketch, "E2033", {"start": v(5.94, 50.33) * mm, "end": v(6.36, 50.12) * mm});
            skLineSegment(sketch, "E2034", {"start": v(6.36, 50.12) * mm, "end": v(6.37, 50.12) * mm});
            skLineSegment(sketch, "E2035", {"start": v(6.37, 50.12) * mm, "end": v(6.64, 50.4) * mm});
            skLineSegment(sketch, "E2036", {"start": v(6.64, 50.4) * mm, "end": v(6.54, 50.57) * mm});
            skLineSegment(sketch, "E2037", {"start": v(6.54, 50.57) * mm, "end": v(6.34, 50.94) * mm});
            skLineSegment(sketch, "E2038", {"start": v(6.34, 50.94) * mm, "end": v(6.32, 51) * mm});
            skLineSegment(sketch, "E2039", {"start": v(6.32, 51) * mm, "end": v(6.27, 51.08) * mm});
            skLineSegment(sketch, "E2040", {"start": v(6.27, 51.08) * mm, "end": v(6.25, 51.1) * mm});
            skLineSegment(sketch, "E2041", {"start": v(6.25, 51.1) * mm, "end": v(6.24, 51.12) * mm});
            skLineSegment(sketch, "E2042", {"start": v(6.24, 51.12) * mm, "end": v(6.24, 51.12) * mm});
            skLineSegment(sketch, "E2043", {"start": v(6.24, 51.12) * mm, "end": v(6.24, 51.13) * mm});
            skLineSegment(sketch, "E2044", {"start": v(6.24, 51.13) * mm, "end": v(6.24, 51.14) * mm});
            skLineSegment(sketch, "E2045", {"start": v(6.24, 51.14) * mm, "end": v(6.23, 51.15) * mm});
            skLineSegment(sketch, "E2046", {"start": v(6.23, 51.15) * mm, "end": v(6.16, 51.28) * mm});
            skLineSegment(sketch, "E2047", {"start": v(6.16, 51.28) * mm, "end": v(6.15, 51.3) * mm});
            skLineSegment(sketch, "E2048", {"start": v(6.15, 51.3) * mm, "end": v(6.07, 51.44) * mm});
            skLineSegment(sketch, "E2049", {"start": v(6.07, 51.44) * mm, "end": v(6.07, 51.46) * mm});
            skLineSegment(sketch, "E2050", {"start": v(6.07, 51.46) * mm, "end": v(6.03, 51.52) * mm});
            skLineSegment(sketch, "E2051", {"start": v(6.03, 51.52) * mm, "end": v(5.97, 51.63) * mm});
            skLineSegment(sketch, "E2052", {"start": v(5.97, 51.63) * mm, "end": v(5.94, 51.7) * mm});
            skLineSegment(sketch, "E2053", {"start": v(5.94, 51.7) * mm, "end": v(5.93, 51.7) * mm});
            skLineSegment(sketch, "E2054", {"start": v(5.93, 51.7) * mm, "end": v(5.93, 51.7) * mm});
            skLineSegment(sketch, "E2055", {"start": v(5.93, 51.7) * mm, "end": v(5.92, 51.73) * mm});
            skLineSegment(sketch, "E2056", {"start": v(5.92, 51.73) * mm, "end": v(5.9, 51.75) * mm});
            skLineSegment(sketch, "E2057", {"start": v(5.9, 51.75) * mm, "end": v(5.69, 52.16) * mm});
            skLineSegment(sketch, "E2058", {"start": v(5.69, 52.16) * mm, "end": v(5.65, 52.23) * mm});
            skLineSegment(sketch, "E2059", {"start": v(5.65, 52.23) * mm, "end": v(5.51, 52.48) * mm});
            skLineSegment(sketch, "E2060", {"start": v(5.51, 52.48) * mm, "end": v(5.47, 52.56) * mm});
            skLineSegment(sketch, "E2061", {"start": v(5.47, 52.56) * mm, "end": v(5.34, 52.8) * mm});
            skLineSegment(sketch, "E2062", {"start": v(5.34, 52.8) * mm, "end": v(5.28, 52.9) * mm});
            skLineSegment(sketch, "E2063", {"start": v(5.28, 52.9) * mm, "end": v(5.06, 53.31) * mm});
            skLineSegment(sketch, "E2064", {"start": v(5.06, 53.31) * mm, "end": v(5.02, 53.39) * mm});
            skLineSegment(sketch, "E2065", {"start": v(5.02, 53.39) * mm, "end": v(4.91, 53.58) * mm});
            skLineSegment(sketch, "E2066", {"start": v(4.91, 53.58) * mm, "end": v(4.85, 53.7) * mm});
            skLineSegment(sketch, "E2067", {"start": v(4.85, 53.7) * mm, "end": v(4.57, 54.22) * mm});
            skLineSegment(sketch, "E2068", {"start": v(4.57, 54.22) * mm, "end": v(4.53, 54.3) * mm});
            skLineSegment(sketch, "E2069", {"start": v(4.53, 54.3) * mm, "end": v(4.42, 54.49) * mm});
            skLineSegment(sketch, "E2070", {"start": v(4.42, 54.49) * mm, "end": v(4.36, 54.6) * mm});
            skLineSegment(sketch, "E2071", {"start": v(4.36, 54.6) * mm, "end": v(4.34, 54.65) * mm});
            skLineSegment(sketch, "E2072", {"start": v(4.34, 54.65) * mm, "end": v(4.28, 54.76) * mm});
            skLineSegment(sketch, "E2073", {"start": v(4.28, 54.76) * mm, "end": v(4.22, 54.87) * mm});
            skLineSegment(sketch, "E2074", {"start": v(4.22, 54.87) * mm, "end": v(4.1, 55.1) * mm});
            skLineSegment(sketch, "E2075", {"start": v(4.1, 55.1) * mm, "end": v(4.07, 55.15) * mm});
            skLineSegment(sketch, "E2076", {"start": v(4.07, 55.15) * mm, "end": v(4.06, 55.15) * mm});
            skLineSegment(sketch, "E2077", {"start": v(4.06, 55.15) * mm, "end": v(4.06, 55.15) * mm});
            skLineSegment(sketch, "E2078", {"start": v(4.06, 55.15) * mm, "end": v(4.07, 55.16) * mm});
            skLineSegment(sketch, "E2079", {"start": v(4.07, 55.16) * mm, "end": v(4.04, 55.2) * mm});
            skLineSegment(sketch, "E2080", {"start": v(4.04, 55.2) * mm, "end": v(3.97, 55.32) * mm});
            skLineSegment(sketch, "E2081", {"start": v(3.97, 55.32) * mm, "end": v(3.94, 55.4) * mm});
            skLineSegment(sketch, "E2082", {"start": v(3.94, 55.4) * mm, "end": v(3.93, 55.4) * mm});
            skLineSegment(sketch, "E2083", {"start": v(3.93, 55.4) * mm, "end": v(3.89, 55.48) * mm});
            skLineSegment(sketch, "E2084", {"start": v(3.89, 55.48) * mm, "end": v(3.82, 55.6) * mm});
            skLineSegment(sketch, "E2085", {"start": v(3.82, 55.6) * mm, "end": v(3.8, 55.65) * mm});
            skLineSegment(sketch, "E2086", {"start": v(3.8, 55.65) * mm, "end": v(3.8, 55.65) * mm});
            skLineSegment(sketch, "E2087", {"start": v(3.8, 55.65) * mm, "end": v(3.76, 55.71) * mm});
            skLineSegment(sketch, "E2088", {"start": v(3.76, 55.71) * mm, "end": v(3.73, 55.77) * mm});
            skLineSegment(sketch, "E2089", {"start": v(3.73, 55.77) * mm, "end": v(3.6, 56.03) * mm});
            skLineSegment(sketch, "E2090", {"start": v(3.6, 56.03) * mm, "end": v(3.55, 56.1) * mm});
            skLineSegment(sketch, "E2091", {"start": v(3.55, 56.1) * mm, "end": v(3.43, 56.33) * mm});
            skLineSegment(sketch, "E2092", {"start": v(3.43, 56.33) * mm, "end": v(3.2, 56.76) * mm});
            skLineSegment(sketch, "E2093", {"start": v(3.2, 56.76) * mm, "end": v(3.15, 56.85) * mm});
            skLineSegment(sketch, "E2094", {"start": v(3.15, 56.85) * mm, "end": v(3.02, 57.08) * mm});
            skLineSegment(sketch, "E2095", {"start": v(3.02, 57.08) * mm, "end": v(2.98, 57.16) * mm});
            skLineSegment(sketch, "E2096", {"start": v(2.98, 57.16) * mm, "end": v(2.8, 57.5) * mm});
            skLineSegment(sketch, "E2097", {"start": v(2.8, 57.5) * mm, "end": v(2.79, 57.5) * mm});
            skLineSegment(sketch, "E2098", {"start": v(2.79, 57.5) * mm, "end": v(2.78, 57.52) * mm});
            skLineSegment(sketch, "E2099", {"start": v(2.78, 57.52) * mm, "end": v(2.79, 57.53) * mm});
            skLineSegment(sketch, "E2100", {"start": v(2.79, 57.53) * mm, "end": v(7.42, 52.9) * mm});
            skLineSegment(sketch, "E2101", {"start": v(7.42, 52.9) * mm, "end": v(7.44, 52.88) * mm});
            skLineSegment(sketch, "E2102", {"start": v(7.44, 52.88) * mm, "end": v(7.46, 52.85) * mm});
            skLineSegment(sketch, "E2103", {"start": v(7.46, 52.85) * mm, "end": v(7.47, 52.84) * mm});
            skLineSegment(sketch, "E2104", {"start": v(7.47, 52.84) * mm, "end": v(7.49, 52.8) * mm});
            skLineSegment(sketch, "E2105", {"start": v(7.49, 52.8) * mm, "end": v(7.51, 52.77) * mm});
            skLineSegment(sketch, "E2106", {"start": v(7.51, 52.77) * mm, "end": v(7.53, 52.73) * mm});
            skLineSegment(sketch, "E2107", {"start": v(7.53, 52.73) * mm, "end": v(7.54, 52.69) * mm});
            skLineSegment(sketch, "E2108", {"start": v(7.54, 52.69) * mm, "end": v(7.54, 52.65) * mm});
            skLineSegment(sketch, "E2109", {"start": v(7.54, 52.65) * mm, "end": v(7.54, 52.6) * mm});
            skLineSegment(sketch, "E2110", {"start": v(7.54, 52.6) * mm, "end": v(7.53, 52.55) * mm});
            skLineSegment(sketch, "E2111", {"start": v(7.53, 52.55) * mm, "end": v(7.51, 52.5) * mm});
            skLineSegment(sketch, "E2112", {"start": v(7.51, 52.5) * mm, "end": v(7.5, 52.45) * mm});
            skLineSegment(sketch, "E2113", {"start": v(7.5, 52.45) * mm, "end": v(7.48, 52.4) * mm});
            skLineSegment(sketch, "E2114", {"start": v(7.48, 52.4) * mm, "end": v(7.37, 52.2) * mm});
            skLineSegment(sketch, "E2115", {"start": v(7.37, 52.2) * mm, "end": v(7.36, 52.15) * mm});
            skLineSegment(sketch, "E2116", {"start": v(7.36, 52.15) * mm, "end": v(7.35, 52.1) * mm});
            skLineSegment(sketch, "E2117", {"start": v(7.35, 52.1) * mm, "end": v(7.35, 52.05) * mm});
            skLineSegment(sketch, "E2118", {"start": v(7.35, 52.05) * mm, "end": v(7.35, 52) * mm});
            skLineSegment(sketch, "E2119", {"start": v(7.35, 52) * mm, "end": v(7.36, 51.95) * mm});
            skLineSegment(sketch, "E2120", {"start": v(7.36, 51.95) * mm, "end": v(7.38, 51.91) * mm});
            skLineSegment(sketch, "E2121", {"start": v(7.38, 51.91) * mm, "end": v(7.4, 51.88) * mm});
            skLineSegment(sketch, "E2122", {"start": v(7.4, 51.88) * mm, "end": v(7.42, 51.84) * mm});
            skLineSegment(sketch, "E2123", {"start": v(7.42, 51.84) * mm, "end": v(7.45, 51.8) * mm});
            skLineSegment(sketch, "E2124", {"start": v(7.45, 51.8) * mm, "end": v(7.48, 51.78) * mm});
            skLineSegment(sketch, "E2125", {"start": v(7.48, 51.78) * mm, "end": v(7.52, 51.75) * mm});
            skLineSegment(sketch, "E2126", {"start": v(7.52, 51.75) * mm, "end": v(7.55, 51.72) * mm});
            skLineSegment(sketch, "E2127", {"start": v(7.55, 51.72) * mm, "end": v(7.6, 51.7) * mm});
            skLineSegment(sketch, "E2128", {"start": v(7.6, 51.7) * mm, "end": v(7.64, 51.69) * mm});
            skLineSegment(sketch, "E2129", {"start": v(7.64, 51.69) * mm, "end": v(7.72, 51.69) * mm});
            skLineSegment(sketch, "E2130", {"start": v(7.72, 51.69) * mm, "end": v(7.8, 51.69) * mm});
            skLineSegment(sketch, "E2131", {"start": v(7.8, 51.69) * mm, "end": v(7.85, 51.7) * mm});
            skLineSegment(sketch, "E2132", {"start": v(7.85, 51.7) * mm, "end": v(7.9, 51.73) * mm});
            skLineSegment(sketch, "E2133", {"start": v(7.9, 51.73) * mm, "end": v(7.97, 51.76) * mm});
            skLineSegment(sketch, "E2134", {"start": v(7.97, 51.76) * mm, "end": v(8.03, 51.8) * mm});
            skLineSegment(sketch, "E2135", {"start": v(8.03, 51.8) * mm, "end": v(8.08, 51.83) * mm});
            skLineSegment(sketch, "E2136", {"start": v(8.08, 51.83) * mm, "end": v(8.1, 51.86) * mm});
            skLineSegment(sketch, "E2137", {"start": v(8.1, 51.86) * mm, "end": v(10.82, 54.57) * mm});
            skLineSegment(sketch, "E2138", {"start": v(10.82, 54.57) * mm, "end": v(10.85, 54.61) * mm});
            skLineSegment(sketch, "E2139", {"start": v(10.85, 54.61) * mm, "end": v(10.88, 54.66) * mm});
            skLineSegment(sketch, "E2140", {"start": v(10.88, 54.66) * mm, "end": v(10.9, 54.7) * mm});
            skLineSegment(sketch, "E2141", {"start": v(10.9, 54.7) * mm, "end": v(10.9, 54.7) * mm});
            skLineSegment(sketch, "E2142", {"start": v(10.9, 54.7) * mm, "end": v(10.92, 54.71) * mm});
            skLineSegment(sketch, "E2143", {"start": v(10.92, 54.71) * mm, "end": v(10.94, 54.77) * mm});
            skLineSegment(sketch, "E2144", {"start": v(10.94, 54.77) * mm, "end": v(10.97, 54.86) * mm});
            skLineSegment(sketch, "E2145", {"start": v(10.97, 54.86) * mm, "end": v(10.97, 54.9) * mm});
            skLineSegment(sketch, "E2146", {"start": v(10.97, 54.9) * mm, "end": v(10.97, 54.94) * mm});
            skLineSegment(sketch, "E2147", {"start": v(10.97, 54.94) * mm, "end": v(10.97, 54.98) * mm});
            skLineSegment(sketch, "E2148", {"start": v(10.97, 54.98) * mm, "end": v(10.97, 55.02) * mm});
            skLineSegment(sketch, "E2149", {"start": v(10.97, 55.02) * mm, "end": v(10.95, 55.06) * mm});
            skLineSegment(sketch, "E2150", {"start": v(10.95, 55.06) * mm, "end": v(10.94, 55.1) * mm});
            skLineSegment(sketch, "E2151", {"start": v(10.94, 55.1) * mm, "end": v(10.92, 55.13) * mm});
            skLineSegment(sketch, "E2152", {"start": v(10.92, 55.13) * mm, "end": v(10.9, 55.16) * mm});
            skLineSegment(sketch, "E2153", {"start": v(10.9, 55.16) * mm, "end": v(10.84, 55.22) * mm});
            skLineSegment(sketch, "E2154", {"start": v(10.84, 55.22) * mm, "end": v(10.77, 55.27) * mm});
            skLineSegment(sketch, "E2155", {"start": v(10.77, 55.27) * mm, "end": v(10.73, 55.28) * mm});
            skLineSegment(sketch, "E2156", {"start": v(10.73, 55.28) * mm, "end": v(10.7, 55.3) * mm});
            skLineSegment(sketch, "E2157", {"start": v(10.7, 55.3) * mm, "end": v(10.66, 55.3) * mm});
            skLineSegment(sketch, "E2158", {"start": v(10.66, 55.3) * mm, "end": v(10.6, 55.3) * mm});
            skLineSegment(sketch, "E2159", {"start": v(10.6, 55.3) * mm, "end": v(10.56, 55.3) * mm});
            skLineSegment(sketch, "E2160", {"start": v(10.56, 55.3) * mm, "end": v(10.52, 55.3) * mm});
            skLineSegment(sketch, "E2161", {"start": v(10.52, 55.3) * mm, "end": v(10.47, 55.28) * mm});
            skLineSegment(sketch, "E2162", {"start": v(10.47, 55.28) * mm, "end": v(10.22, 55.16) * mm});
            skLineSegment(sketch, "E2163", {"start": v(10.22, 55.16) * mm, "end": v(10.16, 55.14) * mm});
            skLineSegment(sketch, "E2164", {"start": v(10.16, 55.14) * mm, "end": v(10.1, 55.13) * mm});
            skLineSegment(sketch, "E2165", {"start": v(10.1, 55.13) * mm, "end": v(10.04, 55.12) * mm});
            skLineSegment(sketch, "E2166", {"start": v(10.04, 55.12) * mm, "end": v(10, 55.12) * mm});
            skLineSegment(sketch, "E2167", {"start": v(10, 55.12) * mm, "end": v(9.96, 55.12) * mm});
            skLineSegment(sketch, "E2168", {"start": v(9.96, 55.12) * mm, "end": v(9.92, 55.13) * mm});
            skLineSegment(sketch, "E2169", {"start": v(9.92, 55.13) * mm, "end": v(9.88, 55.15) * mm});
            skLineSegment(sketch, "E2170", {"start": v(9.88, 55.15) * mm, "end": v(9.84, 55.17) * mm});
            skLineSegment(sketch, "E2171", {"start": v(9.84, 55.17) * mm, "end": v(9.84, 55.17) * mm});
            skLineSegment(sketch, "E2172", {"start": v(9.84, 55.17) * mm, "end": v(9.77, 55.23) * mm});
            skLineSegment(sketch, "E2173", {"start": v(9.77, 55.23) * mm, "end": v(9.77, 55.22) * mm});
            skLineSegment(sketch, "E2174", {"start": v(9.77, 55.22) * mm, "end": v(4.34, 60.65) * mm});
            skLineSegment(sketch, "E2175", {"start": v(4.34, 60.65) * mm, "end": v(4.3, 60.7) * mm});
            skLineSegment(sketch, "E2176", {"start": v(4.3, 60.7) * mm, "end": v(4.27, 60.75) * mm});
            skLineSegment(sketch, "E2177", {"start": v(4.27, 60.75) * mm, "end": v(4.24, 60.8) * mm});
            skLineSegment(sketch, "E2178", {"start": v(4.24, 60.8) * mm, "end": v(4.22, 60.85) * mm});
            skLineSegment(sketch, "E2179", {"start": v(4.22, 60.85) * mm, "end": v(4.22, 60.92) * mm});
            skLineSegment(sketch, "E2180", {"start": v(4.22, 60.92) * mm, "end": v(4.22, 60.98) * mm});
            skLineSegment(sketch, "E2181", {"start": v(4.22, 60.98) * mm, "end": v(4.24, 61.06) * mm});
            skLineSegment(sketch, "E2182", {"start": v(4.24, 61.06) * mm, "end": v(4.27, 61.13) * mm});
            skLineSegment(sketch, "E2183", {"start": v(4.27, 61.13) * mm, "end": v(4.38, 61.36) * mm});
            skLineSegment(sketch, "E2184", {"start": v(4.38, 61.36) * mm, "end": v(4.4, 61.4) * mm});
            skLineSegment(sketch, "E2185", {"start": v(4.4, 61.4) * mm, "end": v(4.4, 61.46) * mm});
            skLineSegment(sketch, "E2186", {"start": v(4.4, 61.46) * mm, "end": v(4.4, 61.52) * mm});
            skLineSegment(sketch, "E2187", {"start": v(4.4, 61.52) * mm, "end": v(4.4, 61.57) * mm});
            skLineSegment(sketch, "E2188", {"start": v(4.4, 61.57) * mm, "end": v(4.39, 61.62) * mm});
            skLineSegment(sketch, "E2189", {"start": v(4.39, 61.62) * mm, "end": v(4.37, 61.66) * mm});
            skLineSegment(sketch, "E2190", {"start": v(4.37, 61.66) * mm, "end": v(4.35, 61.7) * mm});
            skLineSegment(sketch, "E2191", {"start": v(4.35, 61.7) * mm, "end": v(4.32, 61.73) * mm});
            skLineSegment(sketch, "E2192", {"start": v(4.32, 61.73) * mm, "end": v(4.3, 61.76) * mm});
            skLineSegment(sketch, "E2193", {"start": v(4.3, 61.76) * mm, "end": v(4.26, 61.8) * mm});
            skLineSegment(sketch, "E2194", {"start": v(4.26, 61.8) * mm, "end": v(4.22, 61.82) * mm});
            skLineSegment(sketch, "E2195", {"start": v(4.22, 61.82) * mm, "end": v(4.18, 61.84) * mm});
            skLineSegment(sketch, "E2196", {"start": v(4.18, 61.84) * mm, "end": v(4.14, 61.86) * mm});
            skLineSegment(sketch, "E2197", {"start": v(4.14, 61.86) * mm, "end": v(4.1, 61.87) * mm});
            skLineSegment(sketch, "E2198", {"start": v(4.1, 61.87) * mm, "end": v(4.04, 61.87) * mm});
            skLineSegment(sketch, "E2199", {"start": v(4.04, 61.87) * mm, "end": v(3.98, 61.87) * mm});
            skLineSegment(sketch, "E2200", {"start": v(3.98, 61.87) * mm, "end": v(3.93, 61.86) * mm});
            skLineSegment(sketch, "E2201", {"start": v(3.93, 61.86) * mm, "end": v(3.88, 61.84) * mm});
            skLineSegment(sketch, "E2202", {"start": v(3.88, 61.84) * mm, "end": v(3.82, 61.82) * mm});
            skLineSegment(sketch, "E2203", {"start": v(3.82, 61.82) * mm, "end": v(3.76, 61.78) * mm});
            skLineSegment(sketch, "E2204", {"start": v(3.76, 61.78) * mm, "end": v(3.72, 61.75) * mm});
            skLineSegment(sketch, "E2205", {"start": v(3.72, 61.75) * mm, "end": v(3.67, 61.71) * mm});
            skLineSegment(sketch, "E2206", {"start": v(3.67, 61.71) * mm, "end": v(1.14, 59.18) * mm});
            skLineSegment(sketch, "E2207", {"start": v(1.14, 59.18) * mm, "end": v(1.15, 59.15) * mm});
            skLineSegment(sketch, "E2208", {"start": v(1.15, 59.15) * mm, "end": v(1.16, 59.13) * mm});
            skLineSegment(sketch, "E2209", {"start": v(1.16, 59.13) * mm, "end": v(1.17, 59.13) * mm});
            skLineSegment(sketch, "E2210", {"start": v(1.17, 59.13) * mm, "end": v(1.18, 59.13) * mm});
            skLineSegment(sketch, "E2211", {"start": v(1.18, 59.13) * mm, "end": v(1.18, 59.13) * mm});
            skLineSegment(sketch, "E2212", {"start": v(1.18, 59.13) * mm, "end": v(1.17, 59.12) * mm});
            skLineSegment(sketch, "E2213", {"start": v(1.17, 59.12) * mm, "end": v(1.22, 59.03) * mm});
            skLineSegment(sketch, "E2214", {"start": v(1.22, 59.03) * mm, "end": v(1.31, 58.86) * mm});
            skLineSegment(sketch, "E2215", {"start": v(1.31, 58.86) * mm, "end": v(1.35, 58.78) * mm});
            skLineSegment(sketch, "E2216", {"start": v(1.35, 58.78) * mm, "end": v(1.36, 58.77) * mm});
            skLineSegment(sketch, "E2217", {"start": v(1.36, 58.77) * mm, "end": v(1.37, 58.75) * mm});
            skLineSegment(sketch, "E2218", {"start": v(1.37, 58.75) * mm, "end": v(1.37, 58.75) * mm});
            skLineSegment(sketch, "E2219", {"start": v(1.37, 58.75) * mm, "end": v(1.52, 58.48) * mm});
            skLineSegment(sketch, "E2220", {"start": v(1.52, 58.48) * mm, "end": v(1.54, 58.43) * mm});
            skLineSegment(sketch, "E2221", {"start": v(1.54, 58.43) * mm, "end": v(1.62, 58.28) * mm});
            skLineSegment(sketch, "E2222", {"start": v(1.62, 58.28) * mm, "end": v(1.63, 58.26) * mm});
            skLineSegment(sketch, "E2223", {"start": v(1.63, 58.26) * mm, "end": v(1.67, 58.2) * mm});
            skLineSegment(sketch, "E2224", {"start": v(1.67, 58.2) * mm, "end": v(1.73, 58.09) * mm});
            skLineSegment(sketch, "E2225", {"start": v(1.73, 58.09) * mm, "end": v(1.75, 58.05) * mm});
            skLineSegment(sketch, "E2226", {"start": v(1.75, 58.05) * mm, "end": v(1.8, 57.96) * mm});
            skLineSegment(sketch, "E2227", {"start": v(1.8, 57.96) * mm, "end": v(1.94, 57.7) * mm});
            skLineSegment(sketch, "E2228", {"start": v(1.94, 57.7) * mm, "end": v(1.98, 57.63) * mm});
            skLineSegment(sketch, "E2229", {"start": v(1.98, 57.63) * mm, "end": v(1.98, 57.63) * mm});
            skLineSegment(sketch, "E2230", {"start": v(1.98, 57.63) * mm, "end": v(1.99, 57.63) * mm});
            skLineSegment(sketch, "E2231", {"start": v(1.99, 57.63) * mm, "end": v(1.98, 57.63) * mm});
            skLineSegment(sketch, "E2232", {"start": v(1.98, 57.63) * mm, "end": v(1.98, 57.62) * mm});
            skLineSegment(sketch, "E2233", {"start": v(1.98, 57.62) * mm, "end": v(2.18, 57.24) * mm});
            skLineSegment(sketch, "E2234", {"start": v(2.18, 57.24) * mm, "end": v(2.18, 57.25) * mm});
            skLineSegment(sketch, "E2235", {"start": v(2.18, 57.25) * mm, "end": v(2.18, 57.25) * mm});
            skLineSegment(sketch, "E2236", {"start": v(2.18, 57.25) * mm, "end": v(2.19, 57.23) * mm});
            skLineSegment(sketch, "E2237", {"start": v(2.19, 57.23) * mm, "end": v(2.2, 57.22) * mm});
            skLineSegment(sketch, "E2238", {"start": v(2.2, 57.22) * mm, "end": v(2.27, 57.09) * mm});
            skLineSegment(sketch, "E2239", {"start": v(2.27, 57.09) * mm, "end": v(2.28, 57.08) * mm});
            skLineSegment(sketch, "E2240", {"start": v(2.28, 57.08) * mm, "end": v(2.31, 57) * mm});
            skLineSegment(sketch, "E2241", {"start": v(2.31, 57) * mm, "end": v(2.4, 56.85) * mm});
            skLineSegment(sketch, "E2242", {"start": v(2.4, 56.85) * mm, "end": v(2.44, 56.77) * mm});
            skLineSegment(sketch, "E2243", {"start": v(2.44, 56.77) * mm, "end": v(2.48, 56.7) * mm});
            skLineSegment(sketch, "E2244", {"start": v(2.48, 56.7) * mm, "end": v(2.55, 56.56) * mm});
            skLineSegment(sketch, "E2245", {"start": v(2.55, 56.56) * mm, "end": v(2.7, 56.3) * mm});
            skLineSegment(sketch, "E2246", {"start": v(2.7, 56.3) * mm, "end": v(2.76, 56.18) * mm});
            skLineSegment(sketch, "E2247", {"start": v(2.76, 56.18) * mm, "end": v(2.78, 56.14) * mm});
            skLineSegment(sketch, "E2248", {"start": v(2.78, 56.14) * mm, "end": v(2.83, 56.04) * mm});
            skLineSegment(sketch, "E2249", {"start": v(2.83, 56.04) * mm, "end": v(2.87, 55.98) * mm});
            skLineSegment(sketch, "E2250", {"start": v(2.87, 55.98) * mm, "end": v(2.87, 55.97) * mm});
            skLineSegment(sketch, "E2251", {"start": v(2.87, 55.97) * mm, "end": v(2.88, 55.96) * mm});
            skLineSegment(sketch, "E2252", {"start": v(2.88, 55.96) * mm, "end": v(2.9, 55.93) * mm});
            skLineSegment(sketch, "E2253", {"start": v(2.9, 55.93) * mm, "end": v(2.91, 55.9) * mm});
            skLineSegment(sketch, "E2254", {"start": v(2.91, 55.9) * mm, "end": v(3.12, 55.51) * mm});
            skLineSegment(sketch, "E2255", {"start": v(3.12, 55.51) * mm, "end": v(3.19, 55.38) * mm});
            skLineSegment(sketch, "E2256", {"start": v(3.19, 55.38) * mm, "end": v(3.18, 55.37) * mm});
            skLineSegment(sketch, "E2257", {"start": v(3.18, 55.37) * mm, "end": v(3.18, 55.35) * mm});
            skLineSegment(sketch, "E2258", {"start": v(3.18, 55.35) * mm, "end": v(3.17, 55.35) * mm});
            skLineSegment(sketch, "E2259", {"start": v(3.17, 55.35) * mm, "end": v(2.87, 55.5) * mm});
            skLineSegment(sketch, "E2260", {"start": v(2.87, 55.5) * mm, "end": v(2.79, 55.54) * mm});
            skLineSegment(sketch, "E2261", {"start": v(2.79, 55.54) * mm, "end": v(2.62, 55.62) * mm});
            skLineSegment(sketch, "E2262", {"start": v(2.62, 55.62) * mm, "end": v(2.54, 55.65) * mm});
            skLineSegment(sketch, "E2263", {"start": v(2.54, 55.65) * mm, "end": v(2.2, 55.82) * mm});
            skLineSegment(sketch, "E2264", {"start": v(2.2, 55.82) * mm, "end": v(2.2, 55.82) * mm});
            skLineSegment(sketch, "E2265", {"start": v(2.2, 55.82) * mm, "end": v(1.78, 56.03) * mm});
            skLineSegment(sketch, "E2266", {"start": v(1.78, 56.03) * mm, "end": v(1.77, 56.03) * mm});
            skLineSegment(sketch, "E2267", {"start": v(1.77, 56.03) * mm, "end": v(1.37, 56.22) * mm});
            skLineSegment(sketch, "E2268", {"start": v(1.37, 56.22) * mm, "end": v(1.29, 56.26) * mm});
            skLineSegment(sketch, "E2269", {"start": v(1.29, 56.26) * mm, "end": v(0.94, 56.43) * mm});
            skLineSegment(sketch, "E2270", {"start": v(0.94, 56.43) * mm, "end": v(0.94, 56.43) * mm});
            skLineSegment(sketch, "E2271", {"start": v(0.94, 56.43) * mm, "end": v(0.52, 56.63) * mm});
            skLineSegment(sketch, "E2272", {"start": v(0.52, 56.63) * mm, "end": v(0.52, 56.63) * mm});
            skLineSegment(sketch, "E2273", {"start": v(0.52, 56.63) * mm, "end": v(0.3, 56.74) * mm});
            skLineSegment(sketch, "E2274", {"start": v(0.3, 56.74) * mm, "end": v(0.3, 56.74) * mm});
            skLineSegment(sketch, "E2275", {"start": v(0.3, 56.74) * mm, "end": v(0.29, 56.74) * mm});
            skLineSegment(sketch, "E2276", {"start": v(0.29, 56.74) * mm, "end": v(0.29, 56.74) * mm});
            skLineSegment(sketch, "E2277", {"start": v(0.29, 56.74) * mm, "end": v(0.3, 56.75) * mm});
            skLineSegment(sketch, "E2278", {"start": v(0.3, 56.75) * mm, "end": v(0.08, 56.85) * mm});
            skLineSegment(sketch, "E2279", {"start": v(0.08, 56.85) * mm, "end": v(-0.3, 57.03) * mm});
            skLineSegment(sketch, "E2280", {"start": v(-0.3, 57.03) * mm, "end": v(-0.38, 57.07) * mm});
            skLineSegment(sketch, "E2281", {"start": v(-0.38, 57.07) * mm, "end": v(-0.67, 57.2) * mm});
            skLineSegment(sketch, "E2282", {"start": v(-0.67, 57.2) * mm, "end": v(-0.78, 57.26) * mm});
            skLineSegment(sketch, "E2283", {"start": v(-0.78, 57.26) * mm, "end": v(-3.28, 54.77) * mm});
            skLineSegment(sketch, "E2284", {"start": v(-3.28, 54.77) * mm, "end": v(-3.33, 54.7) * mm});
            skLineSegment(sketch, "E2285", {"start": v(-3.33, 54.7) * mm, "end": v(-3.38, 54.63) * mm});
            skLineSegment(sketch, "E2286", {"start": v(-3.38, 54.63) * mm, "end": v(-3.41, 54.55) * mm});
            skLineSegment(sketch, "E2287", {"start": v(-3.41, 54.55) * mm, "end": v(-3.43, 54.48) * mm});
            skLineSegment(sketch, "E2288", {"start": v(-3.43, 54.48) * mm, "end": v(-3.44, 54.41) * mm});
            skLineSegment(sketch, "E2289", {"start": v(-3.44, 54.41) * mm, "end": v(-3.43, 54.34) * mm});
            skLineSegment(sketch, "E2290", {"start": v(-3.43, 54.34) * mm, "end": v(-3.4, 54.28) * mm});
            skLineSegment(sketch, "E2291", {"start": v(-3.4, 54.28) * mm, "end": v(-3.36, 54.21) * mm});
            skLineSegment(sketch, "E2292", {"start": v(-3.36, 54.21) * mm, "end": v(-3.3, 54.15) * mm});
            skLineSegment(sketch, "E2293", {"start": v(-3.3, 54.15) * mm, "end": v(-3.27, 54.12) * mm});
            skLineSegment(sketch, "E2294", {"start": v(-3.27, 54.12) * mm, "end": v(-3.23, 54.1) * mm});
            skLineSegment(sketch, "E2295", {"start": v(-3.23, 54.1) * mm, "end": v(-3.2, 54.07) * mm});
            skLineSegment(sketch, "E2296", {"start": v(-3.2, 54.07) * mm, "end": v(-3.15, 54.06) * mm});
            skLineSegment(sketch, "E2297", {"start": v(-3.15, 54.06) * mm, "end": v(-3.1, 54.06) * mm});
            skLineSegment(sketch, "E2298", {"start": v(-3.1, 54.06) * mm, "end": v(-3.06, 54.06) * mm});
            skLineSegment(sketch, "E2299", {"start": v(-3.06, 54.06) * mm, "end": v(-3.02, 54.06) * mm});
            skLineSegment(sketch, "E2300", {"start": v(-3.02, 54.06) * mm, "end": v(-2.97, 54.08) * mm});
            skLineSegment(sketch, "E2301", {"start": v(-2.97, 54.08) * mm, "end": v(-2.9, 54.11) * mm});
            skLineSegment(sketch, "E2302", {"start": v(-2.9, 54.11) * mm, "end": v(-2.86, 54.13) * mm});
            skLineSegment(sketch, "E2303", {"start": v(-2.86, 54.13) * mm, "end": v(-2.86, 54.14) * mm});
            skLineSegment(sketch, "E2304", {"start": v(-2.86, 54.14) * mm, "end": v(-2.86, 54.14) * mm});
            skLineSegment(sketch, "E2305", {"start": v(-2.86, 54.14) * mm, "end": v(-2.85, 54.14) * mm});
            skLineSegment(sketch, "E2306", {"start": v(-2.85, 54.14) * mm, "end": v(-2.84, 54.14) * mm});
            skLineSegment(sketch, "E2307", {"start": v(-2.84, 54.14) * mm, "end": v(-2.8, 54.18) * mm});
            skLineSegment(sketch, "E2308", {"start": v(-2.8, 54.18) * mm, "end": v(-2.7, 54.25) * mm});
            skLineSegment(sketch, "E2309", {"start": v(-2.7, 54.25) * mm, "end": v(-2.65, 54.29) * mm});
            skLineSegment(sketch, "E2310", {"start": v(-2.65, 54.29) * mm, "end": v(-2.6, 54.31) * mm});
            skLineSegment(sketch, "E2311", {"start": v(-2.6, 54.31) * mm, "end": v(-2.57, 54.33) * mm});
            skLineSegment(sketch, "E2312", {"start": v(-2.57, 54.33) * mm, "end": v(-2.52, 54.35) * mm});
            skLineSegment(sketch, "E2313", {"start": v(-2.52, 54.35) * mm, "end": v(-2.48, 54.35) * mm});
            skLineSegment(sketch, "E2314", {"start": v(-2.48, 54.35) * mm, "end": v(-2.43, 54.35) * mm});
            skLineSegment(sketch, "E2315", {"start": v(-2.43, 54.35) * mm, "end": v(-2.37, 54.34) * mm});
            skLineSegment(sketch, "E2316", {"start": v(-2.37, 54.34) * mm, "end": v(-2.31, 54.33) * mm});
            skLineSegment(sketch, "E2317", {"start": v(-2.31, 54.33) * mm, "end": v(-2.14, 54.29) * mm});
            skLineSegment(sketch, "E2318", {"start": v(-2.14, 54.29) * mm, "end": v(-2.02, 54.25) * mm});
            skLineSegment(sketch, "E2319", {"start": v(-2.02, 54.25) * mm, "end": v(-1.9, 54.21) * mm});
            skLineSegment(sketch, "E2320", {"start": v(-1.9, 54.21) * mm, "end": v(-1.8, 54.17) * mm});
            skLineSegment(sketch, "E2321", {"start": v(-1.8, 54.17) * mm, "end": v(-1.75, 54.14) * mm});
            skLineSegment(sketch, "E2322", {"start": v(-1.75, 54.14) * mm, "end": v(-1.2, 53.88) * mm});
            skLineSegment(sketch, "E2323", {"start": v(-1.2, 53.88) * mm, "end": v(0.1, 53.23) * mm});
            skLineSegment(sketch, "E2324", {"start": v(0.1, 53.23) * mm, "end": v(0.1, 53.22) * mm});
            skLineSegment(sketch, "E2325", {"start": v(0.1, 53.22) * mm, "end": v(0.13, 53.21) * mm});
            skLineSegment(sketch, "E2326", {"start": v(0.13, 53.21) * mm, "end": v(0.16, 53.2) * mm});
            skLineSegment(sketch, "E2327", {"start": v(0.16, 53.2) * mm, "end": v(0.8, 52.87) * mm});
            skLineSegment(sketch, "E2328", {"start": v(0.8, 52.87) * mm, "end": v(1.28, 52.64) * mm});
            skLineSegment(sketch, "E2329", {"start": v(1.28, 52.64) * mm, "end": v(2.35, 52.11) * mm});
            skLineSegment(sketch, "E2330", {"start": v(2.35, 52.11) * mm, "end": v(2.96, 51.81) * mm});
            skLineSegment(sketch, "E2331", {"start": v(2.96, 51.81) * mm, "end": v(4, 51.29) * mm});
            skLineSegment(sketch, "E2332", {"start": v(4, 51.29) * mm, "end": v(4.66, 50.97) * mm});
            skLineSegment(sketch, "E2333", {"start": v(4.66, 50.97) * mm, "end": v(5.1, 50.75) * mm});
            skLineSegment(sketch, "E2334", {"start": v(5.1, 50.75) * mm, "end": v(5.94, 50.33) * mm});
            skLineSegment(sketch, "E2335", {"start": v(11.39, 55.45) * mm, "end": v(11.43, 55.44) * mm});
            skLineSegment(sketch, "E2336", {"start": v(11.43, 55.44) * mm, "end": v(11.48, 55.44) * mm});
            skLineSegment(sketch, "E2337", {"start": v(11.48, 55.44) * mm, "end": v(11.54, 55.44) * mm});
            skLineSegment(sketch, "E2338", {"start": v(11.54, 55.44) * mm, "end": v(11.59, 55.45) * mm});
            skLineSegment(sketch, "E2339", {"start": v(11.59, 55.45) * mm, "end": v(11.64, 55.47) * mm});
            skLineSegment(sketch, "E2340", {"start": v(11.64, 55.47) * mm, "end": v(11.69, 55.5) * mm});
            skLineSegment(sketch, "E2341", {"start": v(11.69, 55.5) * mm, "end": v(11.74, 55.52) * mm});
            skLineSegment(sketch, "E2342", {"start": v(11.74, 55.52) * mm, "end": v(11.79, 55.55) * mm});
            skLineSegment(sketch, "E2343", {"start": v(11.79, 55.55) * mm, "end": v(11.82, 55.57) * mm});
            skLineSegment(sketch, "E2344", {"start": v(11.82, 55.57) * mm, "end": v(14.38, 58.13) * mm});
            skLineSegment(sketch, "E2345", {"start": v(14.38, 58.13) * mm, "end": v(7.23, 65.28) * mm});
            skLineSegment(sketch, "E2346", {"start": v(7.23, 65.28) * mm, "end": v(4.68, 62.72) * mm});
            skLineSegment(sketch, "E2347", {"start": v(4.68, 62.72) * mm, "end": v(4.65, 62.68) * mm});
            skLineSegment(sketch, "E2348", {"start": v(4.65, 62.68) * mm, "end": v(4.6, 62.62) * mm});
            skLineSegment(sketch, "E2349", {"start": v(4.6, 62.62) * mm, "end": v(4.58, 62.56) * mm});
            skLineSegment(sketch, "E2350", {"start": v(4.58, 62.56) * mm, "end": v(4.56, 62.5) * mm});
            skLineSegment(sketch, "E2351", {"start": v(4.56, 62.5) * mm, "end": v(4.54, 62.43) * mm});
            skLineSegment(sketch, "E2352", {"start": v(4.54, 62.43) * mm, "end": v(4.54, 62.37) * mm});
            skLineSegment(sketch, "E2353", {"start": v(4.54, 62.37) * mm, "end": v(4.54, 62.32) * mm});
            skLineSegment(sketch, "E2354", {"start": v(4.54, 62.32) * mm, "end": v(4.56, 62.26) * mm});
            skLineSegment(sketch, "E2355", {"start": v(4.56, 62.26) * mm, "end": v(4.58, 62.21) * mm});
            skLineSegment(sketch, "E2356", {"start": v(4.58, 62.21) * mm, "end": v(4.63, 62.14) * mm});
            skLineSegment(sketch, "E2357", {"start": v(4.63, 62.14) * mm, "end": v(4.65, 62.12) * mm});
            skLineSegment(sketch, "E2358", {"start": v(4.65, 62.12) * mm, "end": v(4.66, 62.11) * mm});
            skLineSegment(sketch, "E2359", {"start": v(4.66, 62.11) * mm, "end": v(4.67, 62.11) * mm});
            skLineSegment(sketch, "E2360", {"start": v(4.67, 62.11) * mm, "end": v(4.67, 62.1) * mm});
            skLineSegment(sketch, "E2361", {"start": v(4.67, 62.1) * mm, "end": v(4.67, 62.1) * mm});
            skLineSegment(sketch, "E2362", {"start": v(4.67, 62.1) * mm, "end": v(4.7, 62.08) * mm});
            skLineSegment(sketch, "E2363", {"start": v(4.7, 62.08) * mm, "end": v(4.75, 62.04) * mm});
            skLineSegment(sketch, "E2364", {"start": v(4.75, 62.04) * mm, "end": v(4.81, 62.02) * mm});
            skLineSegment(sketch, "E2365", {"start": v(4.81, 62.02) * mm, "end": v(4.87, 62) * mm});
            skLineSegment(sketch, "E2366", {"start": v(4.87, 62) * mm, "end": v(4.93, 62) * mm});
            skLineSegment(sketch, "E2367", {"start": v(4.93, 62) * mm, "end": v(5, 62.02) * mm});
            skLineSegment(sketch, "E2368", {"start": v(5, 62.02) * mm, "end": v(5.05, 62.03) * mm});
            skLineSegment(sketch, "E2369", {"start": v(5.05, 62.03) * mm, "end": v(5.3, 62.15) * mm});
            skLineSegment(sketch, "E2370", {"start": v(5.3, 62.15) * mm, "end": v(5.36, 62.17) * mm});
            skLineSegment(sketch, "E2371", {"start": v(5.36, 62.17) * mm, "end": v(5.42, 62.19) * mm});
            skLineSegment(sketch, "E2372", {"start": v(5.42, 62.19) * mm, "end": v(5.5, 62.2) * mm});
            skLineSegment(sketch, "E2373", {"start": v(5.5, 62.2) * mm, "end": v(5.57, 62.19) * mm});
            skLineSegment(sketch, "E2374", {"start": v(5.57, 62.19) * mm, "end": v(5.62, 62.17) * mm});
            skLineSegment(sketch, "E2375", {"start": v(5.62, 62.17) * mm, "end": v(5.7, 62.13) * mm});
            skLineSegment(sketch, "E2376", {"start": v(5.7, 62.13) * mm, "end": v(5.76, 62.07) * mm});
            skLineSegment(sketch, "E2377", {"start": v(5.76, 62.07) * mm, "end": v(5.79, 62.05) * mm});
            skLineSegment(sketch, "E2378", {"start": v(5.79, 62.05) * mm, "end": v(5.79, 62.05) * mm});
            skLineSegment(sketch, "E2379", {"start": v(5.79, 62.05) * mm, "end": v(5.8, 62.04) * mm});
            skLineSegment(sketch, "E2380", {"start": v(5.8, 62.04) * mm, "end": v(11.19, 56.64) * mm});
            skLineSegment(sketch, "E2381", {"start": v(11.19, 56.64) * mm, "end": v(11.22, 56.6) * mm});
            skLineSegment(sketch, "E2382", {"start": v(11.22, 56.6) * mm, "end": v(11.25, 56.55) * mm});
            skLineSegment(sketch, "E2383", {"start": v(11.25, 56.55) * mm, "end": v(11.28, 56.5) * mm});
            skLineSegment(sketch, "E2384", {"start": v(11.28, 56.5) * mm, "end": v(11.3, 56.46) * mm});
            skLineSegment(sketch, "E2385", {"start": v(11.3, 56.46) * mm, "end": v(11.3, 56.4) * mm});
            skLineSegment(sketch, "E2386", {"start": v(11.3, 56.4) * mm, "end": v(11.3, 56.35) * mm});
            skLineSegment(sketch, "E2387", {"start": v(11.3, 56.35) * mm, "end": v(11.29, 56.3) * mm});
            skLineSegment(sketch, "E2388", {"start": v(11.29, 56.3) * mm, "end": v(11.27, 56.26) * mm});
            skLineSegment(sketch, "E2389", {"start": v(11.27, 56.26) * mm, "end": v(11.25, 56.2) * mm});
            skLineSegment(sketch, "E2390", {"start": v(11.25, 56.2) * mm, "end": v(11.24, 56.17) * mm});
            skLineSegment(sketch, "E2391", {"start": v(11.24, 56.17) * mm, "end": v(11.12, 55.93) * mm});
            skLineSegment(sketch, "E2392", {"start": v(11.12, 55.93) * mm, "end": v(11.12, 55.89) * mm});
            skLineSegment(sketch, "E2393", {"start": v(11.12, 55.89) * mm, "end": v(11.1, 55.84) * mm});
            skLineSegment(sketch, "E2394", {"start": v(11.1, 55.84) * mm, "end": v(11.1, 55.8) * mm});
            skLineSegment(sketch, "E2395", {"start": v(11.1, 55.8) * mm, "end": v(11.11, 55.75) * mm});
            skLineSegment(sketch, "E2396", {"start": v(11.11, 55.75) * mm, "end": v(11.12, 55.71) * mm});
            skLineSegment(sketch, "E2397", {"start": v(11.12, 55.71) * mm, "end": v(11.13, 55.67) * mm});
            skLineSegment(sketch, "E2398", {"start": v(11.13, 55.67) * mm, "end": v(11.16, 55.63) * mm});
            skLineSegment(sketch, "E2399", {"start": v(11.16, 55.63) * mm, "end": v(11.19, 55.59) * mm});
            skLineSegment(sketch, "E2400", {"start": v(11.19, 55.59) * mm, "end": v(11.22, 55.55) * mm});
            skLineSegment(sketch, "E2401", {"start": v(11.22, 55.55) * mm, "end": v(11.26, 55.52) * mm});
            skLineSegment(sketch, "E2402", {"start": v(11.26, 55.52) * mm, "end": v(11.3, 55.49) * mm});
            skLineSegment(sketch, "E2403", {"start": v(11.3, 55.49) * mm, "end": v(11.34, 55.47) * mm});
            skLineSegment(sketch, "E2404", {"start": v(11.34, 55.47) * mm, "end": v(11.39, 55.45) * mm});
            skLineSegment(sketch, "E2405", {"start": v(0.17, 34.7) * mm, "end": v(0.2, 34.78) * mm});
            skLineSegment(sketch, "E2406", {"start": v(0.2, 34.78) * mm, "end": v(0.24, 34.85) * mm});
            skLineSegment(sketch, "E2407", {"start": v(0.24, 34.85) * mm, "end": v(0.24, 34.9) * mm});
            skLineSegment(sketch, "E2408", {"start": v(0.24, 34.9) * mm, "end": v(0.24, 34.94) * mm});
            skLineSegment(sketch, "E2409", {"start": v(0.24, 34.94) * mm, "end": v(0.22, 34.99) * mm});
            skLineSegment(sketch, "E2410", {"start": v(0.22, 34.99) * mm, "end": v(0.2, 35.04) * mm});
            skLineSegment(sketch, "E2411", {"start": v(0.2, 35.04) * mm, "end": v(-2.85, 38.09) * mm});
            skLineSegment(sketch, "E2412", {"start": v(-2.85, 38.09) * mm, "end": v(-2.9, 38.12) * mm});
            skLineSegment(sketch, "E2413", {"start": v(-2.9, 38.12) * mm, "end": v(-2.94, 38.14) * mm});
            skLineSegment(sketch, "E2414", {"start": v(-2.94, 38.14) * mm, "end": v(-2.98, 38.16) * mm});
            skLineSegment(sketch, "E2415", {"start": v(-2.98, 38.16) * mm, "end": v(-3.02, 38.17) * mm});
            skLineSegment(sketch, "E2416", {"start": v(-3.02, 38.17) * mm, "end": v(-3.06, 38.17) * mm});
            skLineSegment(sketch, "E2417", {"start": v(-3.06, 38.17) * mm, "end": v(-3.1, 38.16) * mm});
            skLineSegment(sketch, "E2418", {"start": v(-3.1, 38.16) * mm, "end": v(-3.16, 38.13) * mm});
            skLineSegment(sketch, "E2419", {"start": v(-3.16, 38.13) * mm, "end": v(-3.25, 38.09) * mm});
            skLineSegment(sketch, "E2420", {"start": v(-3.25, 38.09) * mm, "end": v(-3.32, 38.07) * mm});
            skLineSegment(sketch, "E2421", {"start": v(-3.32, 38.07) * mm, "end": v(-3.35, 38.07) * mm});
            skLineSegment(sketch, "E2422", {"start": v(-3.35, 38.07) * mm, "end": v(-3.38, 38.07) * mm});
            skLineSegment(sketch, "E2423", {"start": v(-3.38, 38.07) * mm, "end": v(-3.43, 38.08) * mm});
            skLineSegment(sketch, "E2424", {"start": v(-3.43, 38.08) * mm, "end": v(-3.46, 38.1) * mm});
            skLineSegment(sketch, "E2425", {"start": v(-3.46, 38.1) * mm, "end": v(-3.5, 38.12) * mm});
            skLineSegment(sketch, "E2426", {"start": v(-3.5, 38.12) * mm, "end": v(-3.51, 38.15) * mm});
            skLineSegment(sketch, "E2427", {"start": v(-3.51, 38.15) * mm, "end": v(-3.52, 38.16) * mm});
            skLineSegment(sketch, "E2428", {"start": v(-3.52, 38.16) * mm, "end": v(-3.52, 38.17) * mm});
            skLineSegment(sketch, "E2429", {"start": v(-3.52, 38.17) * mm, "end": v(-3.52, 38.16) * mm});
            skLineSegment(sketch, "E2430", {"start": v(-3.52, 38.16) * mm, "end": v(-3.53, 38.17) * mm});
            skLineSegment(sketch, "E2431", {"start": v(-3.53, 38.17) * mm, "end": v(-3.55, 38.2) * mm});
            skLineSegment(sketch, "E2432", {"start": v(-3.55, 38.2) * mm, "end": v(-3.56, 38.22) * mm});
            skLineSegment(sketch, "E2433", {"start": v(-3.56, 38.22) * mm, "end": v(-3.56, 38.25) * mm});
            skLineSegment(sketch, "E2434", {"start": v(-3.56, 38.25) * mm, "end": v(-3.57, 38.28) * mm});
            skLineSegment(sketch, "E2435", {"start": v(-3.57, 38.28) * mm, "end": v(-3.56, 38.3) * mm});
            skLineSegment(sketch, "E2436", {"start": v(-3.56, 38.3) * mm, "end": v(-3.54, 38.37) * mm});
            skLineSegment(sketch, "E2437", {"start": v(-3.54, 38.37) * mm, "end": v(-3.5, 38.43) * mm});
            skLineSegment(sketch, "E2438", {"start": v(-3.5, 38.43) * mm, "end": v(-3.47, 38.47) * mm});
            skLineSegment(sketch, "E2439", {"start": v(-3.47, 38.47) * mm, "end": v(-3.47, 38.47) * mm});
            skLineSegment(sketch, "E2440", {"start": v(-3.47, 38.47) * mm, "end": v(-2.04, 39.9) * mm});
            skLineSegment(sketch, "E2441", {"start": v(-2.04, 39.9) * mm, "end": v(1.96, 35.9) * mm});
            skLineSegment(sketch, "E2442", {"start": v(1.96, 35.9) * mm, "end": v(1.97, 35.88) * mm});
            skLineSegment(sketch, "E2443", {"start": v(1.97, 35.88) * mm, "end": v(0.8, 34.7) * mm});
            skLineSegment(sketch, "E2444", {"start": v(0.8, 34.7) * mm, "end": v(0.8, 34.7) * mm});
            skLineSegment(sketch, "E2445", {"start": v(0.8, 34.7) * mm, "end": v(16.2, 34.7) * mm});
            skLineSegment(sketch, "E2446", {"start": v(16.2, 34.7) * mm, "end": v(16.2, 50.1) * mm});
            skLineSegment(sketch, "E2447", {"start": v(16.2, 50.1) * mm, "end": v(14.88, 48.8) * mm});
            skLineSegment(sketch, "E2448", {"start": v(14.88, 48.8) * mm, "end": v(14.84, 48.77) * mm});
            skLineSegment(sketch, "E2449", {"start": v(14.84, 48.77) * mm, "end": v(14.8, 48.74) * mm});
            skLineSegment(sketch, "E2450", {"start": v(14.8, 48.74) * mm, "end": v(14.76, 48.73) * mm});
            skLineSegment(sketch, "E2451", {"start": v(14.76, 48.73) * mm, "end": v(14.71, 48.72) * mm});
            skLineSegment(sketch, "E2452", {"start": v(14.71, 48.72) * mm, "end": v(14.68, 48.72) * mm});
            skLineSegment(sketch, "E2453", {"start": v(14.68, 48.72) * mm, "end": v(14.64, 48.72) * mm});
            skLineSegment(sketch, "E2454", {"start": v(14.64, 48.72) * mm, "end": v(14.6, 48.74) * mm});
            skLineSegment(sketch, "E2455", {"start": v(14.6, 48.74) * mm, "end": v(14.57, 48.76) * mm});
            skLineSegment(sketch, "E2456", {"start": v(14.57, 48.76) * mm, "end": v(14.53, 48.79) * mm});
            skLineSegment(sketch, "E2457", {"start": v(14.53, 48.79) * mm, "end": v(14.51, 48.81) * mm});
            skLineSegment(sketch, "E2458", {"start": v(14.51, 48.81) * mm, "end": v(14.5, 48.84) * mm});
            skLineSegment(sketch, "E2459", {"start": v(14.5, 48.84) * mm, "end": v(14.49, 48.86) * mm});
            skLineSegment(sketch, "E2460", {"start": v(14.49, 48.86) * mm, "end": v(14.48, 48.9) * mm});
            skLineSegment(sketch, "E2461", {"start": v(14.48, 48.9) * mm, "end": v(14.48, 48.93) * mm});
            skLineSegment(sketch, "E2462", {"start": v(14.48, 48.93) * mm, "end": v(14.48, 48.97) * mm});
            skLineSegment(sketch, "E2463", {"start": v(14.48, 48.97) * mm, "end": v(14.5, 49.01) * mm});
            skLineSegment(sketch, "E2464", {"start": v(14.5, 49.01) * mm, "end": v(14.52, 49.07) * mm});
            skLineSegment(sketch, "E2465", {"start": v(14.52, 49.07) * mm, "end": v(14.57, 49.18) * mm});
            skLineSegment(sketch, "E2466", {"start": v(14.57, 49.18) * mm, "end": v(14.58, 49.22) * mm});
            skLineSegment(sketch, "E2467", {"start": v(14.58, 49.22) * mm, "end": v(14.58, 49.25) * mm});
            skLineSegment(sketch, "E2468", {"start": v(14.58, 49.25) * mm, "end": v(14.58, 49.28) * mm});
            skLineSegment(sketch, "E2469", {"start": v(14.58, 49.28) * mm, "end": v(14.57, 49.31) * mm});
            skLineSegment(sketch, "E2470", {"start": v(14.57, 49.31) * mm, "end": v(14.56, 49.34) * mm});
            skLineSegment(sketch, "E2471", {"start": v(14.56, 49.34) * mm, "end": v(14.54, 49.37) * mm});
            skLineSegment(sketch, "E2472", {"start": v(14.54, 49.37) * mm, "end": v(14.5, 49.41) * mm});
            skLineSegment(sketch, "E2473", {"start": v(14.5, 49.41) * mm, "end": v(10.99, 52.93) * mm});
            skLineSegment(sketch, "E2474", {"start": v(10.99, 52.93) * mm, "end": v(12.3, 54.25) * mm});
            skLineSegment(sketch, "E2475", {"start": v(12.3, 54.25) * mm, "end": v(15.86, 50.7) * mm});
            skLineSegment(sketch, "E2476", {"start": v(15.86, 50.7) * mm, "end": v(15.9, 50.67) * mm});
            skLineSegment(sketch, "E2477", {"start": v(15.9, 50.67) * mm, "end": v(15.95, 50.65) * mm});
            skLineSegment(sketch, "E2478", {"start": v(15.95, 50.65) * mm, "end": v(16, 50.65) * mm});
            skLineSegment(sketch, "E2479", {"start": v(16, 50.65) * mm, "end": v(16.06, 50.67) * mm});
            skLineSegment(sketch, "E2480", {"start": v(16.06, 50.67) * mm, "end": v(16.14, 50.7) * mm});
            skLineSegment(sketch, "E2481", {"start": v(16.14, 50.7) * mm, "end": v(16.2, 50.73) * mm});
            skLineSegment(sketch, "E2482", {"start": v(16.2, 50.73) * mm, "end": v(16.2, 59.94) * mm});
            skLineSegment(sketch, "E2483", {"start": v(16.2, 59.94) * mm, "end": v(16.19, 59.94) * mm});
            skLineSegment(sketch, "E2484", {"start": v(16.19, 59.94) * mm, "end": v(14.8, 58.56) * mm});
            skLineSegment(sketch, "E2485", {"start": v(14.8, 58.56) * mm, "end": v(14.26, 59.11) * mm});
            skLineSegment(sketch, "E2486", {"start": v(14.26, 59.11) * mm, "end": v(14.3, 59.17) * mm});
            skLineSegment(sketch, "E2487", {"start": v(14.3, 59.17) * mm, "end": v(14.35, 59.25) * mm});
            skLineSegment(sketch, "E2488", {"start": v(14.35, 59.25) * mm, "end": v(14.43, 59.36) * mm});
            skLineSegment(sketch, "E2489", {"start": v(14.43, 59.36) * mm, "end": v(14.5, 59.48) * mm});
            skLineSegment(sketch, "E2490", {"start": v(14.5, 59.48) * mm, "end": v(14.56, 59.6) * mm});
            skLineSegment(sketch, "E2491", {"start": v(14.56, 59.6) * mm, "end": v(14.62, 59.72) * mm});
            skLineSegment(sketch, "E2492", {"start": v(14.62, 59.72) * mm, "end": v(14.67, 59.85) * mm});
            skLineSegment(sketch, "E2493", {"start": v(14.67, 59.85) * mm, "end": v(14.7, 59.97) * mm});
            skLineSegment(sketch, "E2494", {"start": v(14.7, 59.97) * mm, "end": v(14.74, 60.1) * mm});
            skLineSegment(sketch, "E2495", {"start": v(14.74, 60.1) * mm, "end": v(14.77, 60.23) * mm});
            skLineSegment(sketch, "E2496", {"start": v(14.77, 60.23) * mm, "end": v(14.8, 60.34) * mm});
            skLineSegment(sketch, "E2497", {"start": v(14.8, 60.34) * mm, "end": v(14.8, 60.45) * mm});
            skLineSegment(sketch, "E2498", {"start": v(14.8, 60.45) * mm, "end": v(14.82, 60.56) * mm});
            skLineSegment(sketch, "E2499", {"start": v(14.82, 60.56) * mm, "end": v(14.82, 60.68) * mm});
            skLineSegment(sketch, "E2500", {"start": v(14.82, 60.68) * mm, "end": v(14.82, 60.79) * mm});
            skLineSegment(sketch, "E2501", {"start": v(14.82, 60.79) * mm, "end": v(14.82, 60.9) * mm});
            skLineSegment(sketch, "E2502", {"start": v(14.82, 60.9) * mm, "end": v(14.81, 61.01) * mm});
            skLineSegment(sketch, "E2503", {"start": v(14.81, 61.01) * mm, "end": v(14.8, 61.13) * mm});
            skLineSegment(sketch, "E2504", {"start": v(14.8, 61.13) * mm, "end": v(14.78, 61.24) * mm});
            skLineSegment(sketch, "E2505", {"start": v(14.78, 61.24) * mm, "end": v(14.76, 61.35) * mm});
            skLineSegment(sketch, "E2506", {"start": v(14.76, 61.35) * mm, "end": v(14.73, 61.47) * mm});
            skLineSegment(sketch, "E2507", {"start": v(14.73, 61.47) * mm, "end": v(14.7, 61.58) * mm});
            skLineSegment(sketch, "E2508", {"start": v(14.7, 61.58) * mm, "end": v(14.67, 61.7) * mm});
            skLineSegment(sketch, "E2509", {"start": v(14.67, 61.7) * mm, "end": v(14.63, 61.8) * mm});
            skLineSegment(sketch, "E2510", {"start": v(14.63, 61.8) * mm, "end": v(14.58, 61.92) * mm});
            skLineSegment(sketch, "E2511", {"start": v(14.58, 61.92) * mm, "end": v(14.53, 62.04) * mm});
            skLineSegment(sketch, "E2512", {"start": v(14.53, 62.04) * mm, "end": v(14.49, 62.13) * mm});
            skLineSegment(sketch, "E2513", {"start": v(14.49, 62.13) * mm, "end": v(14.45, 62.23) * mm});
            skLineSegment(sketch, "E2514", {"start": v(14.45, 62.23) * mm, "end": v(14.42, 62.32) * mm});
            skLineSegment(sketch, "E2515", {"start": v(14.42, 62.32) * mm, "end": v(14.4, 62.39) * mm});
            skLineSegment(sketch, "E2516", {"start": v(14.4, 62.39) * mm, "end": v(14.4, 62.44) * mm});
            skLineSegment(sketch, "E2517", {"start": v(14.4, 62.44) * mm, "end": v(14.4, 62.48) * mm});
            skLineSegment(sketch, "E2518", {"start": v(14.4, 62.48) * mm, "end": v(14.4, 62.53) * mm});
            skLineSegment(sketch, "E2519", {"start": v(14.4, 62.53) * mm, "end": v(14.4, 62.57) * mm});
            skLineSegment(sketch, "E2520", {"start": v(14.4, 62.57) * mm, "end": v(14.42, 62.6) * mm});
            skLineSegment(sketch, "E2521", {"start": v(14.42, 62.6) * mm, "end": v(14.44, 62.64) * mm});
            skLineSegment(sketch, "E2522", {"start": v(14.44, 62.64) * mm, "end": v(14.46, 62.68) * mm});
            skLineSegment(sketch, "E2523", {"start": v(14.46, 62.68) * mm, "end": v(14.5, 62.7) * mm});
            skLineSegment(sketch, "E2524", {"start": v(14.5, 62.7) * mm, "end": v(14.55, 62.76) * mm});
            skLineSegment(sketch, "E2525", {"start": v(14.55, 62.76) * mm, "end": v(14.6, 62.8) * mm});
            skLineSegment(sketch, "E2526", {"start": v(14.6, 62.8) * mm, "end": v(14.66, 62.82) * mm});
            skLineSegment(sketch, "E2527", {"start": v(14.66, 62.82) * mm, "end": v(14.72, 62.84) * mm});
            skLineSegment(sketch, "E2528", {"start": v(14.72, 62.84) * mm, "end": v(14.78, 62.84) * mm});
            skLineSegment(sketch, "E2529", {"start": v(14.78, 62.84) * mm, "end": v(14.84, 62.83) * mm});
            skLineSegment(sketch, "E2530", {"start": v(14.84, 62.83) * mm, "end": v(14.9, 62.8) * mm});
            skLineSegment(sketch, "E2531", {"start": v(14.9, 62.8) * mm, "end": v(14.96, 62.77) * mm});
            skLineSegment(sketch, "E2532", {"start": v(14.96, 62.77) * mm, "end": v(15, 62.75) * mm});
            skLineSegment(sketch, "E2533", {"start": v(15, 62.75) * mm, "end": v(16.2, 61.56) * mm});
            skLineSegment(sketch, "E2534", {"start": v(16.2, 61.56) * mm, "end": v(16.2, 61.08) * mm});
            skLineSegment(sketch, "E2535", {"start": v(16.2, 61.08) * mm, "end": v(16.2, 67.1) * mm});
            skLineSegment(sketch, "E2536", {"start": v(16.2, 67.1) * mm, "end": v(10.54, 67.1) * mm});
            skLineSegment(sketch, "E2537", {"start": v(10.54, 67.1) * mm, "end": v(10.54, 67.08) * mm});
            skLineSegment(sketch, "E2538", {"start": v(10.54, 67.08) * mm, "end": v(11.76, 65.85) * mm});
            skLineSegment(sketch, "E2539", {"start": v(11.76, 65.85) * mm, "end": v(11.78, 65.82) * mm});
            skLineSegment(sketch, "E2540", {"start": v(11.78, 65.82) * mm, "end": v(11.8, 65.78) * mm});
            skLineSegment(sketch, "E2541", {"start": v(11.8, 65.78) * mm, "end": v(11.81, 65.73) * mm});
            skLineSegment(sketch, "E2542", {"start": v(11.81, 65.73) * mm, "end": v(11.82, 65.68) * mm});
            skLineSegment(sketch, "E2543", {"start": v(11.82, 65.68) * mm, "end": v(11.81, 65.63) * mm});
            skLineSegment(sketch, "E2544", {"start": v(11.81, 65.63) * mm, "end": v(11.8, 65.58) * mm});
            skLineSegment(sketch, "E2545", {"start": v(11.8, 65.58) * mm, "end": v(11.77, 65.52) * mm});
            skLineSegment(sketch, "E2546", {"start": v(11.77, 65.52) * mm, "end": v(11.74, 65.47) * mm});
            skLineSegment(sketch, "E2547", {"start": v(11.74, 65.47) * mm, "end": v(11.7, 65.42) * mm});
            skLineSegment(sketch, "E2548", {"start": v(11.7, 65.42) * mm, "end": v(11.66, 65.37) * mm});
            skLineSegment(sketch, "E2549", {"start": v(11.66, 65.37) * mm, "end": v(11.62, 65.34) * mm});
            skLineSegment(sketch, "E2550", {"start": v(11.62, 65.34) * mm, "end": v(11.58, 65.31) * mm});
            skLineSegment(sketch, "E2551", {"start": v(11.58, 65.31) * mm, "end": v(11.54, 65.29) * mm});
            skLineSegment(sketch, "E2552", {"start": v(11.54, 65.29) * mm, "end": v(11.5, 65.27) * mm});
            skLineSegment(sketch, "E2553", {"start": v(11.5, 65.27) * mm, "end": v(11.43, 65.27) * mm});
            skLineSegment(sketch, "E2554", {"start": v(11.43, 65.27) * mm, "end": v(11.37, 65.27) * mm});
            skLineSegment(sketch, "E2555", {"start": v(11.37, 65.27) * mm, "end": v(11.32, 65.29) * mm});
            skLineSegment(sketch, "E2556", {"start": v(11.32, 65.29) * mm, "end": v(11.26, 65.3) * mm});
            skLineSegment(sketch, "E2557", {"start": v(11.26, 65.3) * mm, "end": v(11.04, 65.41) * mm});
            skLineSegment(sketch, "E2558", {"start": v(11.04, 65.41) * mm, "end": v(10.97, 65.44) * mm});
            skLineSegment(sketch, "E2559", {"start": v(10.97, 65.44) * mm, "end": v(10.85, 65.5) * mm});
            skLineSegment(sketch, "E2560", {"start": v(10.85, 65.5) * mm, "end": v(10.73, 65.54) * mm});
            skLineSegment(sketch, "E2561", {"start": v(10.73, 65.54) * mm, "end": v(10.61, 65.58) * mm});
            skLineSegment(sketch, "E2562", {"start": v(10.61, 65.58) * mm, "end": v(10.5, 65.62) * mm});
            skLineSegment(sketch, "E2563", {"start": v(10.5, 65.62) * mm, "end": v(10.38, 65.65) * mm});
            skLineSegment(sketch, "E2564", {"start": v(10.38, 65.65) * mm, "end": v(10.27, 65.67) * mm});
            skLineSegment(sketch, "E2565", {"start": v(10.27, 65.67) * mm, "end": v(10.15, 65.7) * mm});
            skLineSegment(sketch, "E2566", {"start": v(10.15, 65.7) * mm, "end": v(10.04, 65.7) * mm});
            skLineSegment(sketch, "E2567", {"start": v(10.04, 65.7) * mm, "end": v(9.95, 65.72) * mm});
            skLineSegment(sketch, "E2568", {"start": v(9.95, 65.72) * mm, "end": v(9.65, 65.72) * mm});
            skLineSegment(sketch, "E2569", {"start": v(9.65, 65.72) * mm, "end": v(9.58, 65.7) * mm});
            skLineSegment(sketch, "E2570", {"start": v(9.58, 65.7) * mm, "end": v(9.4, 65.69) * mm});
            skLineSegment(sketch, "E2571", {"start": v(9.4, 65.69) * mm, "end": v(9.23, 65.65) * mm});
            skLineSegment(sketch, "E2572", {"start": v(9.23, 65.65) * mm, "end": v(9.05, 65.6) * mm});
            skLineSegment(sketch, "E2573", {"start": v(9.05, 65.6) * mm, "end": v(8.87, 65.53) * mm});
            skLineSegment(sketch, "E2574", {"start": v(8.87, 65.53) * mm, "end": v(8.81, 65.5) * mm});
            skLineSegment(sketch, "E2575", {"start": v(8.81, 65.5) * mm, "end": v(8.58, 65.39) * mm});
            skLineSegment(sketch, "E2576", {"start": v(8.58, 65.39) * mm, "end": v(8.57, 65.39) * mm});
            skLineSegment(sketch, "E2577", {"start": v(8.57, 65.39) * mm, "end": v(8.57, 65.39) * mm});
            skLineSegment(sketch, "E2578", {"start": v(8.57, 65.39) * mm, "end": v(8.47, 65.33) * mm});
            skLineSegment(sketch, "E2579", {"start": v(8.47, 65.33) * mm, "end": v(8.3, 65.21) * mm});
            skLineSegment(sketch, "E2580", {"start": v(8.3, 65.21) * mm, "end": v(8.21, 65.16) * mm});
            skLineSegment(sketch, "E2581", {"start": v(8.21, 65.16) * mm, "end": v(7.67, 65.7) * mm});
            skLineSegment(sketch, "E2582", {"start": v(7.67, 65.7) * mm, "end": v(7.67, 65.7) * mm});
            skLineSegment(sketch, "E2583", {"start": v(7.67, 65.7) * mm, "end": v(7.66, 65.7) * mm});
            skLineSegment(sketch, "E2584", {"start": v(7.66, 65.7) * mm, "end": v(7.66, 65.7) * mm});
            skLineSegment(sketch, "E2585", {"start": v(7.66, 65.7) * mm, "end": v(7.68, 65.72) * mm});
            skLineSegment(sketch, "E2586", {"start": v(7.68, 65.72) * mm, "end": v(7.69, 65.73) * mm});
            skLineSegment(sketch, "E2587", {"start": v(7.69, 65.73) * mm, "end": v(7.7, 65.73) * mm});
            skLineSegment(sketch, "E2588", {"start": v(7.7, 65.73) * mm, "end": v(7.7, 65.73) * mm});
            skLineSegment(sketch, "E2589", {"start": v(7.7, 65.73) * mm, "end": v(7.7, 65.74) * mm});
            skLineSegment(sketch, "E2590", {"start": v(7.7, 65.74) * mm, "end": v(9.04, 67.08) * mm});
            skLineSegment(sketch, "E2591", {"start": v(9.04, 67.08) * mm, "end": v(9.04, 67.1) * mm});
            skLineSegment(sketch, "E2592", {"start": v(9.04, 67.1) * mm, "end": v(-16.2, 67.09) * mm});
            skLineSegment(sketch, "E2593", {"start": v(-16.2, 67.09) * mm, "end": v(-16.2, 41.86) * mm});
            skLineSegment(sketch, "E2594", {"start": v(-16.2, 41.86) * mm, "end": v(-16.19, 41.86) * mm});
            skLineSegment(sketch, "E2595", {"start": v(-16.19, 41.86) * mm, "end": v(-13.87, 44.17) * mm});
            skLineSegment(sketch, "E2596", {"start": v(-13.87, 44.17) * mm, "end": v(-13.82, 44.21) * mm});
            skLineSegment(sketch, "E2597", {"start": v(-13.82, 44.21) * mm, "end": v(-13.74, 44.27) * mm});
            skLineSegment(sketch, "E2598", {"start": v(-13.74, 44.27) * mm, "end": v(-13.66, 44.3) * mm});
            skLineSegment(sketch, "E2599", {"start": v(-13.66, 44.3) * mm, "end": v(-13.58, 44.32) * mm});
            skLineSegment(sketch, "E2600", {"start": v(-13.58, 44.32) * mm, "end": v(-13.5, 44.33) * mm});
            skLineSegment(sketch, "E2601", {"start": v(-13.5, 44.33) * mm, "end": v(-13.45, 44.33) * mm});
            skLineSegment(sketch, "E2602", {"start": v(-13.45, 44.33) * mm, "end": v(-13.4, 44.32) * mm});
            skLineSegment(sketch, "E2603", {"start": v(-13.4, 44.32) * mm, "end": v(-13.37, 44.3) * mm});
            skLineSegment(sketch, "E2604", {"start": v(-13.37, 44.3) * mm, "end": v(-13.32, 44.28) * mm});
            skLineSegment(sketch, "E2605", {"start": v(-13.32, 44.28) * mm, "end": v(-13.27, 44.24) * mm});
            skLineSegment(sketch, "E2606", {"start": v(-13.27, 44.24) * mm, "end": v(-13.22, 44.2) * mm});
            skLineSegment(sketch, "E2607", {"start": v(-13.22, 44.2) * mm, "end": v(-13.19, 44.15) * mm});
            skLineSegment(sketch, "E2608", {"start": v(-13.19, 44.15) * mm, "end": v(-13.16, 44.1) * mm});
            skLineSegment(sketch, "E2609", {"start": v(-13.16, 44.1) * mm, "end": v(-13.14, 44.04) * mm});
            skLineSegment(sketch, "E2610", {"start": v(-13.14, 44.04) * mm, "end": v(-13.14, 43.98) * mm});
            skLineSegment(sketch, "E2611", {"start": v(-13.14, 43.98) * mm, "end": v(-13.14, 43.92) * mm});
            skLineSegment(sketch, "E2612", {"start": v(-13.14, 43.92) * mm, "end": v(-13.15, 43.86) * mm});
            skLineSegment(sketch, "E2613", {"start": v(-13.15, 43.86) * mm, "end": v(-13.16, 43.82) * mm});
            skLineSegment(sketch, "E2614", {"start": v(-13.16, 43.82) * mm, "end": v(-13.28, 43.58) * mm});
            skLineSegment(sketch, "E2615", {"start": v(-13.28, 43.58) * mm, "end": v(-13.3, 43.51) * mm});
            skLineSegment(sketch, "E2616", {"start": v(-13.3, 43.51) * mm, "end": v(-13.32, 43.44) * mm});
            skLineSegment(sketch, "E2617", {"start": v(-13.32, 43.44) * mm, "end": v(-13.32, 43.38) * mm});
            skLineSegment(sketch, "E2618", {"start": v(-13.32, 43.38) * mm, "end": v(-13.32, 43.32) * mm});
            skLineSegment(sketch, "E2619", {"start": v(-13.32, 43.32) * mm, "end": v(-13.31, 43.28) * mm});
            skLineSegment(sketch, "E2620", {"start": v(-13.31, 43.28) * mm, "end": v(-13.27, 43.2) * mm});
            skLineSegment(sketch, "E2621", {"start": v(-13.27, 43.2) * mm, "end": v(-13.22, 43.14) * mm});
            skLineSegment(sketch, "E2622", {"start": v(-13.22, 43.14) * mm, "end": v(-13.2, 43.11) * mm});
            skLineSegment(sketch, "E2623", {"start": v(-13.2, 43.11) * mm, "end": v(-13.2, 43.11) * mm});
            skLineSegment(sketch, "E2624", {"start": v(-13.2, 43.11) * mm, "end": v(-7.77, 37.68) * mm});
            skLineSegment(sketch, "E2625", {"start": v(-7.77, 37.68) * mm, "end": v(-7.72, 37.64) * mm});
            skLineSegment(sketch, "E2626", {"start": v(-7.72, 37.64) * mm, "end": v(-7.64, 37.6) * mm});
            skLineSegment(sketch, "E2627", {"start": v(-7.64, 37.6) * mm, "end": v(-7.6, 37.58) * mm});
            skLineSegment(sketch, "E2628", {"start": v(-7.6, 37.58) * mm, "end": v(-7.52, 37.58) * mm});
            skLineSegment(sketch, "E2629", {"start": v(-7.52, 37.58) * mm, "end": v(-7.45, 37.58) * mm});
            skLineSegment(sketch, "E2630", {"start": v(-7.45, 37.58) * mm, "end": v(-7.38, 37.6) * mm});
            skLineSegment(sketch, "E2631", {"start": v(-7.38, 37.6) * mm, "end": v(-7.32, 37.62) * mm});
            skLineSegment(sketch, "E2632", {"start": v(-7.32, 37.62) * mm, "end": v(-7.1, 37.73) * mm});
            skLineSegment(sketch, "E2633", {"start": v(-7.1, 37.73) * mm, "end": v(-7.06, 37.74) * mm});
            skLineSegment(sketch, "E2634", {"start": v(-7.06, 37.74) * mm, "end": v(-7.02, 37.75) * mm});
            skLineSegment(sketch, "E2635", {"start": v(-7.02, 37.75) * mm, "end": v(-6.95, 37.76) * mm});
            skLineSegment(sketch, "E2636", {"start": v(-6.95, 37.76) * mm, "end": v(-6.88, 37.76) * mm});
            skLineSegment(sketch, "E2637", {"start": v(-6.88, 37.76) * mm, "end": v(-6.83, 37.75) * mm});
            skLineSegment(sketch, "E2638", {"start": v(-6.83, 37.75) * mm, "end": v(-6.8, 37.73) * mm});
            skLineSegment(sketch, "E2639", {"start": v(-6.8, 37.73) * mm, "end": v(-6.75, 37.7) * mm});
            skLineSegment(sketch, "E2640", {"start": v(-6.75, 37.7) * mm, "end": v(-6.7, 37.68) * mm});
            skLineSegment(sketch, "E2641", {"start": v(-6.7, 37.68) * mm, "end": v(-6.67, 37.65) * mm});
            skLineSegment(sketch, "E2642", {"start": v(-6.67, 37.65) * mm, "end": v(-6.64, 37.6) * mm});
            skLineSegment(sketch, "E2643", {"start": v(-6.64, 37.6) * mm, "end": v(-6.62, 37.57) * mm});
            skLineSegment(sketch, "E2644", {"start": v(-6.62, 37.57) * mm, "end": v(-6.6, 37.53) * mm});
            skLineSegment(sketch, "E2645", {"start": v(-6.6, 37.53) * mm, "end": v(-6.58, 37.48) * mm});
            skLineSegment(sketch, "E2646", {"start": v(-6.58, 37.48) * mm, "end": v(-6.57, 37.44) * mm});
            skLineSegment(sketch, "E2647", {"start": v(-6.57, 37.44) * mm, "end": v(-6.57, 37.4) * mm});
            skLineSegment(sketch, "E2648", {"start": v(-6.57, 37.4) * mm, "end": v(-6.57, 37.36) * mm});
            skLineSegment(sketch, "E2649", {"start": v(-6.57, 37.36) * mm, "end": v(-6.58, 37.31) * mm});
            skLineSegment(sketch, "E2650", {"start": v(-6.58, 37.31) * mm, "end": v(-6.59, 37.27) * mm});
            skLineSegment(sketch, "E2651", {"start": v(-6.59, 37.27) * mm, "end": v(-6.6, 37.22) * mm});
            skLineSegment(sketch, "E2652", {"start": v(-6.6, 37.22) * mm, "end": v(-6.65, 37.12) * mm});
            skLineSegment(sketch, "E2653", {"start": v(-6.65, 37.12) * mm, "end": v(-6.69, 37.07) * mm});
            skLineSegment(sketch, "E2654", {"start": v(-6.69, 37.07) * mm, "end": v(-9.04, 34.7) * mm});
            skLineSegment(sketch, "E2655", {"start": v(-9.04, 34.7) * mm, "end": v(-9.04, 34.7) * mm});
            skLineSegment(sketch, "E2656", {"start": v(-9.04, 34.7) * mm, "end": v(0.17, 34.7) * mm});
            skLineSegment(sketch, "E2657", {"start": v(-17, 67.9) * mm, "end": v(-17, 33.9) * mm});
            skLineSegment(sketch, "E2658", {"start": v(-17, 33.9) * mm, "end": v(17, 33.9) * mm});
            skLineSegment(sketch, "E2659", {"start": v(17, 33.9) * mm, "end": v(17, 67.9) * mm});
            skLineSegment(sketch, "E2660", {"start": v(17, 67.9) * mm, "end": v(-17, 67.9) * mm});
            skSolve(sketch);
        }
        {
            var Q0;
            Q0=makeQuery(id+"F10.imprint","IMPRINT",FACE,{"disambiguationData":[TD([[makeQuery(id+"F10.imprint","IMPRINT",EDGE,{"derivedFrom":sQuery(id+"F10.wireOp",EDGE,"E14")}),-1.0]])]});
            var Q1;
            Q1=makeQuery(id+"F10.imprint","IMPRINT",FACE,{"disambiguationData":[TD([[makeQuery(id+"F10.imprint","IMPRINT",EDGE,{"derivedFrom":sQuery(id+"F10.wireOp",EDGE,"E351")}),-1.0]])]});
            var Q2;
            Q2=makeQuery(id+"F10.imprint","IMPRINT",FACE,{"disambiguationData":[TD([[makeQuery(id+"F10.imprint","IMPRINT",EDGE,{"derivedFrom":sQuery(id+"F10.wireOp",EDGE,"E907")}),-1.0]])]});
            var Q3;
            Q3=makeQuery(id+"F10.imprint","IMPRINT",FACE,{"disambiguationData":[TD([[makeQuery(id+"F10.imprint","IMPRINT",EDGE,{"derivedFrom":sQuery(id+"F10.wireOp",EDGE,"E1053")}),1.0]])]});
            var Q4;
            Q4=makeQuery(id+"F10.imprint","IMPRINT",FACE,{"disambiguationData":[TD([[makeQuery(id+"F10.imprint","IMPRINT",EDGE,{"derivedFrom":sQuery(id+"F10.wireOp",EDGE,"E139")}),1.0]])]});
            var Q5;
            Q5=makeQuery(id+"F10.imprint","IMPRINT",FACE,{"disambiguationData":[TD([[makeQuery(id+"F10.imprint","IMPRINT",EDGE,{"derivedFrom":sQuery(id+"F10.wireOp",EDGE,"E354")}),1.0]])]});
            var Q6;
            Q6=makeQuery(id+"F10.imprint","IMPRINT",FACE,{"disambiguationData":[TD([[makeQuery(id+"F10.imprint","IMPRINT",EDGE,{"derivedFrom":sQuery(id+"F10.wireOp",EDGE,"E17")}),1.0]])]});
            var Q7;
            Q7=makeQuery(id+"F10.imprint","IMPRINT",FACE,{"disambiguationData":[TD([[makeQuery(id+"F10.imprint","IMPRINT",EDGE,{"derivedFrom":sQuery(id+"F10.wireOp",EDGE,"E51")}),-1.0]])]});
            var Q8;
            Q8=makeQuery(id+"F10.imprint","IMPRINT",FACE,{"disambiguationData":[TD([[makeQuery(id+"F10.imprint","IMPRINT",EDGE,{"derivedFrom":sQuery(id+"F10.wireOp",EDGE,"E1487")}),1.0]])]});
            var Q9;
            Q9=makeQuery(id+"F10.imprint","IMPRINT",FACE,{"disambiguationData":[TD([[makeQuery(id+"F10.imprint","IMPRINT",EDGE,{"derivedFrom":sQuery(id+"F10.wireOp",EDGE,"E1196")}),1.0]])]});
            var Q10;
            Q10=makeQuery(id+"F10.imprint","IMPRINT",FACE,{"disambiguationData":[TD([[makeQuery(id+"F10.imprint","IMPRINT",EDGE,{"derivedFrom":sQuery(id+"F10.wireOp",EDGE,"E729")}),1.0]])]});
            var Q11;
            Q11=makeQuery(id+"F10.imprint","IMPRINT",FACE,{"disambiguationData":[TD([[makeQuery(id+"F10.imprint","IMPRINT",EDGE,{"derivedFrom":sQuery(id+"F10.wireOp",EDGE,"E553")}),1.0]])]});
            var Q12;
            Q12=makeQuery(id+"F10.imprint","IMPRINT",FACE,{"disambiguationData":[TD([[makeQuery(id+"F10.imprint","IMPRINT",EDGE,{"derivedFrom":sQuery(id+"F10.wireOp",EDGE,"E689")}),1.0]])]});
            var Q13;
            Q13=makeQuery(id+"F10.imprint","IMPRINT",FACE,{"disambiguationData":[TD([[makeQuery(id+"F10.imprint","IMPRINT",EDGE,{"derivedFrom":sQuery(id+"F10.wireOp",EDGE,"E630")}),1.0]])]});
            var Q14;
            Q14=makeQuery(id+"F10.imprint","IMPRINT",FACE,{"disambiguationData":[TD([[makeQuery(id+"F10.imprint","IMPRINT",EDGE,{"derivedFrom":sQuery(id+"F10.wireOp",EDGE,"E313")}),1.0]])]});
            var Q15;
            Q15=makeQuery(id+"F10.imprint","IMPRINT",FACE,{"disambiguationData":[TD([[makeQuery(id+"F10.imprint","IMPRINT",EDGE,{"derivedFrom":sQuery(id+"F10.wireOp",EDGE,"E1404")}),1.0]])]});
            var Q16;
            Q16=makeQuery(id+"F10.imprint","IMPRINT",FACE,{"disambiguationData":[TD([[makeQuery(id+"F10.imprint","IMPRINT",EDGE,{"derivedFrom":sQuery(id+"F10.wireOp",EDGE,"E1361")}),-1.0]])]});
            var Q17;
            Q17=makeQuery(id+"F10.imprint","IMPRINT",FACE,{"disambiguationData":[TD([[makeQuery(id+"F10.imprint","IMPRINT",EDGE,{"derivedFrom":sQuery(id+"F10.wireOp",EDGE,"E1691")}),-1.0]])]});
            var Q18;
            Q18=makeQuery(id+"F10.imprint","IMPRINT",FACE,{"disambiguationData":[TD([[makeQuery(id+"F10.imprint","IMPRINT",EDGE,{"derivedFrom":sQuery(id+"F10.wireOp",EDGE,"E1353")}),-1.0]])]});
            var Q19;
            Q19=makeQuery(id+"F10.imprint","IMPRINT",FACE,{"disambiguationData":[TD([[makeQuery(id+"F10.imprint","IMPRINT",EDGE,{"derivedFrom":sQuery(id+"F10.wireOp",EDGE,"E1364")}),1.0]])]});
            var Q20;
            Q20=makeQuery(id+"F10.imprint","IMPRINT",FACE,{"disambiguationData":[TD([[makeQuery(id+"F10.imprint","IMPRINT",EDGE,{"derivedFrom":sQuery(id+"F10.wireOp",EDGE,"E1659")}),1.0]])]});
            var Q21;
            Q21=makeQuery(id+"F10.imprint","IMPRINT",FACE,{"disambiguationData":[TD([[makeQuery(id+"F10.imprint","IMPRINT",EDGE,{"derivedFrom":sQuery(id+"F10.wireOp",EDGE,"E1698")}),1.0]])]});
            var Q22;
            Q22=makeQuery(id+"F10.imprint","IMPRINT",FACE,{"disambiguationData":[TD([[makeQuery(id+"F10.imprint","IMPRINT",EDGE,{"derivedFrom":sQuery(id+"F10.wireOp",EDGE,"E1572")}),1.0]])]});
            var Q23;
            Q23=makeQuery(id+"F10.imprint","IMPRINT",FACE,{"disambiguationData":[TD([[makeQuery(id+"F10.imprint","IMPRINT",EDGE,{"derivedFrom":sQuery(id+"F10.wireOp",EDGE,"E1985")}),1.0]])]});
            var Q24;
            Q24=makeQuery(id+"F10.imprint","IMPRINT",FACE,{"disambiguationData":[TD([[makeQuery(id+"F10.imprint","IMPRINT",EDGE,{"derivedFrom":sQuery(id+"F10.wireOp",EDGE,"E1817")}),1.0]])]});
            var Q25;
            Q25=makeQuery(id+"F10.imprint","IMPRINT",FACE,{"disambiguationData":[TD([[makeQuery(id+"F10.imprint","IMPRINT",EDGE,{"derivedFrom":sQuery(id+"F10.wireOp",EDGE,"E1957")}),1.0]])]});
            var Q26;
            Q26=makeQuery(id+"F10.imprint","IMPRINT",FACE,{"disambiguationData":[TD([[makeQuery(id+"F10.imprint","IMPRINT",EDGE,{"derivedFrom":sQuery(id+"F10.wireOp",EDGE,"E1782")}),1.0]])]});
            var Q27;
            Q27=makeQuery(id+"F10.imprint","IMPRINT",FACE,{"disambiguationData":[TD([[makeQuery(id+"F10.imprint","IMPRINT",EDGE,{"derivedFrom":sQuery(id+"F10.wireOp",EDGE,"E1871")}),1.0]])]});
            var Q28;
            Q28=makeQuery(id+"F1.opRevolve","SWEPT_FACE",FACE,{"disambiguationData":[OSD([sQuery(id+"F0.wireOp",EDGE,"E1")])]});
            extrude(context, id + "F11", {"entities" : qUnion([Q0, Q1, Q2, Q3, Q4, Q5, Q6, Q7, Q8, Q9, Q10, Q11, Q12, Q13, Q14, Q15, Q16, Q17, Q18, Q19, Q20, Q21, Q22, Q23, Q24, Q25, Q26, Q27]), "operationType" : NewBodyOperationType.ADD, "endBound" : BoundingType.UP_TO_SURFACE, "oppositeDirection" : true, "depth" : 25 * mm, "endBoundEntityFace" : qUnion([Q28]), "offsetDistance" : 25 * mm});
        }
        {
            var Q0;
            Q0=makeQuery(id+"F1.opRevolve","SWEPT_FACE",FACE,{"disambiguationData":[OSD([sQuery(id+"F0.wireOp",EDGE,"E0")])]});
            var sketch = newSketch(context, id + "F12", { "sketchPlane" : qUnion([Q0])});
            skCircle(sketch, "E2661", {"center": v(0, 0) * mm, "radius": 67.75 * mm});
            skCircle(sketch, "E2662", {"center": v(0, 0) * mm, "radius": 100 * mm});
            skSolve(sketch);
        }
        {
            var Q0;
            Q0=qSketchRegion(id+"F12",true);
            extrude(context, id + "F13", {"entities" : qUnion([Q0]), "operationType" : NewBodyOperationType.REMOVE, "oppositeDirection" : true, "depth" : 124 * mm});
        }
    });
